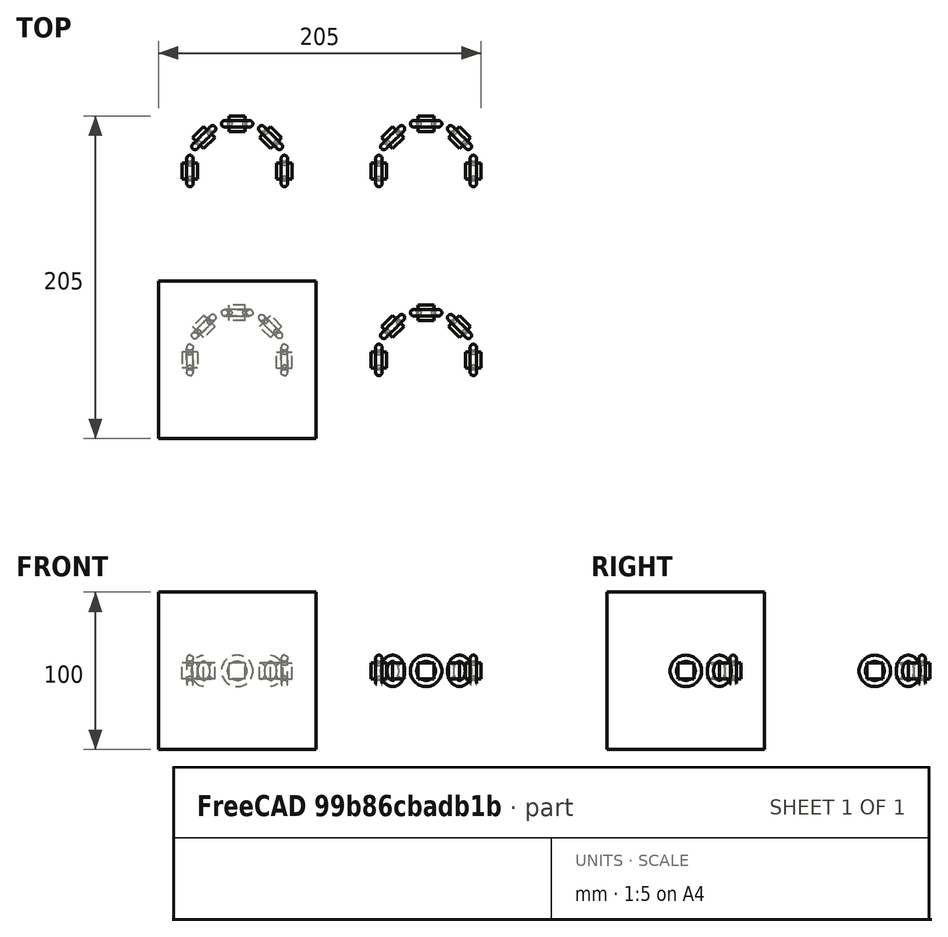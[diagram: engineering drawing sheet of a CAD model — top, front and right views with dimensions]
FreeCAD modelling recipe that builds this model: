
FCSTD DOCUMENT  (FreeCAD 0.21R33694 (Git))
Label: array-of-array-of-solid
License: All rights reserved
objects: App::DocumentObjectGroupPython×1251, Part::FeaturePython×5, App::Part×2, Part::MultiFuse×1
note: 5 computed .brp shape members not serialized (recipe doc carries the construction recipe); baked Part::Feature solids carry a one-line shape summary decoded from their .brp

FEATURE [App::DocumentObjectGroupPython] HALFPI  # scripted group (container) (typed FeaturePython)
  name = HALFPI
  value = pi/2.
FEATURE [App::DocumentObjectGroupPython] PI  # scripted group (container) (typed FeaturePython)
  name = PI
  value = 1.*pi
FEATURE [App::DocumentObjectGroupPython] TWOPI  # scripted group (container) (typed FeaturePython)
  name = TWOPI
  value = 2.*pi
FEATURE [App::DocumentObjectGroupPython] Constants  # scripted group (container) (typed FeaturePython)
  Group = -> [HALFPI,PI,TWOPI]
FEATURE [App::DocumentObjectGroupPython] Variables  # scripted group (container) (typed FeaturePython)
FEATURE [App::DocumentObjectGroupPython] Quantities  # scripted group (container) (typed FeaturePython)
FEATURE [App::DocumentObjectGroupPython] Isotopes  # scripted group (container) (typed FeaturePython)
FEATURE [App::DocumentObjectGroupPython] Elements  # scripted group (container) (typed FeaturePython)
FEATURE [App::DocumentObjectGroupPython] Matrix  # scripted group (container) (typed FeaturePython)
FEATURE [App::DocumentObjectGroupPython] Surfaces  # scripted group (container) (typed FeaturePython)
FEATURE [App::DocumentObjectGroupPython] Opticals  # scripted group (container) (typed FeaturePython)
  Group = -> [Matrix,Surfaces]
FEATURE [App::DocumentObjectGroupPython] G4Isotopes  # scripted group (container) (typed FeaturePython)
FEATURE [App::DocumentObjectGroupPython] H_element  # scripted group (container) (typed FeaturePython)
  Z = 1
  atom_value = 1.008
  formula = H
  name = H_element
FEATURE [App::DocumentObjectGroupPython] He_element  # scripted group (container) (typed FeaturePython)
  Z = 2
  atom_value = 4.0026
  formula = He
  name = He_element
FEATURE [App::DocumentObjectGroupPython] Li_element  # scripted group (container) (typed FeaturePython)
  Z = 3
  atom_value = 6.94
  formula = Li
  name = Li_element
FEATURE [App::DocumentObjectGroupPython] Be_element  # scripted group (container) (typed FeaturePython)
  Z = 4
  atom_value = 9.01218
  formula = Be
  name = Be_element
FEATURE [App::DocumentObjectGroupPython] B_element  # scripted group (container) (typed FeaturePython)
  Z = 5
  atom_value = 10.81
  formula = B
  name = B_element
FEATURE [App::DocumentObjectGroupPython] C_element  # scripted group (container) (typed FeaturePython)
  Z = 6
  atom_value = 12.011
  formula = C
  name = C_element
FEATURE [App::DocumentObjectGroupPython] N_element  # scripted group (container) (typed FeaturePython)
  Z = 7
  atom_value = 14.007
  formula = N
  name = N_element
FEATURE [App::DocumentObjectGroupPython] O_element  # scripted group (container) (typed FeaturePython)
  Z = 8
  atom_value = 15.999
  formula = O
  name = O_element
FEATURE [App::DocumentObjectGroupPython] F_element  # scripted group (container) (typed FeaturePython)
  Z = 9
  atom_value = 18.9984
  formula = F
  name = F_element
FEATURE [App::DocumentObjectGroupPython] Ne_element  # scripted group (container) (typed FeaturePython)
  Z = 10
  atom_value = 20.1797
  formula = Ne
  name = Ne_element
FEATURE [App::DocumentObjectGroupPython] Na_element  # scripted group (container) (typed FeaturePython)
  Z = 11
  atom_value = 22.9898
  formula = Na
  name = Na_element
FEATURE [App::DocumentObjectGroupPython] Mg_element  # scripted group (container) (typed FeaturePython)
  Z = 12
  atom_value = 24.305
  formula = Mg
  name = Mg_element
FEATURE [App::DocumentObjectGroupPython] Al_element  # scripted group (container) (typed FeaturePython)
  Z = 13
  atom_value = 26.9815
  formula = Al
  name = Al_element
FEATURE [App::DocumentObjectGroupPython] Si_element  # scripted group (container) (typed FeaturePython)
  Z = 14
  atom_value = 28.085
  formula = Si
  name = Si_element
FEATURE [App::DocumentObjectGroupPython] P_element  # scripted group (container) (typed FeaturePython)
  Z = 15
  atom_value = 30.9738
  formula = P
  name = P_element
FEATURE [App::DocumentObjectGroupPython] S_element  # scripted group (container) (typed FeaturePython)
  Z = 16
  atom_value = 32.06
  formula = S
  name = S_element
FEATURE [App::DocumentObjectGroupPython] Cl_element  # scripted group (container) (typed FeaturePython)
  Z = 17
  atom_value = 35.45
  formula = Cl
  name = Cl_element
FEATURE [App::DocumentObjectGroupPython] Ar_element  # scripted group (container) (typed FeaturePython)
  Z = 18
  atom_value = 39.95
  formula = Ar
  name = Ar_element
FEATURE [App::DocumentObjectGroupPython] K_element  # scripted group (container) (typed FeaturePython)
  Z = 19
  atom_value = 39.0983
  formula = K
  name = K_element
FEATURE [App::DocumentObjectGroupPython] Ca_element  # scripted group (container) (typed FeaturePython)
  Z = 20
  atom_value = 40.078
  formula = Ca
  name = Ca_element
FEATURE [App::DocumentObjectGroupPython] Sc_element  # scripted group (container) (typed FeaturePython)
  Z = 21
  atom_value = 44.9559
  formula = Sc
  name = Sc_element
FEATURE [App::DocumentObjectGroupPython] Ti_element  # scripted group (container) (typed FeaturePython)
  Z = 22
  atom_value = 47.867
  formula = Ti
  name = Ti_element
FEATURE [App::DocumentObjectGroupPython] V_element  # scripted group (container) (typed FeaturePython)
  Z = 23
  atom_value = 50.9415
  formula = V
  name = V_element
FEATURE [App::DocumentObjectGroupPython] Cr_element  # scripted group (container) (typed FeaturePython)
  Z = 24
  atom_value = 51.9961
  formula = Cr
  name = Cr_element
FEATURE [App::DocumentObjectGroupPython] Mn_element  # scripted group (container) (typed FeaturePython)
  Z = 25
  atom_value = 54.938
  formula = Mn
  name = Mn_element
FEATURE [App::DocumentObjectGroupPython] Fe_element  # scripted group (container) (typed FeaturePython)
  Z = 26
  atom_value = 55.845
  formula = Fe
  name = Fe_element
FEATURE [App::DocumentObjectGroupPython] Co_element  # scripted group (container) (typed FeaturePython)
  Z = 27
  atom_value = 58.9332
  formula = Co
  name = Co_element
FEATURE [App::DocumentObjectGroupPython] Ni_element  # scripted group (container) (typed FeaturePython)
  Z = 28
  atom_value = 58.6934
  formula = Ni
  name = Ni_element
FEATURE [App::DocumentObjectGroupPython] Cu_element  # scripted group (container) (typed FeaturePython)
  Z = 29
  atom_value = 63.546
  formula = Cu
  name = Cu_element
FEATURE [App::DocumentObjectGroupPython] Zn_element  # scripted group (container) (typed FeaturePython)
  Z = 30
  atom_value = 65.38
  formula = Zn
  name = Zn_element
FEATURE [App::DocumentObjectGroupPython] Ga_element  # scripted group (container) (typed FeaturePython)
  Z = 31
  atom_value = 69.723
  formula = Ga
  name = Ga_element
FEATURE [App::DocumentObjectGroupPython] Ge_element  # scripted group (container) (typed FeaturePython)
  Z = 32
  atom_value = 72.63
  formula = Ge
  name = Ge_element
FEATURE [App::DocumentObjectGroupPython] As_element  # scripted group (container) (typed FeaturePython)
  Z = 33
  atom_value = 74.9216
  formula = As
  name = As_element
FEATURE [App::DocumentObjectGroupPython] Se_element  # scripted group (container) (typed FeaturePython)
  Z = 34
  atom_value = 78.971
  formula = Se
  name = Se_element
FEATURE [App::DocumentObjectGroupPython] Br_element  # scripted group (container) (typed FeaturePython)
  Z = 35
  atom_value = 79.904
  formula = Br
  name = Br_element
FEATURE [App::DocumentObjectGroupPython] Kr_element  # scripted group (container) (typed FeaturePython)
  Z = 36
  atom_value = 83.798
  formula = Kr
  name = Kr_element
FEATURE [App::DocumentObjectGroupPython] Rb_element  # scripted group (container) (typed FeaturePython)
  Z = 37
  atom_value = 85.4678
  formula = Rb
  name = Rb_element
FEATURE [App::DocumentObjectGroupPython] Sr_element  # scripted group (container) (typed FeaturePython)
  Z = 38
  atom_value = 87.62
  formula = Sr
  name = Sr_element
FEATURE [App::DocumentObjectGroupPython] Y_element  # scripted group (container) (typed FeaturePython)
  Z = 39
  atom_value = 88.9058
  formula = Y
  name = Y_element
FEATURE [App::DocumentObjectGroupPython] Zr_element  # scripted group (container) (typed FeaturePython)
  Z = 40
  atom_value = 91.224
  formula = Zr
  name = Zr_element
FEATURE [App::DocumentObjectGroupPython] Nb_element  # scripted group (container) (typed FeaturePython)
  Z = 41
  atom_value = 92.9064
  formula = Nb
  name = Nb_element
FEATURE [App::DocumentObjectGroupPython] Mo_element  # scripted group (container) (typed FeaturePython)
  Z = 42
  atom_value = 95.95
  formula = Mo
  name = Mo_element
FEATURE [App::DocumentObjectGroupPython] Tc_element  # scripted group (container) (typed FeaturePython)
  Z = 43
  atom_value = 97
  formula = Tc
  name = Tc_element
FEATURE [App::DocumentObjectGroupPython] Ru_element  # scripted group (container) (typed FeaturePython)
  Z = 44
  atom_value = 101.07
  formula = Ru
  name = Ru_element
FEATURE [App::DocumentObjectGroupPython] Rh_element  # scripted group (container) (typed FeaturePython)
  Z = 45
  atom_value = 102.905
  formula = Rh
  name = Rh_element
FEATURE [App::DocumentObjectGroupPython] Pd_element  # scripted group (container) (typed FeaturePython)
  Z = 46
  atom_value = 106.42
  formula = Pd
  name = Pd_element
FEATURE [App::DocumentObjectGroupPython] Ag_element  # scripted group (container) (typed FeaturePython)
  Z = 47
  atom_value = 107.868
  formula = Ag
  name = Ag_element
FEATURE [App::DocumentObjectGroupPython] Cd_element  # scripted group (container) (typed FeaturePython)
  Z = 48
  atom_value = 112.414
  formula = Cd
  name = Cd_element
FEATURE [App::DocumentObjectGroupPython] In_element  # scripted group (container) (typed FeaturePython)
  Z = 49
  atom_value = 114.818
  formula = In
  name = In_element
FEATURE [App::DocumentObjectGroupPython] Sn_element  # scripted group (container) (typed FeaturePython)
  Z = 50
  atom_value = 118.71
  formula = Sn
  name = Sn_element
FEATURE [App::DocumentObjectGroupPython] Sb_element  # scripted group (container) (typed FeaturePython)
  Z = 51
  atom_value = 121.76
  formula = Sb
  name = Sb_element
FEATURE [App::DocumentObjectGroupPython] Te_element  # scripted group (container) (typed FeaturePython)
  Z = 52
  atom_value = 127.6
  formula = Te
  name = Te_element
FEATURE [App::DocumentObjectGroupPython] I_element  # scripted group (container) (typed FeaturePython)
  Z = 53
  atom_value = 126.904
  formula = I
  name = I_element
FEATURE [App::DocumentObjectGroupPython] Xe_element  # scripted group (container) (typed FeaturePython)
  Z = 54
  atom_value = 131.293
  formula = Xe
  name = Xe_element
FEATURE [App::DocumentObjectGroupPython] Cs_element  # scripted group (container) (typed FeaturePython)
  Z = 55
  atom_value = 132.905
  formula = Cs
  name = Cs_element
FEATURE [App::DocumentObjectGroupPython] Ba_element  # scripted group (container) (typed FeaturePython)
  Z = 56
  atom_value = 137.327
  formula = Ba
  name = Ba_element
FEATURE [App::DocumentObjectGroupPython] La_element  # scripted group (container) (typed FeaturePython)
  Z = 57
  atom_value = 138.905
  formula = La
  name = La_element
FEATURE [App::DocumentObjectGroupPython] Ce_element  # scripted group (container) (typed FeaturePython)
  Z = 58
  atom_value = 140.116
  formula = Ce
  name = Ce_element
FEATURE [App::DocumentObjectGroupPython] Pr_element  # scripted group (container) (typed FeaturePython)
  Z = 59
  atom_value = 140.908
  formula = Pr
  name = Pr_element
FEATURE [App::DocumentObjectGroupPython] Nd_element  # scripted group (container) (typed FeaturePython)
  Z = 60
  atom_value = 144.242
  formula = Nd
  name = Nd_element
FEATURE [App::DocumentObjectGroupPython] Pm_element  # scripted group (container) (typed FeaturePython)
  Z = 61
  atom_value = 145
  formula = Pm
  name = Pm_element
FEATURE [App::DocumentObjectGroupPython] Sm_element  # scripted group (container) (typed FeaturePython)
  Z = 62
  atom_value = 150.36
  formula = Sm
  name = Sm_element
FEATURE [App::DocumentObjectGroupPython] Eu_element  # scripted group (container) (typed FeaturePython)
  Z = 63
  atom_value = 151.964
  formula = Eu
  name = Eu_element
FEATURE [App::DocumentObjectGroupPython] Gd_element  # scripted group (container) (typed FeaturePython)
  Z = 64
  atom_value = 157.25
  formula = Gd
  name = Gd_element
FEATURE [App::DocumentObjectGroupPython] Tb_element  # scripted group (container) (typed FeaturePython)
  Z = 65
  atom_value = 158.925
  formula = Tb
  name = Tb_element
FEATURE [App::DocumentObjectGroupPython] Dy_element  # scripted group (container) (typed FeaturePython)
  Z = 66
  atom_value = 162.5
  formula = Dy
  name = Dy_element
FEATURE [App::DocumentObjectGroupPython] Ho_element  # scripted group (container) (typed FeaturePython)
  Z = 67
  atom_value = 164.93
  formula = Ho
  name = Ho_element
FEATURE [App::DocumentObjectGroupPython] Er_element  # scripted group (container) (typed FeaturePython)
  Z = 68
  atom_value = 167.259
  formula = Er
  name = Er_element
FEATURE [App::DocumentObjectGroupPython] Tm_element  # scripted group (container) (typed FeaturePython)
  Z = 69
  atom_value = 168.934
  formula = Tm
  name = Tm_element
FEATURE [App::DocumentObjectGroupPython] Yb_element  # scripted group (container) (typed FeaturePython)
  Z = 70
  atom_value = 173.045
  formula = Yb
  name = Yb_element
FEATURE [App::DocumentObjectGroupPython] Lu_element  # scripted group (container) (typed FeaturePython)
  Z = 71
  atom_value = 174.967
  formula = Lu
  name = Lu_element
FEATURE [App::DocumentObjectGroupPython] Hf_element  # scripted group (container) (typed FeaturePython)
  Z = 72
  atom_value = 178.49
  formula = Hf
  name = Hf_element
FEATURE [App::DocumentObjectGroupPython] Ta_element  # scripted group (container) (typed FeaturePython)
  Z = 73
  atom_value = 180.948
  formula = Ta
  name = Ta_element
FEATURE [App::DocumentObjectGroupPython] W_element  # scripted group (container) (typed FeaturePython)
  Z = 74
  atom_value = 183.84
  formula = W
  name = W_element
FEATURE [App::DocumentObjectGroupPython] Re_element  # scripted group (container) (typed FeaturePython)
  Z = 75
  atom_value = 186.207
  formula = Re
  name = Re_element
FEATURE [App::DocumentObjectGroupPython] Os_element  # scripted group (container) (typed FeaturePython)
  Z = 76
  atom_value = 190.23
  formula = Os
  name = Os_element
FEATURE [App::DocumentObjectGroupPython] Ir_element  # scripted group (container) (typed FeaturePython)
  Z = 77
  atom_value = 192.217
  formula = Ir
  name = Ir_element
FEATURE [App::DocumentObjectGroupPython] Pt_element  # scripted group (container) (typed FeaturePython)
  Z = 78
  atom_value = 195.084
  formula = Pt
  name = Pt_element
FEATURE [App::DocumentObjectGroupPython] Au_element  # scripted group (container) (typed FeaturePython)
  Z = 79
  atom_value = 196.967
  formula = Au
  name = Au_element
FEATURE [App::DocumentObjectGroupPython] Hg_element  # scripted group (container) (typed FeaturePython)
  Z = 80
  atom_value = 200.592
  formula = Hg
  name = Hg_element
FEATURE [App::DocumentObjectGroupPython] Tl_element  # scripted group (container) (typed FeaturePython)
  Z = 81
  atom_value = 204.38
  formula = Tl
  name = Tl_element
FEATURE [App::DocumentObjectGroupPython] Pb_element  # scripted group (container) (typed FeaturePython)
  Z = 82
  atom_value = 207.2
  formula = Pb
  name = Pb_element
FEATURE [App::DocumentObjectGroupPython] Bi_element  # scripted group (container) (typed FeaturePython)
  Z = 83
  atom_value = 208.98
  formula = Bi
  name = Bi_element
FEATURE [App::DocumentObjectGroupPython] Po_element  # scripted group (container) (typed FeaturePython)
  Z = 84
  atom_value = 209
  formula = Po
  name = Po_element
FEATURE [App::DocumentObjectGroupPython] At_element  # scripted group (container) (typed FeaturePython)
  Z = 85
  atom_value = 210
  formula = At
  name = At_element
FEATURE [App::DocumentObjectGroupPython] Rn_element  # scripted group (container) (typed FeaturePython)
  Z = 86
  atom_value = 222
  formula = Rn
  name = Rn_element
FEATURE [App::DocumentObjectGroupPython] Fr_element  # scripted group (container) (typed FeaturePython)
  Z = 87
  atom_value = 223
  formula = Fr
  name = Fr_element
FEATURE [App::DocumentObjectGroupPython] Ra_element  # scripted group (container) (typed FeaturePython)
  Z = 88
  atom_value = 226
  formula = Ra
  name = Ra_element
FEATURE [App::DocumentObjectGroupPython] Ac_element  # scripted group (container) (typed FeaturePython)
  Z = 89
  atom_value = 227
  formula = Ac
  name = Ac_element
FEATURE [App::DocumentObjectGroupPython] Th_element  # scripted group (container) (typed FeaturePython)
  Z = 90
  atom_value = 232.038
  formula = Th
  name = Th_element
FEATURE [App::DocumentObjectGroupPython] Pa_element  # scripted group (container) (typed FeaturePython)
  Z = 91
  atom_value = 231.036
  formula = Pa
  name = Pa_element
FEATURE [App::DocumentObjectGroupPython] U_element  # scripted group (container) (typed FeaturePython)
  Z = 92
  atom_value = 238.029
  formula = U
  name = U_element
FEATURE [App::DocumentObjectGroupPython] Np_element  # scripted group (container) (typed FeaturePython)
  Z = 93
  atom_value = 237
  formula = Np
  name = Np_element
FEATURE [App::DocumentObjectGroupPython] Pu_element  # scripted group (container) (typed FeaturePython)
  Z = 94
  atom_value = 244
  formula = Pu
  name = Pu_element
FEATURE [App::DocumentObjectGroupPython] Am_element  # scripted group (container) (typed FeaturePython)
  Z = 95
  atom_value = 243
  formula = Am
  name = Am_element
FEATURE [App::DocumentObjectGroupPython] Cm_element  # scripted group (container) (typed FeaturePython)
  Z = 96
  atom_value = 247
  formula = Cm
  name = Cm_element
FEATURE [App::DocumentObjectGroupPython] Bk_element  # scripted group (container) (typed FeaturePython)
  Z = 97
  atom_value = 247
  formula = Bk
  name = Bk_element
FEATURE [App::DocumentObjectGroupPython] Cf_element  # scripted group (container) (typed FeaturePython)
  Z = 98
  atom_value = 251
  formula = Cf
  name = Cf_element
FEATURE [App::DocumentObjectGroupPython] G4Elements  # scripted group (container) (typed FeaturePython)
  Group = -> [H_element,He_element,Li_element,Be_element,B_element,C_element,N_element,O_element,F_element,Ne_element,Na_element,Mg_element,Al_element,Si_element,P_element,S_element,Cl_element,Ar_element,K_element,Ca_element,Sc_element,Ti_element,V_element,Cr_element,Mn_element,Fe_element,Co_element,Ni_element,Cu_element,Zn_element,Ga_element,Ge_element,As_element,Se_element,Br_element,Kr_element,Rb_element,+61 more]
FEATURE [App::DocumentObjectGroupPython] H_element001  label="H_element : 0.101"  # scripted group (container) (typed FeaturePython)
  n = 0.101327
FEATURE [App::DocumentObjectGroupPython] C_element001  label="C_element : 0.775"  # scripted group (container) (typed FeaturePython)
  n = 0.7755
FEATURE [App::DocumentObjectGroupPython] N_element001  label="N_element : 0.035"  # scripted group (container) (typed FeaturePython)
  n = 0.035057
FEATURE [App::DocumentObjectGroupPython] O_element001  label="O_element : 0.052"  # scripted group (container) (typed FeaturePython)
  n = 0.0523159
FEATURE [App::DocumentObjectGroupPython] F_element001  label="F_element : 0.017"  # scripted group (container) (typed FeaturePython)
  n = 0.017422
FEATURE [App::DocumentObjectGroupPython] Ca_element001  label="Ca_element : 0.018"  # scripted group (container) (typed FeaturePython)
  n = 0.018378
FEATURE [App::DocumentObjectGroupPython] G4_A_150_TISSUE  label="G4_A-150_TISSUE"  # scripted group (container) (typed FeaturePython)
  Dunit = g/cm3
  Dvalue = 1.127
  Group = -> [H_element001,C_element001,N_element001,O_element001,F_element001,Ca_element001]
  conduct = 2
  density = 1
  expand = 3
  formula = G4_A-150_TISSUE
  name = G4_A-150_TISSUE
  specific = 4
FEATURE [App::DocumentObjectGroupPython] C_element002  label="C_element : 3"  # scripted group (container) (typed FeaturePython)
  n = 3
  ref = C_element
FEATURE [App::DocumentObjectGroupPython] H_element002  label="H_element : 6"  # scripted group (container) (typed FeaturePython)
  n = 6
  ref = H_element
FEATURE [App::DocumentObjectGroupPython] O_element002  label="O_element : 1"  # scripted group (container) (typed FeaturePython)
  n = 1
  ref = O_element
FEATURE [App::DocumentObjectGroupPython] G4_ACETONE  # scripted group (container) (typed FeaturePython)
  Dunit = g/cm3
  Dvalue = 0.7899
  Group = -> [C_element002,H_element002,O_element002]
  conduct = 2
  density = 1
  expand = 3
  formula = G4_ACETONE
  name = G4_ACETONE
  specific = 4
FEATURE [App::DocumentObjectGroupPython] C_element003  label="C_element : 2"  # scripted group (container) (typed FeaturePython)
  n = 2
  ref = C_element
FEATURE [App::DocumentObjectGroupPython] H_element003  label="H_element : 2"  # scripted group (container) (typed FeaturePython)
  n = 2
  ref = H_element
FEATURE [App::DocumentObjectGroupPython] G4_ACETYLENE  # scripted group (container) (typed FeaturePython)
  Dunit = g/cm3
  Dvalue = 0.0010967
  Group = -> [C_element003,H_element003]
  conduct = 2
  density = 1
  expand = 3
  formula = G4_ACETYLENE
  name = G4_ACETYLENE
  specific = 4
FEATURE [App::DocumentObjectGroupPython] C_element004  label="C_element : 5"  # scripted group (container) (typed FeaturePython)
  n = 5
  ref = C_element
FEATURE [App::DocumentObjectGroupPython] H_element004  label="H_element : 5"  # scripted group (container) (typed FeaturePython)
  n = 5
  ref = H_element
FEATURE [App::DocumentObjectGroupPython] N_element002  label="N_element : 5"  # scripted group (container) (typed FeaturePython)
  n = 5
  ref = N_element
FEATURE [App::DocumentObjectGroupPython] G4_ADENINE  # scripted group (container) (typed FeaturePython)
  Dunit = g/cm3
  Dvalue = 1.6
  Group = -> [C_element004,H_element004,N_element002]
  conduct = 2
  density = 1
  expand = 3
  formula = G4_ADENINE
  name = G4_ADENINE
  specific = 4
FEATURE [App::DocumentObjectGroupPython] H_element005  label="H_element : 0.114"  # scripted group (container) (typed FeaturePython)
  n = 0.114
FEATURE [App::DocumentObjectGroupPython] C_element005  label="C_element : 0.598"  # scripted group (container) (typed FeaturePython)
  n = 0.598
FEATURE [App::DocumentObjectGroupPython] N_element003  label="N_element : 0.007"  # scripted group (container) (typed FeaturePython)
  n = 0.007
FEATURE [App::DocumentObjectGroupPython] O_element003  label="O_element : 0.278"  # scripted group (container) (typed FeaturePython)
  n = 0.278
FEATURE [App::DocumentObjectGroupPython] Na_element001  label="Na_element : 0.001"  # scripted group (container) (typed FeaturePython)
  n = 0.001
FEATURE [App::DocumentObjectGroupPython] S_element001  label="S_element : 0.001"  # scripted group (container) (typed FeaturePython)
  n = 0.001
FEATURE [App::DocumentObjectGroupPython] Cl_element001  label="Cl_element : 0.001"  # scripted group (container) (typed FeaturePython)
  n = 0.001
FEATURE [App::DocumentObjectGroupPython] G4_ADIPOSE_TISSUE_ICRP  # scripted group (container) (typed FeaturePython)
  Dunit = g/cm3
  Dvalue = 0.95
  Group = -> [H_element005,C_element005,N_element003,O_element003,Na_element001,S_element001,Cl_element001]
  conduct = 2
  density = 1
  expand = 3
  formula = G4_ADIPOSE_TISSUE_ICRP
  name = G4_ADIPOSE_TISSUE_ICRP
  specific = 4
FEATURE [App::DocumentObjectGroupPython] C_element006  label="C_element : 0.000"  # scripted group (container) (typed FeaturePython)
  n = 0.000124
FEATURE [App::DocumentObjectGroupPython] N_element004  label="N_element : 0.755"  # scripted group (container) (typed FeaturePython)
  n = 0.755268
FEATURE [App::DocumentObjectGroupPython] O_element004  label="O_element : 0.232"  # scripted group (container) (typed FeaturePython)
  n = 0.231781
FEATURE [App::DocumentObjectGroupPython] Ar_element001  label="Ar_element : 0.013"  # scripted group (container) (typed FeaturePython)
  n = 0.012827
FEATURE [App::DocumentObjectGroupPython] G4_AIR  # scripted group (container) (typed FeaturePython)
  Dunit = g/cm3
  Dvalue = 0.00120479
  Group = -> [C_element006,N_element004,O_element004,Ar_element001]
  conduct = 2
  density = 1
  expand = 3
  formula = G4_AIR
  name = G4_AIR
  specific = 4
FEATURE [App::DocumentObjectGroupPython] C_element007  label="C_element : 006"  # scripted group (container) (typed FeaturePython)
  n = 3
  ref = C_element
FEATURE [App::DocumentObjectGroupPython] H_element006  label="H_element : 7"  # scripted group (container) (typed FeaturePython)
  n = 7
  ref = H_element
FEATURE [App::DocumentObjectGroupPython] N_element005  label="N_element : 1"  # scripted group (container) (typed FeaturePython)
  n = 1
  ref = N_element
FEATURE [App::DocumentObjectGroupPython] O_element005  label="O_element : 2"  # scripted group (container) (typed FeaturePython)
  n = 2
  ref = O_element
FEATURE [App::DocumentObjectGroupPython] G4_ALANINE  # scripted group (container) (typed FeaturePython)
  Dunit = g/cm3
  Dvalue = 1.42
  Group = -> [C_element007,H_element006,N_element005,O_element005]
  conduct = 2
  density = 1
  expand = 3
  formula = G4_ALANINE
  name = G4_ALANINE
  specific = 4
FEATURE [App::DocumentObjectGroupPython] Al_element001  label="Al_element : 2"  # scripted group (container) (typed FeaturePython)
  n = 2
  ref = Al_element
FEATURE [App::DocumentObjectGroupPython] O_element006  label="O_element : 3"  # scripted group (container) (typed FeaturePython)
  n = 3
  ref = O_element
FEATURE [App::DocumentObjectGroupPython] G4_ALUMINUM_OXIDE  # scripted group (container) (typed FeaturePython)
  Dunit = g/cm3
  Dvalue = 3.97
  Group = -> [Al_element001,O_element006]
  conduct = 2
  density = 1
  expand = 3
  formula = G4_ALUMINUM_OXIDE
  name = G4_ALUMINUM_OXIDE
  specific = 4
FEATURE [App::DocumentObjectGroupPython] H_element007  label="H_element : 0.106"  # scripted group (container) (typed FeaturePython)
  n = 0.10593
FEATURE [App::DocumentObjectGroupPython] C_element008  label="C_element : 0.789"  # scripted group (container) (typed FeaturePython)
  n = 0.788974
FEATURE [App::DocumentObjectGroupPython] O_element007  label="O_element : 0.105"  # scripted group (container) (typed FeaturePython)
  n = 0.105096
FEATURE [App::DocumentObjectGroupPython] G4_AMBER  # scripted group (container) (typed FeaturePython)
  Dunit = g/cm3
  Dvalue = 1.1
  Group = -> [H_element007,C_element008,O_element007]
  conduct = 2
  density = 1
  expand = 3
  formula = G4_AMBER
  name = G4_AMBER
  specific = 4
FEATURE [App::DocumentObjectGroupPython] N_element006  label="N_element : 006"  # scripted group (container) (typed FeaturePython)
  n = 1
  ref = N_element
FEATURE [App::DocumentObjectGroupPython] H_element008  label="H_element : 3"  # scripted group (container) (typed FeaturePython)
  n = 3
  ref = H_element
FEATURE [App::DocumentObjectGroupPython] G4_AMMONIA  # scripted group (container) (typed FeaturePython)
  Dunit = g/cm3
  Dvalue = 0.000826019
  Group = -> [N_element006,H_element008]
  conduct = 2
  density = 1
  expand = 3
  formula = G4_AMMONIA
  name = G4_AMMONIA
  specific = 4
FEATURE [App::DocumentObjectGroupPython] C_element009  label="C_element : 6"  # scripted group (container) (typed FeaturePython)
  n = 6
  ref = C_element
FEATURE [App::DocumentObjectGroupPython] H_element009  label="H_element : 008"  # scripted group (container) (typed FeaturePython)
  n = 7
  ref = H_element
FEATURE [App::DocumentObjectGroupPython] N_element007  label="N_element : 007"  # scripted group (container) (typed FeaturePython)
  n = 1
  ref = N_element
FEATURE [App::DocumentObjectGroupPython] G4_ANILINE  # scripted group (container) (typed FeaturePython)
  Dunit = g/cm3
  Dvalue = 1.0235
  Group = -> [C_element009,H_element009,N_element007]
  conduct = 2
  density = 1
  expand = 3
  formula = G4_ANILINE
  name = G4_ANILINE
  specific = 4
FEATURE [App::DocumentObjectGroupPython] C_element010  label="C_element : 14"  # scripted group (container) (typed FeaturePython)
  n = 14
  ref = C_element
FEATURE [App::DocumentObjectGroupPython] H_element010  label="H_element : 10"  # scripted group (container) (typed FeaturePython)
  n = 10
  ref = H_element
FEATURE [App::DocumentObjectGroupPython] G4_ANTHRACENE  # scripted group (container) (typed FeaturePython)
  Dunit = g/cm3
  Dvalue = 1.283
  Group = -> [C_element010,H_element010]
  conduct = 2
  density = 1
  expand = 3
  formula = G4_ANTHRACENE
  name = G4_ANTHRACENE
  specific = 4
FEATURE [App::DocumentObjectGroupPython] H_element011  label="H_element : 0.065"  # scripted group (container) (typed FeaturePython)
  n = 0.0654709
FEATURE [App::DocumentObjectGroupPython] C_element011  label="C_element : 0.537"  # scripted group (container) (typed FeaturePython)
  n = 0.536944
FEATURE [App::DocumentObjectGroupPython] N_element008  label="N_element : 0.021"  # scripted group (container) (typed FeaturePython)
  n = 0.0215
FEATURE [App::DocumentObjectGroupPython] O_element008  label="O_element : 0.032"  # scripted group (container) (typed FeaturePython)
  n = 0.032085
FEATURE [App::DocumentObjectGroupPython] F_element002  label="F_element : 0.167"  # scripted group (container) (typed FeaturePython)
  n = 0.167411
FEATURE [App::DocumentObjectGroupPython] Ca_element002  label="Ca_element : 0.177"  # scripted group (container) (typed FeaturePython)
  n = 0.176589
FEATURE [App::DocumentObjectGroupPython] G4_B_100_BONE  label="G4_B-100_BONE"  # scripted group (container) (typed FeaturePython)
  Dunit = g/cm3
  Dvalue = 1.45
  Group = -> [H_element011,C_element011,N_element008,O_element008,F_element002,Ca_element002]
  conduct = 2
  density = 1
  expand = 3
  formula = G4_B-100_BONE
  name = G4_B-100_BONE
  specific = 4
FEATURE [App::DocumentObjectGroupPython] H_element012  label="H_element : 0.057"  # scripted group (container) (typed FeaturePython)
  n = 0.057441
FEATURE [App::DocumentObjectGroupPython] C_element012  label="C_element : 0.790"  # scripted group (container) (typed FeaturePython)
  n = 0.774591
FEATURE [App::DocumentObjectGroupPython] O_element009  label="O_element : 0.168"  # scripted group (container) (typed FeaturePython)
  n = 0.167968
FEATURE [App::DocumentObjectGroupPython] G4_BAKELITE  # scripted group (container) (typed FeaturePython)
  Dunit = g/cm3
  Dvalue = 1.25
  Group = -> [H_element012,C_element012,O_element009]
  conduct = 2
  density = 1
  expand = 3
  formula = G4_BAKELITE
  name = G4_BAKELITE
  specific = 4
FEATURE [App::DocumentObjectGroupPython] Ba_element001  label="Ba_element : 1"  # scripted group (container) (typed FeaturePython)
  n = 1
  ref = Ba_element
FEATURE [App::DocumentObjectGroupPython] F_element003  label="F_element : 2"  # scripted group (container) (typed FeaturePython)
  n = 2
  ref = F_element
FEATURE [App::DocumentObjectGroupPython] G4_BARIUM_FLUORIDE  # scripted group (container) (typed FeaturePython)
  Dunit = g/cm3
  Dvalue = 4.89
  Group = -> [Ba_element001,F_element003]
  conduct = 2
  density = 1
  expand = 3
  formula = G4_BARIUM_FLUORIDE
  name = G4_BARIUM_FLUORIDE
  specific = 4
FEATURE [App::DocumentObjectGroupPython] Ba_element002  label="Ba_element : 002"  # scripted group (container) (typed FeaturePython)
  n = 1
  ref = Ba_element
FEATURE [App::DocumentObjectGroupPython] S_element002  label="S_element : 1"  # scripted group (container) (typed FeaturePython)
  n = 1
  ref = S_element
FEATURE [App::DocumentObjectGroupPython] O_element010  label="O_element : 4"  # scripted group (container) (typed FeaturePython)
  n = 4
  ref = O_element
FEATURE [App::DocumentObjectGroupPython] G4_BARIUM_SULFATE  # scripted group (container) (typed FeaturePython)
  Dunit = g/cm3
  Dvalue = 4.5
  Group = -> [Ba_element002,S_element002,O_element010]
  conduct = 2
  density = 1
  expand = 3
  formula = G4_BARIUM_SULFATE
  name = G4_BARIUM_SULFATE
  specific = 4
FEATURE [App::DocumentObjectGroupPython] C_element013  label="C_element : 007"  # scripted group (container) (typed FeaturePython)
  n = 6
  ref = C_element
FEATURE [App::DocumentObjectGroupPython] H_element013  label="H_element : 009"  # scripted group (container) (typed FeaturePython)
  n = 6
  ref = H_element
FEATURE [App::DocumentObjectGroupPython] G4_BENZENE  # scripted group (container) (typed FeaturePython)
  Dunit = g/cm3
  Dvalue = 0.87865
  Group = -> [C_element013,H_element013]
  conduct = 2
  density = 1
  expand = 3
  formula = G4_BENZENE
  name = G4_BENZENE
  specific = 4
FEATURE [App::DocumentObjectGroupPython] Be_element001  label="Be_element : 1"  # scripted group (container) (typed FeaturePython)
  n = 1
  ref = Be_element
FEATURE [App::DocumentObjectGroupPython] O_element011  label="O_element : 005"  # scripted group (container) (typed FeaturePython)
  n = 1
  ref = O_element
FEATURE [App::DocumentObjectGroupPython] G4_BERYLLIUM_OXIDE  # scripted group (container) (typed FeaturePython)
  Dunit = g/cm3
  Dvalue = 3.01
  Group = -> [Be_element001,O_element011]
  conduct = 2
  density = 1
  expand = 3
  formula = G4_BERYLLIUM_OXIDE
  name = G4_BERYLLIUM_OXIDE
  specific = 4
FEATURE [App::DocumentObjectGroupPython] Bi_element001  label="Bi_element : 4"  # scripted group (container) (typed FeaturePython)
  n = 4
  ref = Bi_element
FEATURE [App::DocumentObjectGroupPython] Ge_element001  label="Ge_element : 3"  # scripted group (container) (typed FeaturePython)
  n = 3
  ref = Ge_element
FEATURE [App::DocumentObjectGroupPython] O_element012  label="O_element : 12"  # scripted group (container) (typed FeaturePython)
  n = 12
  ref = O_element
FEATURE [App::DocumentObjectGroupPython] G4_BGO  # scripted group (container) (typed FeaturePython)
  Dunit = g/cm3
  Dvalue = 7.13
  Group = -> [Bi_element001,Ge_element001,O_element012]
  conduct = 2
  density = 1
  expand = 3
  formula = G4_BGO
  name = G4_BGO
  specific = 4
FEATURE [App::DocumentObjectGroupPython] H_element014  label="H_element : 0.102"  # scripted group (container) (typed FeaturePython)
  n = 0.102
FEATURE [App::DocumentObjectGroupPython] C_element014  label="C_element : 0.110"  # scripted group (container) (typed FeaturePython)
  n = 0.11
FEATURE [App::DocumentObjectGroupPython] N_element009  label="N_element : 0.033"  # scripted group (container) (typed FeaturePython)
  n = 0.033
FEATURE [App::DocumentObjectGroupPython] O_element013  label="O_element : 0.745"  # scripted group (container) (typed FeaturePython)
  n = 0.745
FEATURE [App::DocumentObjectGroupPython] Na_element002  label="Na_element : 0.002"  # scripted group (container) (typed FeaturePython)
  n = 0.001
FEATURE [App::DocumentObjectGroupPython] P_element001  label="P_element : 0.001"  # scripted group (container) (typed FeaturePython)
  n = 0.001
FEATURE [App::DocumentObjectGroupPython] S_element003  label="S_element : 0.002"  # scripted group (container) (typed FeaturePython)
  n = 0.002
FEATURE [App::DocumentObjectGroupPython] Cl_element002  label="Cl_element : 0.003"  # scripted group (container) (typed FeaturePython)
  n = 0.003
FEATURE [App::DocumentObjectGroupPython] K_element001  label="K_element : 0.002"  # scripted group (container) (typed FeaturePython)
  n = 0.002
FEATURE [App::DocumentObjectGroupPython] Fe_element001  label="Fe_element : 0.001"  # scripted group (container) (typed FeaturePython)
  n = 0.001
FEATURE [App::DocumentObjectGroupPython] G4_BLOOD_ICRP  # scripted group (container) (typed FeaturePython)
  Dunit = g/cm3
  Dvalue = 1.06
  Group = -> [H_element014,C_element014,N_element009,O_element013,Na_element002,P_element001,S_element003,Cl_element002,K_element001,Fe_element001]
  conduct = 2
  density = 1
  expand = 3
  formula = G4_BLOOD_ICRP
  name = G4_BLOOD_ICRP
  specific = 4
FEATURE [App::DocumentObjectGroupPython] H_element015  label="H_element : 0.064"  # scripted group (container) (typed FeaturePython)
  n = 0.064
FEATURE [App::DocumentObjectGroupPython] C_element015  label="C_element : 0.278"  # scripted group (container) (typed FeaturePython)
  n = 0.278
FEATURE [App::DocumentObjectGroupPython] N_element010  label="N_element : 0.027"  # scripted group (container) (typed FeaturePython)
  n = 0.027
FEATURE [App::DocumentObjectGroupPython] O_element014  label="O_element : 0.410"  # scripted group (container) (typed FeaturePython)
  n = 0.41
FEATURE [App::DocumentObjectGroupPython] Mg_element001  label="Mg_element : 0.002"  # scripted group (container) (typed FeaturePython)
  n = 0.002
FEATURE [App::DocumentObjectGroupPython] P_element002  label="P_element : 0.070"  # scripted group (container) (typed FeaturePython)
  n = 0.07
FEATURE [App::DocumentObjectGroupPython] S_element004  label="S_element : 0.003"  # scripted group (container) (typed FeaturePython)
  n = 0.002
FEATURE [App::DocumentObjectGroupPython] Ca_element003  label="Ca_element : 0.147"  # scripted group (container) (typed FeaturePython)
  n = 0.147
FEATURE [App::DocumentObjectGroupPython] G4_BONE_COMPACT_ICRU  # scripted group (container) (typed FeaturePython)
  Dunit = g/cm3
  Dvalue = 1.85
  Group = -> [H_element015,C_element015,N_element010,O_element014,Mg_element001,P_element002,S_element004,Ca_element003]
  conduct = 2
  density = 1
  expand = 3
  formula = G4_BONE_COMPACT_ICRU
  name = G4_BONE_COMPACT_ICRU
  specific = 4
FEATURE [App::DocumentObjectGroupPython] H_element016  label="H_element : 0.034"  # scripted group (container) (typed FeaturePython)
  n = 0.034
FEATURE [App::DocumentObjectGroupPython] C_element016  label="C_element : 0.155"  # scripted group (container) (typed FeaturePython)
  n = 0.155
FEATURE [App::DocumentObjectGroupPython] N_element011  label="N_element : 0.042"  # scripted group (container) (typed FeaturePython)
  n = 0.042
FEATURE [App::DocumentObjectGroupPython] O_element015  label="O_element : 0.435"  # scripted group (container) (typed FeaturePython)
  n = 0.435
FEATURE [App::DocumentObjectGroupPython] Na_element003  label="Na_element : 0.003"  # scripted group (container) (typed FeaturePython)
  n = 0.001
FEATURE [App::DocumentObjectGroupPython] Mg_element002  label="Mg_element : 0.003"  # scripted group (container) (typed FeaturePython)
  n = 0.002
FEATURE [App::DocumentObjectGroupPython] P_element003  label="P_element : 0.103"  # scripted group (container) (typed FeaturePython)
  n = 0.103
FEATURE [App::DocumentObjectGroupPython] S_element005  label="S_element : 0.004"  # scripted group (container) (typed FeaturePython)
  n = 0.003
FEATURE [App::DocumentObjectGroupPython] Ca_element004  label="Ca_element : 0.225"  # scripted group (container) (typed FeaturePython)
  n = 0.225
FEATURE [App::DocumentObjectGroupPython] G4_BONE_CORTICAL_ICRP  # scripted group (container) (typed FeaturePython)
  Dunit = g/cm3
  Dvalue = 1.92
  Group = -> [H_element016,C_element016,N_element011,O_element015,Na_element003,Mg_element002,P_element003,S_element005,Ca_element004]
  conduct = 2
  density = 1
  expand = 3
  formula = G4_BONE_CORTICAL_ICRP
  name = G4_BONE_CORTICAL_ICRP
  specific = 4
FEATURE [App::DocumentObjectGroupPython] B_element001  label="B_element : 4"  # scripted group (container) (typed FeaturePython)
  n = 4
  ref = B_element
FEATURE [App::DocumentObjectGroupPython] C_element017  label="C_element : 1"  # scripted group (container) (typed FeaturePython)
  n = 1
  ref = C_element
FEATURE [App::DocumentObjectGroupPython] G4_BORON_CARBIDE  # scripted group (container) (typed FeaturePython)
  Dunit = g/cm3
  Dvalue = 2.52
  Group = -> [B_element001,C_element017]
  conduct = 2
  density = 1
  expand = 3
  formula = G4_BORON_CARBIDE
  name = G4_BORON_CARBIDE
  specific = 4
FEATURE [App::DocumentObjectGroupPython] B_element002  label="B_element : 2"  # scripted group (container) (typed FeaturePython)
  n = 2
  ref = B_element
FEATURE [App::DocumentObjectGroupPython] O_element016  label="O_element : 006"  # scripted group (container) (typed FeaturePython)
  n = 3
  ref = O_element
FEATURE [App::DocumentObjectGroupPython] G4_BORON_OXIDE  # scripted group (container) (typed FeaturePython)
  Dunit = g/cm3
  Dvalue = 1.812
  Group = -> [B_element002,O_element016]
  conduct = 2
  density = 1
  expand = 3
  formula = G4_BORON_OXIDE
  name = G4_BORON_OXIDE
  specific = 4
FEATURE [App::DocumentObjectGroupPython] H_element017  label="H_element : 0.107"  # scripted group (container) (typed FeaturePython)
  n = 0.107
FEATURE [App::DocumentObjectGroupPython] C_element018  label="C_element : 0.145"  # scripted group (container) (typed FeaturePython)
  n = 0.145
FEATURE [App::DocumentObjectGroupPython] N_element012  label="N_element : 0.022"  # scripted group (container) (typed FeaturePython)
  n = 0.022
FEATURE [App::DocumentObjectGroupPython] O_element017  label="O_element : 0.712"  # scripted group (container) (typed FeaturePython)
  n = 0.712
FEATURE [App::DocumentObjectGroupPython] Na_element004  label="Na_element : 0.004"  # scripted group (container) (typed FeaturePython)
  n = 0.002
FEATURE [App::DocumentObjectGroupPython] P_element004  label="P_element : 0.004"  # scripted group (container) (typed FeaturePython)
  n = 0.004
FEATURE [App::DocumentObjectGroupPython] S_element006  label="S_element : 0.005"  # scripted group (container) (typed FeaturePython)
  n = 0.002
FEATURE [App::DocumentObjectGroupPython] Cl_element003  label="Cl_element : 0.004"  # scripted group (container) (typed FeaturePython)
  n = 0.003
FEATURE [App::DocumentObjectGroupPython] K_element002  label="K_element : 0.003"  # scripted group (container) (typed FeaturePython)
  n = 0.003
FEATURE [App::DocumentObjectGroupPython] G4_BRAIN_ICRP  # scripted group (container) (typed FeaturePython)
  Dunit = g/cm3
  Dvalue = 1.04
  Group = -> [H_element017,C_element018,N_element012,O_element017,Na_element004,P_element004,S_element006,Cl_element003,K_element002]
  conduct = 2
  density = 1
  expand = 3
  formula = G4_BRAIN_ICRP
  name = G4_BRAIN_ICRP
  specific = 4
FEATURE [App::DocumentObjectGroupPython] C_element019  label="C_element : 4"  # scripted group (container) (typed FeaturePython)
  n = 4
  ref = C_element
FEATURE [App::DocumentObjectGroupPython] H_element018  label="H_element : 010"  # scripted group (container) (typed FeaturePython)
  n = 10
  ref = H_element
FEATURE [App::DocumentObjectGroupPython] G4_BUTANE  # scripted group (container) (typed FeaturePython)
  Dunit = g/cm3
  Dvalue = 0.00249343
  Group = -> [C_element019,H_element018]
  conduct = 2
  density = 1
  expand = 3
  formula = G4_BUTANE
  name = G4_BUTANE
  specific = 4
FEATURE [App::DocumentObjectGroupPython] C_element020  label="C_element : 008"  # scripted group (container) (typed FeaturePython)
  n = 4
  ref = C_element
FEATURE [App::DocumentObjectGroupPython] H_element019  label="H_element : 011"  # scripted group (container) (typed FeaturePython)
  n = 10
  ref = H_element
FEATURE [App::DocumentObjectGroupPython] O_element018  label="O_element : 007"  # scripted group (container) (typed FeaturePython)
  n = 1
  ref = O_element
FEATURE [App::DocumentObjectGroupPython] G4_N_BUTYL_ALCOHOL  label="G4_N-BUTYL_ALCOHOL"  # scripted group (container) (typed FeaturePython)
  Dunit = g/cm3
  Dvalue = 0.8098
  Group = -> [C_element020,H_element019,O_element018]
  conduct = 2
  density = 1
  expand = 3
  formula = G4_N-BUTYL_ALCOHOL
  name = G4_N-BUTYL_ALCOHOL
  specific = 4
FEATURE [App::DocumentObjectGroupPython] H_element020  label="H_element : 0.025"  # scripted group (container) (typed FeaturePython)
  n = 0.02468
FEATURE [App::DocumentObjectGroupPython] C_element021  label="C_element : 0.502"  # scripted group (container) (typed FeaturePython)
  n = 0.501611
FEATURE [App::DocumentObjectGroupPython] O_element019  label="O_element : 0.005"  # scripted group (container) (typed FeaturePython)
  n = 0.004527
FEATURE [App::DocumentObjectGroupPython] F_element004  label="F_element : 0.465"  # scripted group (container) (typed FeaturePython)
  n = 0.465209
FEATURE [App::DocumentObjectGroupPython] Si_element001  label="Si_element : 0.004"  # scripted group (container) (typed FeaturePython)
  n = 0.003973
FEATURE [App::DocumentObjectGroupPython] G4_C_552  label="G4_C-552"  # scripted group (container) (typed FeaturePython)
  Dunit = g/cm3
  Dvalue = 1.76
  Group = -> [H_element020,C_element021,O_element019,F_element004,Si_element001]
  conduct = 2
  density = 1
  expand = 3
  formula = G4_C-552
  name = G4_C-552
  specific = 4
FEATURE [App::DocumentObjectGroupPython] Cd_element001  label="Cd_element : 1"  # scripted group (container) (typed FeaturePython)
  n = 1
  ref = Cd_element
FEATURE [App::DocumentObjectGroupPython] Te_element001  label="Te_element : 1"  # scripted group (container) (typed FeaturePython)
  n = 1
  ref = Te_element
FEATURE [App::DocumentObjectGroupPython] G4_CADMIUM_TELLURIDE  # scripted group (container) (typed FeaturePython)
  Dunit = g/cm3
  Dvalue = 6.2
  Group = -> [Cd_element001,Te_element001]
  conduct = 2
  density = 1
  expand = 3
  formula = G4_CADMIUM_TELLURIDE
  name = G4_CADMIUM_TELLURIDE
  specific = 4
FEATURE [App::DocumentObjectGroupPython] Cd_element002  label="Cd_element : 002"  # scripted group (container) (typed FeaturePython)
  n = 1
  ref = Cd_element
FEATURE [App::DocumentObjectGroupPython] W_element001  label="W_element : 1"  # scripted group (container) (typed FeaturePython)
  n = 1
  ref = W_element
FEATURE [App::DocumentObjectGroupPython] O_element020  label="O_element : 008"  # scripted group (container) (typed FeaturePython)
  n = 4
  ref = O_element
FEATURE [App::DocumentObjectGroupPython] G4_CADMIUM_TUNGSTATE  # scripted group (container) (typed FeaturePython)
  Dunit = g/cm3
  Dvalue = 7.9
  Group = -> [Cd_element002,W_element001,O_element020]
  conduct = 2
  density = 1
  expand = 3
  formula = G4_CADMIUM_TUNGSTATE
  name = G4_CADMIUM_TUNGSTATE
  specific = 4
FEATURE [App::DocumentObjectGroupPython] Ca_element005  label="Ca_element : 1"  # scripted group (container) (typed FeaturePython)
  n = 1
  ref = Ca_element
FEATURE [App::DocumentObjectGroupPython] C_element022  label="C_element : 009"  # scripted group (container) (typed FeaturePython)
  n = 1
  ref = C_element
FEATURE [App::DocumentObjectGroupPython] O_element021  label="O_element : 009"  # scripted group (container) (typed FeaturePython)
  n = 3
  ref = O_element
FEATURE [App::DocumentObjectGroupPython] G4_CALCIUM_CARBONATE  # scripted group (container) (typed FeaturePython)
  Dunit = g/cm3
  Dvalue = 2.8
  Group = -> [Ca_element005,C_element022,O_element021]
  conduct = 2
  density = 1
  expand = 3
  formula = G4_CALCIUM_CARBONATE
  name = G4_CALCIUM_CARBONATE
  specific = 4
FEATURE [App::DocumentObjectGroupPython] Ca_element006  label="Ca_element : 002"  # scripted group (container) (typed FeaturePython)
  n = 1
  ref = Ca_element
FEATURE [App::DocumentObjectGroupPython] F_element005  label="F_element : 003"  # scripted group (container) (typed FeaturePython)
  n = 2
  ref = F_element
FEATURE [App::DocumentObjectGroupPython] G4_CALCIUM_FLUORIDE  # scripted group (container) (typed FeaturePython)
  Dunit = g/cm3
  Dvalue = 3.18
  Group = -> [Ca_element006,F_element005]
  conduct = 2
  density = 1
  expand = 3
  formula = G4_CALCIUM_FLUORIDE
  name = G4_CALCIUM_FLUORIDE
  specific = 4
FEATURE [App::DocumentObjectGroupPython] Ca_element007  label="Ca_element : 003"  # scripted group (container) (typed FeaturePython)
  n = 1
  ref = Ca_element
FEATURE [App::DocumentObjectGroupPython] O_element022  label="O_element : 010"  # scripted group (container) (typed FeaturePython)
  n = 1
  ref = O_element
FEATURE [App::DocumentObjectGroupPython] G4_CALCIUM_OXIDE  # scripted group (container) (typed FeaturePython)
  Dunit = g/cm3
  Dvalue = 3.3
  Group = -> [Ca_element007,O_element022]
  conduct = 2
  density = 1
  expand = 3
  formula = G4_CALCIUM_OXIDE
  name = G4_CALCIUM_OXIDE
  specific = 4
FEATURE [App::DocumentObjectGroupPython] Ca_element008  label="Ca_element : 004"  # scripted group (container) (typed FeaturePython)
  n = 1
  ref = Ca_element
FEATURE [App::DocumentObjectGroupPython] S_element007  label="S_element : 002"  # scripted group (container) (typed FeaturePython)
  n = 1
  ref = S_element
FEATURE [App::DocumentObjectGroupPython] O_element023  label="O_element : 011"  # scripted group (container) (typed FeaturePython)
  n = 4
  ref = O_element
FEATURE [App::DocumentObjectGroupPython] G4_CALCIUM_SULFATE  # scripted group (container) (typed FeaturePython)
  Dunit = g/cm3
  Dvalue = 2.96
  Group = -> [Ca_element008,S_element007,O_element023]
  conduct = 2
  density = 1
  expand = 3
  formula = G4_CALCIUM_SULFATE
  name = G4_CALCIUM_SULFATE
  specific = 4
FEATURE [App::DocumentObjectGroupPython] Ca_element009  label="Ca_element : 005"  # scripted group (container) (typed FeaturePython)
  n = 1
  ref = Ca_element
FEATURE [App::DocumentObjectGroupPython] W_element002  label="W_element : 002"  # scripted group (container) (typed FeaturePython)
  n = 1
  ref = W_element
FEATURE [App::DocumentObjectGroupPython] O_element024  label="O_element : 012"  # scripted group (container) (typed FeaturePython)
  n = 4
  ref = O_element
FEATURE [App::DocumentObjectGroupPython] G4_CALCIUM_TUNGSTATE  # scripted group (container) (typed FeaturePython)
  Dunit = g/cm3
  Dvalue = 6.062
  Group = -> [Ca_element009,W_element002,O_element024]
  conduct = 2
  density = 1
  expand = 3
  formula = G4_CALCIUM_TUNGSTATE
  name = G4_CALCIUM_TUNGSTATE
  specific = 4
FEATURE [App::DocumentObjectGroupPython] C_element023  label="C_element : 010"  # scripted group (container) (typed FeaturePython)
  n = 1
  ref = C_element
FEATURE [App::DocumentObjectGroupPython] O_element025  label="O_element : 013"  # scripted group (container) (typed FeaturePython)
  n = 2
  ref = O_element
FEATURE [App::DocumentObjectGroupPython] G4_CARBON_DIOXIDE  # scripted group (container) (typed FeaturePython)
  Dunit = g/cm3
  Dvalue = 0.00184212
  Group = -> [C_element023,O_element025]
  conduct = 2
  density = 1
  expand = 3
  formula = G4_CARBON_DIOXIDE
  name = G4_CARBON_DIOXIDE
  specific = 4
FEATURE [App::DocumentObjectGroupPython] C_element024  label="C_element : 011"  # scripted group (container) (typed FeaturePython)
  n = 1
  ref = C_element
FEATURE [App::DocumentObjectGroupPython] Cl_element004  label="Cl_element : 4"  # scripted group (container) (typed FeaturePython)
  n = 4
  ref = Cl_element
FEATURE [App::DocumentObjectGroupPython] G4_CARBON_TETRACHLORIDE  # scripted group (container) (typed FeaturePython)
  Dunit = g/cm3
  Dvalue = 1.594
  Group = -> [C_element024,Cl_element004]
  conduct = 2
  density = 1
  expand = 3
  formula = G4_CARBON_TETRACHLORIDE
  name = G4_CARBON_TETRACHLORIDE
  specific = 4
FEATURE [App::DocumentObjectGroupPython] C_element025  label="C_element : 012"  # scripted group (container) (typed FeaturePython)
  n = 6
  ref = C_element
FEATURE [App::DocumentObjectGroupPython] H_element021  label="H_element : 012"  # scripted group (container) (typed FeaturePython)
  n = 10
  ref = H_element
FEATURE [App::DocumentObjectGroupPython] O_element026  label="O_element : 5"  # scripted group (container) (typed FeaturePython)
  n = 5
  ref = O_element
FEATURE [App::DocumentObjectGroupPython] G4_CELLULOSE_CELLOPHANE  # scripted group (container) (typed FeaturePython)
  Dunit = g/cm3
  Dvalue = 1.42
  Group = -> [C_element025,H_element021,O_element026]
  conduct = 2
  density = 1
  expand = 3
  formula = G4_CELLULOSE_CELLOPHANE
  name = G4_CELLULOSE_CELLOPHANE
  specific = 4
FEATURE [App::DocumentObjectGroupPython] H_element022  label="H_element : 0.067"  # scripted group (container) (typed FeaturePython)
  n = 0.067125
FEATURE [App::DocumentObjectGroupPython] C_element026  label="C_element : 0.545"  # scripted group (container) (typed FeaturePython)
  n = 0.545403
FEATURE [App::DocumentObjectGroupPython] O_element027  label="O_element : 0.387"  # scripted group (container) (typed FeaturePython)
  n = 0.387472
FEATURE [App::DocumentObjectGroupPython] G4_CELLULOSE_BUTYRATE  # scripted group (container) (typed FeaturePython)
  Dunit = g/cm3
  Dvalue = 1.2
  Group = -> [H_element022,C_element026,O_element027]
  conduct = 2
  density = 1
  expand = 3
  formula = G4_CELLULOSE_BUTYRATE
  name = G4_CELLULOSE_BUTYRATE
  specific = 4
FEATURE [App::DocumentObjectGroupPython] H_element023  label="H_element : 0.029"  # scripted group (container) (typed FeaturePython)
  n = 0.029216
FEATURE [App::DocumentObjectGroupPython] C_element027  label="C_element : 0.271"  # scripted group (container) (typed FeaturePython)
  n = 0.271296
FEATURE [App::DocumentObjectGroupPython] N_element013  label="N_element : 0.121"  # scripted group (container) (typed FeaturePython)
  n = 0.121276
FEATURE [App::DocumentObjectGroupPython] O_element028  label="O_element : 0.578"  # scripted group (container) (typed FeaturePython)
  n = 0.578212
FEATURE [App::DocumentObjectGroupPython] G4_CELLULOSE_NITRATE  # scripted group (container) (typed FeaturePython)
  Dunit = g/cm3
  Dvalue = 1.49
  Group = -> [H_element023,C_element027,N_element013,O_element028]
  conduct = 2
  density = 1
  expand = 3
  formula = G4_CELLULOSE_NITRATE
  name = G4_CELLULOSE_NITRATE
  specific = 4
FEATURE [App::DocumentObjectGroupPython] H_element024  label="H_element : 0.108"  # scripted group (container) (typed FeaturePython)
  n = 0.107596
FEATURE [App::DocumentObjectGroupPython] N_element014  label="N_element : 0.001"  # scripted group (container) (typed FeaturePython)
  n = 0.0008
FEATURE [App::DocumentObjectGroupPython] O_element029  label="O_element : 0.875"  # scripted group (container) (typed FeaturePython)
  n = 0.874976
FEATURE [App::DocumentObjectGroupPython] S_element008  label="S_element : 0.015"  # scripted group (container) (typed FeaturePython)
  n = 0.014627
FEATURE [App::DocumentObjectGroupPython] Ce_element001  label="Ce_element : 0.002"  # scripted group (container) (typed FeaturePython)
  n = 0.002001
FEATURE [App::DocumentObjectGroupPython] G4_CERIC_SULFATE  # scripted group (container) (typed FeaturePython)
  Dunit = g/cm3
  Dvalue = 1.03
  Group = -> [H_element024,N_element014,O_element029,S_element008,Ce_element001]
  conduct = 2
  density = 1
  expand = 3
  formula = G4_CERIC_SULFATE
  name = G4_CERIC_SULFATE
  specific = 4
FEATURE [App::DocumentObjectGroupPython] Cs_element001  label="Cs_element : 1"  # scripted group (container) (typed FeaturePython)
  n = 1
  ref = Cs_element
FEATURE [App::DocumentObjectGroupPython] F_element006  label="F_element : 1"  # scripted group (container) (typed FeaturePython)
  n = 1
  ref = F_element
FEATURE [App::DocumentObjectGroupPython] G4_CESIUM_FLUORIDE  # scripted group (container) (typed FeaturePython)
  Dunit = g/cm3
  Dvalue = 4.115
  Group = -> [Cs_element001,F_element006]
  conduct = 2
  density = 1
  expand = 3
  formula = G4_CESIUM_FLUORIDE
  name = G4_CESIUM_FLUORIDE
  specific = 4
FEATURE [App::DocumentObjectGroupPython] Cs_element002  label="Cs_element : 002"  # scripted group (container) (typed FeaturePython)
  n = 1
  ref = Cs_element
FEATURE [App::DocumentObjectGroupPython] I_element001  label="I_element : 1"  # scripted group (container) (typed FeaturePython)
  n = 1
  ref = I_element
FEATURE [App::DocumentObjectGroupPython] G4_CESIUM_IODIDE  # scripted group (container) (typed FeaturePython)
  Dunit = g/cm3
  Dvalue = 4.51
  Group = -> [Cs_element002,I_element001]
  conduct = 2
  density = 1
  expand = 3
  formula = G4_CESIUM_IODIDE
  name = G4_CESIUM_IODIDE
  specific = 4
FEATURE [App::DocumentObjectGroupPython] C_element028  label="C_element : 013"  # scripted group (container) (typed FeaturePython)
  n = 6
  ref = C_element
FEATURE [App::DocumentObjectGroupPython] H_element025  label="H_element : 013"  # scripted group (container) (typed FeaturePython)
  n = 5
  ref = H_element
FEATURE [App::DocumentObjectGroupPython] Cl_element005  label="Cl_element : 1"  # scripted group (container) (typed FeaturePython)
  n = 1
  ref = Cl_element
FEATURE [App::DocumentObjectGroupPython] G4_CHLOROBENZENE  # scripted group (container) (typed FeaturePython)
  Dunit = g/cm3
  Dvalue = 1.1058
  Group = -> [C_element028,H_element025,Cl_element005]
  conduct = 2
  density = 1
  expand = 3
  formula = G4_CHLOROBENZENE
  name = G4_CHLOROBENZENE
  specific = 4
FEATURE [App::DocumentObjectGroupPython] C_element029  label="C_element : 014"  # scripted group (container) (typed FeaturePython)
  n = 1
  ref = C_element
FEATURE [App::DocumentObjectGroupPython] H_element026  label="H_element : 1"  # scripted group (container) (typed FeaturePython)
  n = 1
  ref = H_element
FEATURE [App::DocumentObjectGroupPython] Cl_element006  label="Cl_element : 3"  # scripted group (container) (typed FeaturePython)
  n = 3
  ref = Cl_element
FEATURE [App::DocumentObjectGroupPython] G4_CHLOROFORM  # scripted group (container) (typed FeaturePython)
  Dunit = g/cm3
  Dvalue = 1.4832
  Group = -> [C_element029,H_element026,Cl_element006]
  conduct = 2
  density = 1
  expand = 3
  formula = G4_CHLOROFORM
  name = G4_CHLOROFORM
  specific = 4
FEATURE [App::DocumentObjectGroupPython] H_element027  label="H_element : 0.010"  # scripted group (container) (typed FeaturePython)
  n = 0.01
FEATURE [App::DocumentObjectGroupPython] C_element030  label="C_element : 0.001"  # scripted group (container) (typed FeaturePython)
  n = 0.001
FEATURE [App::DocumentObjectGroupPython] O_element030  label="O_element : 0.529"  # scripted group (container) (typed FeaturePython)
  n = 0.529107
FEATURE [App::DocumentObjectGroupPython] Na_element005  label="Na_element : 0.016"  # scripted group (container) (typed FeaturePython)
  n = 0.016
FEATURE [App::DocumentObjectGroupPython] Mg_element003  label="Mg_element : 0.004"  # scripted group (container) (typed FeaturePython)
  n = 0.002
FEATURE [App::DocumentObjectGroupPython] Al_element002  label="Al_element : 0.034"  # scripted group (container) (typed FeaturePython)
  n = 0.033872
FEATURE [App::DocumentObjectGroupPython] Si_element002  label="Si_element : 0.337"  # scripted group (container) (typed FeaturePython)
  n = 0.337021
FEATURE [App::DocumentObjectGroupPython] K_element003  label="K_element : 0.013"  # scripted group (container) (typed FeaturePython)
  n = 0.013
FEATURE [App::DocumentObjectGroupPython] Ca_element010  label="Ca_element : 0.044"  # scripted group (container) (typed FeaturePython)
  n = 0.044
FEATURE [App::DocumentObjectGroupPython] Fe_element002  label="Fe_element : 0.014"  # scripted group (container) (typed FeaturePython)
  n = 0.014
FEATURE [App::DocumentObjectGroupPython] G4_CONCRETE  # scripted group (container) (typed FeaturePython)
  Dunit = g/cm3
  Dvalue = 2.3
  Group = -> [H_element027,C_element030,O_element030,Na_element005,Mg_element003,Al_element002,Si_element002,K_element003,Ca_element010,Fe_element002]
  conduct = 2
  density = 1
  expand = 3
  formula = G4_CONCRETE
  name = G4_CONCRETE
  specific = 4
FEATURE [App::DocumentObjectGroupPython] C_element031  label="C_element : 015"  # scripted group (container) (typed FeaturePython)
  n = 6
  ref = C_element
FEATURE [App::DocumentObjectGroupPython] H_element028  label="H_element : 12"  # scripted group (container) (typed FeaturePython)
  n = 12
  ref = H_element
FEATURE [App::DocumentObjectGroupPython] G4_CYCLOHEXANE  # scripted group (container) (typed FeaturePython)
  Dunit = g/cm3
  Dvalue = 0.779
  Group = -> [C_element031,H_element028]
  conduct = 2
  density = 1
  expand = 3
  formula = G4_CYCLOHEXANE
  name = G4_CYCLOHEXANE
  specific = 4
FEATURE [App::DocumentObjectGroupPython] C_element032  label="C_element : 016"  # scripted group (container) (typed FeaturePython)
  n = 6
  ref = C_element
FEATURE [App::DocumentObjectGroupPython] H_element029  label="H_element : 4"  # scripted group (container) (typed FeaturePython)
  n = 4
  ref = H_element
FEATURE [App::DocumentObjectGroupPython] Cl_element007  label="Cl_element : 2"  # scripted group (container) (typed FeaturePython)
  n = 2
  ref = Cl_element
FEATURE [App::DocumentObjectGroupPython] G4_1_2_DICHLOROBENZENE  label="G4_1.2-DICHLOROBENZENE"  # scripted group (container) (typed FeaturePython)
  Dunit = g/cm3
  Dvalue = 1.3048
  Group = -> [C_element032,H_element029,Cl_element007]
  conduct = 2
  density = 1
  expand = 3
  formula = G4_1.2-DICHLOROBENZENE
  name = G4_1.2-DICHLOROBENZENE
  specific = 4
FEATURE [App::DocumentObjectGroupPython] C_element033  label="C_element : 017"  # scripted group (container) (typed FeaturePython)
  n = 4
  ref = C_element
FEATURE [App::DocumentObjectGroupPython] H_element030  label="H_element : 8"  # scripted group (container) (typed FeaturePython)
  n = 8
  ref = H_element
FEATURE [App::DocumentObjectGroupPython] O_element031  label="O_element : 014"  # scripted group (container) (typed FeaturePython)
  n = 1
  ref = O_element
FEATURE [App::DocumentObjectGroupPython] Cl_element008  label="Cl_element : 005"  # scripted group (container) (typed FeaturePython)
  n = 2
  ref = Cl_element
FEATURE [App::DocumentObjectGroupPython] G4_DICHLORODIETHYL_ETHER  # scripted group (container) (typed FeaturePython)
  Dunit = g/cm3
  Dvalue = 1.2199
  Group = -> [C_element033,H_element030,O_element031,Cl_element008]
  conduct = 2
  density = 1
  expand = 3
  formula = G4_DICHLORODIETHYL_ETHER
  name = G4_DICHLORODIETHYL_ETHER
  specific = 4
FEATURE [App::DocumentObjectGroupPython] C_element034  label="C_element : 018"  # scripted group (container) (typed FeaturePython)
  n = 2
  ref = C_element
FEATURE [App::DocumentObjectGroupPython] H_element031  label="H_element : 014"  # scripted group (container) (typed FeaturePython)
  n = 4
  ref = H_element
FEATURE [App::DocumentObjectGroupPython] Cl_element009  label="Cl_element : 006"  # scripted group (container) (typed FeaturePython)
  n = 2
  ref = Cl_element
FEATURE [App::DocumentObjectGroupPython] G4_1_2_DICHLOROETHANE  label="G4_1.2-DICHLOROETHANE"  # scripted group (container) (typed FeaturePython)
  Dunit = g/cm3
  Dvalue = 1.2351
  Group = -> [C_element034,H_element031,Cl_element009]
  conduct = 2
  density = 1
  expand = 3
  formula = G4_1.2-DICHLOROETHANE
  name = G4_1.2-DICHLOROETHANE
  specific = 4
FEATURE [App::DocumentObjectGroupPython] C_element035  label="C_element : 019"  # scripted group (container) (typed FeaturePython)
  n = 4
  ref = C_element
FEATURE [App::DocumentObjectGroupPython] H_element032  label="H_element : 015"  # scripted group (container) (typed FeaturePython)
  n = 10
  ref = H_element
FEATURE [App::DocumentObjectGroupPython] O_element032  label="O_element : 015"  # scripted group (container) (typed FeaturePython)
  n = 1
  ref = O_element
FEATURE [App::DocumentObjectGroupPython] G4_DIETHYL_ETHER  # scripted group (container) (typed FeaturePython)
  Dunit = g/cm3
  Dvalue = 0.71378
  Group = -> [C_element035,H_element032,O_element032]
  conduct = 2
  density = 1
  expand = 3
  formula = G4_DIETHYL_ETHER
  name = G4_DIETHYL_ETHER
  specific = 4
FEATURE [App::DocumentObjectGroupPython] C_element036  label="C_element : 020"  # scripted group (container) (typed FeaturePython)
  n = 3
  ref = C_element
FEATURE [App::DocumentObjectGroupPython] H_element033  label="H_element : 016"  # scripted group (container) (typed FeaturePython)
  n = 7
  ref = H_element
FEATURE [App::DocumentObjectGroupPython] N_element015  label="N_element : 008"  # scripted group (container) (typed FeaturePython)
  n = 1
  ref = N_element
FEATURE [App::DocumentObjectGroupPython] O_element033  label="O_element : 016"  # scripted group (container) (typed FeaturePython)
  n = 1
  ref = O_element
FEATURE [App::DocumentObjectGroupPython] G4_N_N_DIMETHYL_FORMAMIDE  label="G4_N.N-DIMETHYL_FORMAMIDE"  # scripted group (container) (typed FeaturePython)
  Dunit = g/cm3
  Dvalue = 0.9487
  Group = -> [C_element036,H_element033,N_element015,O_element033]
  conduct = 2
  density = 1
  expand = 3
  formula = G4_N.N-DIMETHYL_FORMAMIDE
  name = G4_N.N-DIMETHYL_FORMAMIDE
  specific = 4
FEATURE [App::DocumentObjectGroupPython] C_element037  label="C_element : 021"  # scripted group (container) (typed FeaturePython)
  n = 2
  ref = C_element
FEATURE [App::DocumentObjectGroupPython] H_element034  label="H_element : 017"  # scripted group (container) (typed FeaturePython)
  n = 6
  ref = H_element
FEATURE [App::DocumentObjectGroupPython] O_element034  label="O_element : 017"  # scripted group (container) (typed FeaturePython)
  n = 1
  ref = O_element
FEATURE [App::DocumentObjectGroupPython] S_element009  label="S_element : 003"  # scripted group (container) (typed FeaturePython)
  n = 1
  ref = S_element
FEATURE [App::DocumentObjectGroupPython] G4_DIMETHYL_SULFOXIDE  # scripted group (container) (typed FeaturePython)
  Dunit = g/cm3
  Dvalue = 1.1014
  Group = -> [C_element037,H_element034,O_element034,S_element009]
  conduct = 2
  density = 1
  expand = 3
  formula = G4_DIMETHYL_SULFOXIDE
  name = G4_DIMETHYL_SULFOXIDE
  specific = 4
FEATURE [App::DocumentObjectGroupPython] C_element038  label="C_element : 022"  # scripted group (container) (typed FeaturePython)
  n = 2
  ref = C_element
FEATURE [App::DocumentObjectGroupPython] H_element035  label="H_element : 018"  # scripted group (container) (typed FeaturePython)
  n = 6
  ref = H_element
FEATURE [App::DocumentObjectGroupPython] G4_ETHANE  # scripted group (container) (typed FeaturePython)
  Dunit = g/cm3
  Dvalue = 0.00125324
  Group = -> [C_element038,H_element035]
  conduct = 2
  density = 1
  expand = 3
  formula = G4_ETHANE
  name = G4_ETHANE
  specific = 4
FEATURE [App::DocumentObjectGroupPython] C_element039  label="C_element : 023"  # scripted group (container) (typed FeaturePython)
  n = 2
  ref = C_element
FEATURE [App::DocumentObjectGroupPython] H_element036  label="H_element : 019"  # scripted group (container) (typed FeaturePython)
  n = 6
  ref = H_element
FEATURE [App::DocumentObjectGroupPython] O_element035  label="O_element : 018"  # scripted group (container) (typed FeaturePython)
  n = 1
  ref = O_element
FEATURE [App::DocumentObjectGroupPython] G4_ETHYL_ALCOHOL  # scripted group (container) (typed FeaturePython)
  Dunit = g/cm3
  Dvalue = 0.7893
  Group = -> [C_element039,H_element036,O_element035]
  conduct = 2
  density = 1
  expand = 3
  formula = G4_ETHYL_ALCOHOL
  name = G4_ETHYL_ALCOHOL
  specific = 4
FEATURE [App::DocumentObjectGroupPython] H_element037  label="H_element : 0.090"  # scripted group (container) (typed FeaturePython)
  n = 0.090027
FEATURE [App::DocumentObjectGroupPython] C_element040  label="C_element : 0.585"  # scripted group (container) (typed FeaturePython)
  n = 0.585182
FEATURE [App::DocumentObjectGroupPython] O_element036  label="O_element : 0.325"  # scripted group (container) (typed FeaturePython)
  n = 0.324791
FEATURE [App::DocumentObjectGroupPython] G4_ETHYL_CELLULOSE  # scripted group (container) (typed FeaturePython)
  Dunit = g/cm3
  Dvalue = 1.13
  Group = -> [H_element037,C_element040,O_element036]
  conduct = 2
  density = 1
  expand = 3
  formula = G4_ETHYL_CELLULOSE
  name = G4_ETHYL_CELLULOSE
  specific = 4
FEATURE [App::DocumentObjectGroupPython] C_element041  label="C_element : 024"  # scripted group (container) (typed FeaturePython)
  n = 2
  ref = C_element
FEATURE [App::DocumentObjectGroupPython] H_element038  label="H_element : 020"  # scripted group (container) (typed FeaturePython)
  n = 4
  ref = H_element
FEATURE [App::DocumentObjectGroupPython] G4_ETHYLENE  # scripted group (container) (typed FeaturePython)
  Dunit = g/cm3
  Dvalue = 0.00117497
  Group = -> [C_element041,H_element038]
  conduct = 2
  density = 1
  expand = 3
  formula = G4_ETHYLENE
  name = G4_ETHYLENE
  specific = 4
FEATURE [App::DocumentObjectGroupPython] H_element039  label="H_element : 0.096"  # scripted group (container) (typed FeaturePython)
  n = 0.096
FEATURE [App::DocumentObjectGroupPython] C_element042  label="C_element : 0.195"  # scripted group (container) (typed FeaturePython)
  n = 0.195
FEATURE [App::DocumentObjectGroupPython] N_element016  label="N_element : 0.057"  # scripted group (container) (typed FeaturePython)
  n = 0.057
FEATURE [App::DocumentObjectGroupPython] O_element037  label="O_element : 0.646"  # scripted group (container) (typed FeaturePython)
  n = 0.646
FEATURE [App::DocumentObjectGroupPython] Na_element006  label="Na_element : 0.017"  # scripted group (container) (typed FeaturePython)
  n = 0.001
FEATURE [App::DocumentObjectGroupPython] P_element005  label="P_element : 0.104"  # scripted group (container) (typed FeaturePython)
  n = 0.001
FEATURE [App::DocumentObjectGroupPython] S_element010  label="S_element : 0.016"  # scripted group (container) (typed FeaturePython)
  n = 0.003
FEATURE [App::DocumentObjectGroupPython] Cl_element010  label="Cl_element : 0.005"  # scripted group (container) (typed FeaturePython)
  n = 0.001
FEATURE [App::DocumentObjectGroupPython] G4_EYE_LENS_ICRP  # scripted group (container) (typed FeaturePython)
  Dunit = g/cm3
  Dvalue = 1.07
  Group = -> [H_element039,C_element042,N_element016,O_element037,Na_element006,P_element005,S_element010,Cl_element010]
  conduct = 2
  density = 1
  expand = 3
  formula = G4_EYE_LENS_ICRP
  name = G4_EYE_LENS_ICRP
  specific = 4
FEATURE [App::DocumentObjectGroupPython] Fe_element003  label="Fe_element : 2"  # scripted group (container) (typed FeaturePython)
  n = 2
  ref = Fe_element
FEATURE [App::DocumentObjectGroupPython] O_element038  label="O_element : 019"  # scripted group (container) (typed FeaturePython)
  n = 3
  ref = O_element
FEATURE [App::DocumentObjectGroupPython] G4_FERRIC_OXIDE  # scripted group (container) (typed FeaturePython)
  Dunit = g/cm3
  Dvalue = 5.2
  Group = -> [Fe_element003,O_element038]
  conduct = 2
  density = 1
  expand = 3
  formula = G4_FERRIC_OXIDE
  name = G4_FERRIC_OXIDE
  specific = 4
FEATURE [App::DocumentObjectGroupPython] Fe_element004  label="Fe_element : 1"  # scripted group (container) (typed FeaturePython)
  n = 1
  ref = Fe_element
FEATURE [App::DocumentObjectGroupPython] B_element003  label="B_element : 1"  # scripted group (container) (typed FeaturePython)
  n = 1
  ref = B_element
FEATURE [App::DocumentObjectGroupPython] G4_FERROBORIDE  # scripted group (container) (typed FeaturePython)
  Dunit = g/cm3
  Dvalue = 7.15
  Group = -> [Fe_element004,B_element003]
  conduct = 2
  density = 1
  expand = 3
  formula = G4_FERROBORIDE
  name = G4_FERROBORIDE
  specific = 4
FEATURE [App::DocumentObjectGroupPython] Fe_element005  label="Fe_element : 003"  # scripted group (container) (typed FeaturePython)
  n = 1
  ref = Fe_element
FEATURE [App::DocumentObjectGroupPython] O_element039  label="O_element : 020"  # scripted group (container) (typed FeaturePython)
  n = 1
  ref = O_element
FEATURE [App::DocumentObjectGroupPython] G4_FERROUS_OXIDE  # scripted group (container) (typed FeaturePython)
  Dunit = g/cm3
  Dvalue = 5.7
  Group = -> [Fe_element005,O_element039]
  conduct = 2
  density = 1
  expand = 3
  formula = G4_FERROUS_OXIDE
  name = G4_FERROUS_OXIDE
  specific = 4
FEATURE [App::DocumentObjectGroupPython] H_element040  label="H_element : 0.115"  # scripted group (container) (typed FeaturePython)
  n = 0.108259
FEATURE [App::DocumentObjectGroupPython] N_element017  label="N_element : 0.000"  # scripted group (container) (typed FeaturePython)
  n = 2.7e-05
FEATURE [App::DocumentObjectGroupPython] O_element040  label="O_element : 0.879"  # scripted group (container) (typed FeaturePython)
  n = 0.878636
FEATURE [App::DocumentObjectGroupPython] Na_element007  label="Na_element : 0.000"  # scripted group (container) (typed FeaturePython)
  n = 2.2e-05
FEATURE [App::DocumentObjectGroupPython] S_element011  label="S_element : 0.013"  # scripted group (container) (typed FeaturePython)
  n = 0.012968
FEATURE [App::DocumentObjectGroupPython] Cl_element011  label="Cl_element : 0.000"  # scripted group (container) (typed FeaturePython)
  n = 3.4e-05
FEATURE [App::DocumentObjectGroupPython] Fe_element006  label="Fe_element : 0.000"  # scripted group (container) (typed FeaturePython)
  n = 5.4e-05
FEATURE [App::DocumentObjectGroupPython] G4_FERROUS_SULFATE  # scripted group (container) (typed FeaturePython)
  Dunit = g/cm3
  Dvalue = 1.024
  Group = -> [H_element040,N_element017,O_element040,Na_element007,S_element011,Cl_element011,Fe_element006]
  conduct = 2
  density = 1
  expand = 3
  formula = G4_FERROUS_SULFATE
  name = G4_FERROUS_SULFATE
  specific = 4
FEATURE [App::DocumentObjectGroupPython] C_element043  label="C_element : 0.099"  # scripted group (container) (typed FeaturePython)
  n = 0.099335
FEATURE [App::DocumentObjectGroupPython] F_element007  label="F_element : 0.314"  # scripted group (container) (typed FeaturePython)
  n = 0.314247
FEATURE [App::DocumentObjectGroupPython] Cl_element012  label="Cl_element : 0.586"  # scripted group (container) (typed FeaturePython)
  n = 0.586418
FEATURE [App::DocumentObjectGroupPython] G4_FREON_12  label="G4_FREON-12"  # scripted group (container) (typed FeaturePython)
  Dunit = g/cm3
  Dvalue = 1.12
  Group = -> [C_element043,F_element007,Cl_element012]
  conduct = 2
  density = 1
  expand = 3
  formula = G4_FREON-12
  name = G4_FREON-12
  specific = 4
FEATURE [App::DocumentObjectGroupPython] C_element044  label="C_element : 0.057"  # scripted group (container) (typed FeaturePython)
  n = 0.057245
FEATURE [App::DocumentObjectGroupPython] F_element008  label="F_element : 0.181"  # scripted group (container) (typed FeaturePython)
  n = 0.181096
FEATURE [App::DocumentObjectGroupPython] Br_element001  label="Br_element : 0.762"  # scripted group (container) (typed FeaturePython)
  n = 0.761659
FEATURE [App::DocumentObjectGroupPython] G4_FREON_12B2  label="G4_FREON-12B2"  # scripted group (container) (typed FeaturePython)
  Dunit = g/cm3
  Dvalue = 1.8
  Group = -> [C_element044,F_element008,Br_element001]
  conduct = 2
  density = 1
  expand = 3
  formula = G4_FREON-12B2
  name = G4_FREON-12B2
  specific = 4
FEATURE [App::DocumentObjectGroupPython] C_element045  label="C_element : 0.115"  # scripted group (container) (typed FeaturePython)
  n = 0.114983
FEATURE [App::DocumentObjectGroupPython] F_element009  label="F_element : 0.546"  # scripted group (container) (typed FeaturePython)
  n = 0.545621
FEATURE [App::DocumentObjectGroupPython] Cl_element013  label="Cl_element : 0.339"  # scripted group (container) (typed FeaturePython)
  n = 0.339396
FEATURE [App::DocumentObjectGroupPython] G4_FREON_13  label="G4_FREON-13"  # scripted group (container) (typed FeaturePython)
  Dunit = g/cm3
  Dvalue = 0.95
  Group = -> [C_element045,F_element009,Cl_element013]
  conduct = 2
  density = 1
  expand = 3
  formula = G4_FREON-13
  name = G4_FREON-13
  specific = 4
FEATURE [App::DocumentObjectGroupPython] C_element046  label="C_element : 025"  # scripted group (container) (typed FeaturePython)
  n = 1
  ref = C_element
FEATURE [App::DocumentObjectGroupPython] F_element010  label="F_element : 3"  # scripted group (container) (typed FeaturePython)
  n = 3
  ref = F_element
FEATURE [App::DocumentObjectGroupPython] Br_element002  label="Br_element : 1"  # scripted group (container) (typed FeaturePython)
  n = 1
  ref = Br_element
FEATURE [App::DocumentObjectGroupPython] G4_FREON_13B1  label="G4_FREON-13B1"  # scripted group (container) (typed FeaturePython)
  Dunit = g/cm3
  Dvalue = 1.5
  Group = -> [C_element046,F_element010,Br_element002]
  conduct = 2
  density = 1
  expand = 3
  formula = G4_FREON-13B1
  name = G4_FREON-13B1
  specific = 4
FEATURE [App::DocumentObjectGroupPython] C_element047  label="C_element : 0.061"  # scripted group (container) (typed FeaturePython)
  n = 0.061309
FEATURE [App::DocumentObjectGroupPython] F_element011  label="F_element : 0.291"  # scripted group (container) (typed FeaturePython)
  n = 0.290924
FEATURE [App::DocumentObjectGroupPython] I_element002  label="I_element : 0.648"  # scripted group (container) (typed FeaturePython)
  n = 0.647767
FEATURE [App::DocumentObjectGroupPython] G4_FREON_13I1  label="G4_FREON-13I1"  # scripted group (container) (typed FeaturePython)
  Dunit = g/cm3
  Dvalue = 1.8
  Group = -> [C_element047,F_element011,I_element002]
  conduct = 2
  density = 1
  expand = 3
  formula = G4_FREON-13I1
  name = G4_FREON-13I1
  specific = 4
FEATURE [App::DocumentObjectGroupPython] Gd_element001  label="Gd_element : 2"  # scripted group (container) (typed FeaturePython)
  n = 2
  ref = Gd_element
FEATURE [App::DocumentObjectGroupPython] O_element041  label="O_element : 021"  # scripted group (container) (typed FeaturePython)
  n = 2
  ref = O_element
FEATURE [App::DocumentObjectGroupPython] S_element012  label="S_element : 004"  # scripted group (container) (typed FeaturePython)
  n = 1
  ref = S_element
FEATURE [App::DocumentObjectGroupPython] G4_GADOLINIUM_OXYSULFIDE  # scripted group (container) (typed FeaturePython)
  Dunit = g/cm3
  Dvalue = 7.44
  Group = -> [Gd_element001,O_element041,S_element012]
  conduct = 2
  density = 1
  expand = 3
  formula = G4_GADOLINIUM_OXYSULFIDE
  name = G4_GADOLINIUM_OXYSULFIDE
  specific = 4
FEATURE [App::DocumentObjectGroupPython] Ga_element001  label="Ga_element : 1"  # scripted group (container) (typed FeaturePython)
  n = 1
  ref = Ga_element
FEATURE [App::DocumentObjectGroupPython] As_element001  label="As_element : 1"  # scripted group (container) (typed FeaturePython)
  n = 1
  ref = As_element
FEATURE [App::DocumentObjectGroupPython] G4_GALLIUM_ARSENIDE  # scripted group (container) (typed FeaturePython)
  Dunit = g/cm3
  Dvalue = 5.31
  Group = -> [Ga_element001,As_element001]
  conduct = 2
  density = 1
  expand = 3
  formula = G4_GALLIUM_ARSENIDE
  name = G4_GALLIUM_ARSENIDE
  specific = 4
FEATURE [App::DocumentObjectGroupPython] H_element041  label="H_element : 0.081"  # scripted group (container) (typed FeaturePython)
  n = 0.08118
FEATURE [App::DocumentObjectGroupPython] C_element048  label="C_element : 0.416"  # scripted group (container) (typed FeaturePython)
  n = 0.41606
FEATURE [App::DocumentObjectGroupPython] N_element018  label="N_element : 0.111"  # scripted group (container) (typed FeaturePython)
  n = 0.11124
FEATURE [App::DocumentObjectGroupPython] O_element042  label="O_element : 0.381"  # scripted group (container) (typed FeaturePython)
  n = 0.38064
FEATURE [App::DocumentObjectGroupPython] S_element013  label="S_element : 0.011"  # scripted group (container) (typed FeaturePython)
  n = 0.01088
FEATURE [App::DocumentObjectGroupPython] G4_GEL_PHOTO_EMULSION  # scripted group (container) (typed FeaturePython)
  Dunit = g/cm3
  Dvalue = 1.2914
  Group = -> [H_element041,C_element048,N_element018,O_element042,S_element013]
  conduct = 2
  density = 1
  expand = 3
  formula = G4_GEL_PHOTO_EMULSION
  name = G4_GEL_PHOTO_EMULSION
  specific = 4
FEATURE [App::DocumentObjectGroupPython] B_element004  label="B_element : 0.040"  # scripted group (container) (typed FeaturePython)
  n = 0.0400639
FEATURE [App::DocumentObjectGroupPython] O_element043  label="O_element : 0.540"  # scripted group (container) (typed FeaturePython)
  n = 0.539561
FEATURE [App::DocumentObjectGroupPython] Na_element008  label="Na_element : 0.028"  # scripted group (container) (typed FeaturePython)
  n = 0.0281909
FEATURE [App::DocumentObjectGroupPython] Al_element003  label="Al_element : 0.012"  # scripted group (container) (typed FeaturePython)
  n = 0.011644
FEATURE [App::DocumentObjectGroupPython] Si_element003  label="Si_element : 0.377"  # scripted group (container) (typed FeaturePython)
  n = 0.377219
FEATURE [App::DocumentObjectGroupPython] K_element004  label="K_element : 0.014"  # scripted group (container) (typed FeaturePython)
  n = 0.00332099
FEATURE [App::DocumentObjectGroupPython] G4_Pyrex_Glass  # scripted group (container) (typed FeaturePython)
  Dunit = g/cm3
  Dvalue = 2.23
  Group = -> [B_element004,O_element043,Na_element008,Al_element003,Si_element003,K_element004]
  conduct = 2
  density = 1
  expand = 3
  formula = G4_Pyrex_Glass
  name = G4_Pyrex_Glass
  specific = 4
FEATURE [App::DocumentObjectGroupPython] O_element044  label="O_element : 0.156"  # scripted group (container) (typed FeaturePython)
  n = 0.156453
FEATURE [App::DocumentObjectGroupPython] Si_element004  label="Si_element : 0.081"  # scripted group (container) (typed FeaturePython)
  n = 0.080866
FEATURE [App::DocumentObjectGroupPython] Ti_element001  label="Ti_element : 0.008"  # scripted group (container) (typed FeaturePython)
  n = 0.008092
FEATURE [App::DocumentObjectGroupPython] As_element002  label="As_element : 0.003"  # scripted group (container) (typed FeaturePython)
  n = 0.002651
FEATURE [App::DocumentObjectGroupPython] Pb_element001  label="Pb_element : 0.752"  # scripted group (container) (typed FeaturePython)
  n = 0.751938
FEATURE [App::DocumentObjectGroupPython] G4_GLASS_LEAD  # scripted group (container) (typed FeaturePython)
  Dunit = g/cm3
  Dvalue = 6.22
  Group = -> [O_element044,Si_element004,Ti_element001,As_element002,Pb_element001]
  conduct = 2
  density = 1
  expand = 3
  formula = G4_GLASS_LEAD
  name = G4_GLASS_LEAD
  specific = 4
FEATURE [App::DocumentObjectGroupPython] O_element045  label="O_element : 0.460"  # scripted group (container) (typed FeaturePython)
  n = 0.4598
FEATURE [App::DocumentObjectGroupPython] Na_element009  label="Na_element : 0.096"  # scripted group (container) (typed FeaturePython)
  n = 0.0964411
FEATURE [App::DocumentObjectGroupPython] Si_element005  label="Si_element : 0.378"  # scripted group (container) (typed FeaturePython)
  n = 0.336553
FEATURE [App::DocumentObjectGroupPython] Ca_element011  label="Ca_element : 0.107"  # scripted group (container) (typed FeaturePython)
  n = 0.107205
FEATURE [App::DocumentObjectGroupPython] G4_GLASS_PLATE  # scripted group (container) (typed FeaturePython)
  Dunit = g/cm3
  Dvalue = 2.4
  Group = -> [O_element045,Na_element009,Si_element005,Ca_element011]
  conduct = 2
  density = 1
  expand = 3
  formula = G4_GLASS_PLATE
  name = G4_GLASS_PLATE
  specific = 4
FEATURE [App::DocumentObjectGroupPython] C_element049  label="C_element : 026"  # scripted group (container) (typed FeaturePython)
  n = 5
  ref = C_element
FEATURE [App::DocumentObjectGroupPython] H_element042  label="H_element : 021"  # scripted group (container) (typed FeaturePython)
  n = 10
  ref = H_element
FEATURE [App::DocumentObjectGroupPython] N_element019  label="N_element : 2"  # scripted group (container) (typed FeaturePython)
  n = 2
  ref = N_element
FEATURE [App::DocumentObjectGroupPython] O_element046  label="O_element : 022"  # scripted group (container) (typed FeaturePython)
  n = 3
  ref = O_element
FEATURE [App::DocumentObjectGroupPython] G4_GLUTAMINE  # scripted group (container) (typed FeaturePython)
  Dunit = g/cm3
  Dvalue = 1.46
  Group = -> [C_element049,H_element042,N_element019,O_element046]
  conduct = 2
  density = 1
  expand = 3
  formula = G4_GLUTAMINE
  name = G4_GLUTAMINE
  specific = 4
FEATURE [App::DocumentObjectGroupPython] C_element050  label="C_element : 027"  # scripted group (container) (typed FeaturePython)
  n = 3
  ref = C_element
FEATURE [App::DocumentObjectGroupPython] H_element043  label="H_element : 022"  # scripted group (container) (typed FeaturePython)
  n = 8
  ref = H_element
FEATURE [App::DocumentObjectGroupPython] O_element047  label="O_element : 023"  # scripted group (container) (typed FeaturePython)
  n = 3
  ref = O_element
FEATURE [App::DocumentObjectGroupPython] G4_GLYCEROL  # scripted group (container) (typed FeaturePython)
  Dunit = g/cm3
  Dvalue = 1.2613
  Group = -> [C_element050,H_element043,O_element047]
  conduct = 2
  density = 1
  expand = 3
  formula = G4_GLYCEROL
  name = G4_GLYCEROL
  specific = 4
FEATURE [App::DocumentObjectGroupPython] C_element051  label="C_element : 028"  # scripted group (container) (typed FeaturePython)
  n = 5
  ref = C_element
FEATURE [App::DocumentObjectGroupPython] H_element044  label="H_element : 023"  # scripted group (container) (typed FeaturePython)
  n = 5
  ref = H_element
FEATURE [App::DocumentObjectGroupPython] N_element020  label="N_element : 009"  # scripted group (container) (typed FeaturePython)
  n = 5
  ref = N_element
FEATURE [App::DocumentObjectGroupPython] O_element048  label="O_element : 024"  # scripted group (container) (typed FeaturePython)
  n = 1
  ref = O_element
FEATURE [App::DocumentObjectGroupPython] G4_GUANINE  # scripted group (container) (typed FeaturePython)
  Dunit = g/cm3
  Dvalue = 2.2
  Group = -> [C_element051,H_element044,N_element020,O_element048]
  conduct = 2
  density = 1
  expand = 3
  formula = G4_GUANINE
  name = G4_GUANINE
  specific = 4
FEATURE [App::DocumentObjectGroupPython] Ca_element012  label="Ca_element : 006"  # scripted group (container) (typed FeaturePython)
  n = 1
  ref = Ca_element
FEATURE [App::DocumentObjectGroupPython] S_element014  label="S_element : 005"  # scripted group (container) (typed FeaturePython)
  n = 1
  ref = S_element
FEATURE [App::DocumentObjectGroupPython] O_element049  label="O_element : 6"  # scripted group (container) (typed FeaturePython)
  n = 6
  ref = O_element
FEATURE [App::DocumentObjectGroupPython] H_element045  label="H_element : 024"  # scripted group (container) (typed FeaturePython)
  n = 4
  ref = H_element
FEATURE [App::DocumentObjectGroupPython] G4_GYPSUM  # scripted group (container) (typed FeaturePython)
  Dunit = g/cm3
  Dvalue = 2.32
  Group = -> [Ca_element012,S_element014,O_element049,H_element045]
  conduct = 2
  density = 1
  expand = 3
  formula = G4_GYPSUM
  name = G4_GYPSUM
  specific = 4
FEATURE [App::DocumentObjectGroupPython] C_element052  label="C_element : 7"  # scripted group (container) (typed FeaturePython)
  n = 7
  ref = C_element
FEATURE [App::DocumentObjectGroupPython] H_element046  label="H_element : 16"  # scripted group (container) (typed FeaturePython)
  n = 16
  ref = H_element
FEATURE [App::DocumentObjectGroupPython] G4_N_HEPTANE  label="G4_N-HEPTANE"  # scripted group (container) (typed FeaturePython)
  Dunit = g/cm3
  Dvalue = 0.68376
  Group = -> [C_element052,H_element046]
  conduct = 2
  density = 1
  expand = 3
  formula = G4_N-HEPTANE
  name = G4_N-HEPTANE
  specific = 4
FEATURE [App::DocumentObjectGroupPython] C_element053  label="C_element : 029"  # scripted group (container) (typed FeaturePython)
  n = 6
  ref = C_element
FEATURE [App::DocumentObjectGroupPython] H_element047  label="H_element : 14"  # scripted group (container) (typed FeaturePython)
  n = 14
  ref = H_element
FEATURE [App::DocumentObjectGroupPython] G4_N_HEXANE  label="G4_N-HEXANE"  # scripted group (container) (typed FeaturePython)
  Dunit = g/cm3
  Dvalue = 0.6603
  Group = -> [C_element053,H_element047]
  conduct = 2
  density = 1
  expand = 3
  formula = G4_N-HEXANE
  name = G4_N-HEXANE
  specific = 4
FEATURE [App::DocumentObjectGroupPython] C_element054  label="C_element : 22"  # scripted group (container) (typed FeaturePython)
  n = 22
  ref = C_element
FEATURE [App::DocumentObjectGroupPython] H_element048  label="H_element : 025"  # scripted group (container) (typed FeaturePython)
  n = 10
  ref = H_element
FEATURE [App::DocumentObjectGroupPython] N_element021  label="N_element : 010"  # scripted group (container) (typed FeaturePython)
  n = 2
  ref = N_element
FEATURE [App::DocumentObjectGroupPython] O_element050  label="O_element : 025"  # scripted group (container) (typed FeaturePython)
  n = 5
  ref = O_element
FEATURE [App::DocumentObjectGroupPython] G4_KAPTON  # scripted group (container) (typed FeaturePython)
  Dunit = g/cm3
  Dvalue = 1.42
  Group = -> [C_element054,H_element048,N_element021,O_element050]
  conduct = 2
  density = 1
  expand = 3
  formula = G4_KAPTON
  name = G4_KAPTON
  specific = 4
FEATURE [App::DocumentObjectGroupPython] La_element001  label="La_element : 1"  # scripted group (container) (typed FeaturePython)
  n = 1
  ref = La_element
FEATURE [App::DocumentObjectGroupPython] Br_element003  label="Br_element : 002"  # scripted group (container) (typed FeaturePython)
  n = 1
  ref = Br_element
FEATURE [App::DocumentObjectGroupPython] O_element051  label="O_element : 026"  # scripted group (container) (typed FeaturePython)
  n = 1
  ref = O_element
FEATURE [App::DocumentObjectGroupPython] G4_LANTHANUM_OXYBROMIDE  # scripted group (container) (typed FeaturePython)
  Dunit = g/cm3
  Dvalue = 6.28
  Group = -> [La_element001,Br_element003,O_element051]
  conduct = 2
  density = 1
  expand = 3
  formula = G4_LANTHANUM_OXYBROMIDE
  name = G4_LANTHANUM_OXYBROMIDE
  specific = 4
FEATURE [App::DocumentObjectGroupPython] La_element002  label="La_element : 2"  # scripted group (container) (typed FeaturePython)
  n = 2
  ref = La_element
FEATURE [App::DocumentObjectGroupPython] O_element052  label="O_element : 027"  # scripted group (container) (typed FeaturePython)
  n = 2
  ref = O_element
FEATURE [App::DocumentObjectGroupPython] S_element015  label="S_element : 006"  # scripted group (container) (typed FeaturePython)
  n = 1
  ref = S_element
FEATURE [App::DocumentObjectGroupPython] G4_LANTHANUM_OXYSULFIDE  # scripted group (container) (typed FeaturePython)
  Dunit = g/cm3
  Dvalue = 5.86
  Group = -> [La_element002,O_element052,S_element015]
  conduct = 2
  density = 1
  expand = 3
  formula = G4_LANTHANUM_OXYSULFIDE
  name = G4_LANTHANUM_OXYSULFIDE
  specific = 4
FEATURE [App::DocumentObjectGroupPython] O_element053  label="O_element : 0.072"  # scripted group (container) (typed FeaturePython)
  n = 0.071682
FEATURE [App::DocumentObjectGroupPython] Pb_element002  label="Pb_element : 0.928"  # scripted group (container) (typed FeaturePython)
  n = 0.928318
FEATURE [App::DocumentObjectGroupPython] G4_LEAD_OXIDE  # scripted group (container) (typed FeaturePython)
  Dunit = g/cm3
  Dvalue = 9.53
  Group = -> [O_element053,Pb_element002]
  conduct = 2
  density = 1
  expand = 3
  formula = G4_LEAD_OXIDE
  name = G4_LEAD_OXIDE
  specific = 4
FEATURE [App::DocumentObjectGroupPython] Li_element001  label="Li_element : 1"  # scripted group (container) (typed FeaturePython)
  n = 1
  ref = Li_element
FEATURE [App::DocumentObjectGroupPython] N_element022  label="N_element : 011"  # scripted group (container) (typed FeaturePython)
  n = 1
  ref = N_element
FEATURE [App::DocumentObjectGroupPython] H_element049  label="H_element : 026"  # scripted group (container) (typed FeaturePython)
  n = 2
  ref = H_element
FEATURE [App::DocumentObjectGroupPython] G4_LITHIUM_AMIDE  # scripted group (container) (typed FeaturePython)
  Dunit = g/cm3
  Dvalue = 1.178
  Group = -> [Li_element001,N_element022,H_element049]
  conduct = 2
  density = 1
  expand = 3
  formula = G4_LITHIUM_AMIDE
  name = G4_LITHIUM_AMIDE
  specific = 4
FEATURE [App::DocumentObjectGroupPython] Li_element002  label="Li_element : 2"  # scripted group (container) (typed FeaturePython)
  n = 2
  ref = Li_element
FEATURE [App::DocumentObjectGroupPython] C_element055  label="C_element : 030"  # scripted group (container) (typed FeaturePython)
  n = 1
  ref = C_element
FEATURE [App::DocumentObjectGroupPython] O_element054  label="O_element : 028"  # scripted group (container) (typed FeaturePython)
  n = 3
  ref = O_element
FEATURE [App::DocumentObjectGroupPython] G4_LITHIUM_CARBONATE  # scripted group (container) (typed FeaturePython)
  Dunit = g/cm3
  Dvalue = 2.11
  Group = -> [Li_element002,C_element055,O_element054]
  conduct = 2
  density = 1
  expand = 3
  formula = G4_LITHIUM_CARBONATE
  name = G4_LITHIUM_CARBONATE
  specific = 4
FEATURE [App::DocumentObjectGroupPython] Li_element003  label="Li_element : 003"  # scripted group (container) (typed FeaturePython)
  n = 1
  ref = Li_element
FEATURE [App::DocumentObjectGroupPython] F_element012  label="F_element : 004"  # scripted group (container) (typed FeaturePython)
  n = 1
  ref = F_element
FEATURE [App::DocumentObjectGroupPython] G4_LITHIUM_FLUORIDE  # scripted group (container) (typed FeaturePython)
  Dunit = g/cm3
  Dvalue = 2.635
  Group = -> [Li_element003,F_element012]
  conduct = 2
  density = 1
  expand = 3
  formula = G4_LITHIUM_FLUORIDE
  name = G4_LITHIUM_FLUORIDE
  specific = 4
FEATURE [App::DocumentObjectGroupPython] Li_element004  label="Li_element : 004"  # scripted group (container) (typed FeaturePython)
  n = 1
  ref = Li_element
FEATURE [App::DocumentObjectGroupPython] H_element050  label="H_element : 027"  # scripted group (container) (typed FeaturePython)
  n = 1
  ref = H_element
FEATURE [App::DocumentObjectGroupPython] G4_LITHIUM_HYDRIDE  # scripted group (container) (typed FeaturePython)
  Dunit = g/cm3
  Dvalue = 0.82
  Group = -> [Li_element004,H_element050]
  conduct = 2
  density = 1
  expand = 3
  formula = G4_LITHIUM_HYDRIDE
  name = G4_LITHIUM_HYDRIDE
  specific = 4
FEATURE [App::DocumentObjectGroupPython] Li_element005  label="Li_element : 005"  # scripted group (container) (typed FeaturePython)
  n = 1
  ref = Li_element
FEATURE [App::DocumentObjectGroupPython] I_element003  label="I_element : 002"  # scripted group (container) (typed FeaturePython)
  n = 1
  ref = I_element
FEATURE [App::DocumentObjectGroupPython] G4_LITHIUM_IODIDE  # scripted group (container) (typed FeaturePython)
  Dunit = g/cm3
  Dvalue = 3.494
  Group = -> [Li_element005,I_element003]
  conduct = 2
  density = 1
  expand = 3
  formula = G4_LITHIUM_IODIDE
  name = G4_LITHIUM_IODIDE
  specific = 4
FEATURE [App::DocumentObjectGroupPython] Li_element006  label="Li_element : 006"  # scripted group (container) (typed FeaturePython)
  n = 2
  ref = Li_element
FEATURE [App::DocumentObjectGroupPython] O_element055  label="O_element : 029"  # scripted group (container) (typed FeaturePython)
  n = 1
  ref = O_element
FEATURE [App::DocumentObjectGroupPython] G4_LITHIUM_OXIDE  # scripted group (container) (typed FeaturePython)
  Dunit = g/cm3
  Dvalue = 2.013
  Group = -> [Li_element006,O_element055]
  conduct = 2
  density = 1
  expand = 3
  formula = G4_LITHIUM_OXIDE
  name = G4_LITHIUM_OXIDE
  specific = 4
FEATURE [App::DocumentObjectGroupPython] Li_element007  label="Li_element : 007"  # scripted group (container) (typed FeaturePython)
  n = 2
  ref = Li_element
FEATURE [App::DocumentObjectGroupPython] B_element005  label="B_element : 005"  # scripted group (container) (typed FeaturePython)
  n = 4
  ref = B_element
FEATURE [App::DocumentObjectGroupPython] O_element056  label="O_element : 7"  # scripted group (container) (typed FeaturePython)
  n = 7
  ref = O_element
FEATURE [App::DocumentObjectGroupPython] G4_LITHIUM_TETRABORATE  # scripted group (container) (typed FeaturePython)
  Dunit = g/cm3
  Dvalue = 2.44
  Group = -> [Li_element007,B_element005,O_element056]
  conduct = 2
  density = 1
  expand = 3
  formula = G4_LITHIUM_TETRABORATE
  name = G4_LITHIUM_TETRABORATE
  specific = 4
FEATURE [App::DocumentObjectGroupPython] H_element051  label="H_element : 0.105"  # scripted group (container) (typed FeaturePython)
  n = 0.105
FEATURE [App::DocumentObjectGroupPython] C_element056  label="C_element : 0.083"  # scripted group (container) (typed FeaturePython)
  n = 0.083
FEATURE [App::DocumentObjectGroupPython] N_element023  label="N_element : 0.023"  # scripted group (container) (typed FeaturePython)
  n = 0.023
FEATURE [App::DocumentObjectGroupPython] O_element057  label="O_element : 0.779"  # scripted group (container) (typed FeaturePython)
  n = 0.779
FEATURE [App::DocumentObjectGroupPython] Na_element010  label="Na_element : 0.097"  # scripted group (container) (typed FeaturePython)
  n = 0.002
FEATURE [App::DocumentObjectGroupPython] P_element006  label="P_element : 0.105"  # scripted group (container) (typed FeaturePython)
  n = 0.001
FEATURE [App::DocumentObjectGroupPython] S_element016  label="S_element : 0.017"  # scripted group (container) (typed FeaturePython)
  n = 0.002
FEATURE [App::DocumentObjectGroupPython] Cl_element014  label="Cl_element : 0.587"  # scripted group (container) (typed FeaturePython)
  n = 0.003
FEATURE [App::DocumentObjectGroupPython] K_element005  label="K_element : 0.015"  # scripted group (container) (typed FeaturePython)
  n = 0.002
FEATURE [App::DocumentObjectGroupPython] G4_LUNG_ICRP  # scripted group (container) (typed FeaturePython)
  Dunit = g/cm3
  Dvalue = 1.04
  Group = -> [H_element051,C_element056,N_element023,O_element057,Na_element010,P_element006,S_element016,Cl_element014,K_element005]
  conduct = 2
  density = 1
  expand = 3
  formula = G4_LUNG_ICRP
  name = G4_LUNG_ICRP
  specific = 4
FEATURE [App::DocumentObjectGroupPython] H_element052  label="H_element : 0.116"  # scripted group (container) (typed FeaturePython)
  n = 0.114318
FEATURE [App::DocumentObjectGroupPython] C_element057  label="C_element : 0.656"  # scripted group (container) (typed FeaturePython)
  n = 0.655824
FEATURE [App::DocumentObjectGroupPython] O_element058  label="O_element : 0.092"  # scripted group (container) (typed FeaturePython)
  n = 0.0921831
FEATURE [App::DocumentObjectGroupPython] Mg_element004  label="Mg_element : 0.135"  # scripted group (container) (typed FeaturePython)
  n = 0.134792
FEATURE [App::DocumentObjectGroupPython] Ca_element013  label="Ca_element : 0.003"  # scripted group (container) (typed FeaturePython)
  n = 0.002883
FEATURE [App::DocumentObjectGroupPython] G4_M3_WAX  # scripted group (container) (typed FeaturePython)
  Dunit = g/cm3
  Dvalue = 1.05
  Group = -> [H_element052,C_element057,O_element058,Mg_element004,Ca_element013]
  conduct = 2
  density = 1
  expand = 3
  formula = G4_M3_WAX
  name = G4_M3_WAX
  specific = 4
FEATURE [App::DocumentObjectGroupPython] Mg_element005  label="Mg_element : 1"  # scripted group (container) (typed FeaturePython)
  n = 1
  ref = Mg_element
FEATURE [App::DocumentObjectGroupPython] C_element058  label="C_element : 031"  # scripted group (container) (typed FeaturePython)
  n = 1
  ref = C_element
FEATURE [App::DocumentObjectGroupPython] O_element059  label="O_element : 030"  # scripted group (container) (typed FeaturePython)
  n = 3
  ref = O_element
FEATURE [App::DocumentObjectGroupPython] G4_MAGNESIUM_CARBONATE  # scripted group (container) (typed FeaturePython)
  Dunit = g/cm3
  Dvalue = 2.958
  Group = -> [Mg_element005,C_element058,O_element059]
  conduct = 2
  density = 1
  expand = 3
  formula = G4_MAGNESIUM_CARBONATE
  name = G4_MAGNESIUM_CARBONATE
  specific = 4
FEATURE [App::DocumentObjectGroupPython] Mg_element006  label="Mg_element : 002"  # scripted group (container) (typed FeaturePython)
  n = 1
  ref = Mg_element
FEATURE [App::DocumentObjectGroupPython] F_element013  label="F_element : 005"  # scripted group (container) (typed FeaturePython)
  n = 2
  ref = F_element
FEATURE [App::DocumentObjectGroupPython] G4_MAGNESIUM_FLUORIDE  # scripted group (container) (typed FeaturePython)
  Dunit = g/cm3
  Dvalue = 3
  Group = -> [Mg_element006,F_element013]
  conduct = 2
  density = 1
  expand = 3
  formula = G4_MAGNESIUM_FLUORIDE
  name = G4_MAGNESIUM_FLUORIDE
  specific = 4
FEATURE [App::DocumentObjectGroupPython] Mg_element007  label="Mg_element : 003"  # scripted group (container) (typed FeaturePython)
  n = 1
  ref = Mg_element
FEATURE [App::DocumentObjectGroupPython] O_element060  label="O_element : 031"  # scripted group (container) (typed FeaturePython)
  n = 1
  ref = O_element
FEATURE [App::DocumentObjectGroupPython] G4_MAGNESIUM_OXIDE  # scripted group (container) (typed FeaturePython)
  Dunit = g/cm3
  Dvalue = 3.58
  Group = -> [Mg_element007,O_element060]
  conduct = 2
  density = 1
  expand = 3
  formula = G4_MAGNESIUM_OXIDE
  name = G4_MAGNESIUM_OXIDE
  specific = 4
FEATURE [App::DocumentObjectGroupPython] Mg_element008  label="Mg_element : 004"  # scripted group (container) (typed FeaturePython)
  n = 1
  ref = Mg_element
FEATURE [App::DocumentObjectGroupPython] B_element006  label="B_element : 006"  # scripted group (container) (typed FeaturePython)
  n = 4
  ref = B_element
FEATURE [App::DocumentObjectGroupPython] O_element061  label="O_element : 032"  # scripted group (container) (typed FeaturePython)
  n = 7
  ref = O_element
FEATURE [App::DocumentObjectGroupPython] G4_MAGNESIUM_TETRABORATE  # scripted group (container) (typed FeaturePython)
  Dunit = g/cm3
  Dvalue = 2.53
  Group = -> [Mg_element008,B_element006,O_element061]
  conduct = 2
  density = 1
  expand = 3
  formula = G4_MAGNESIUM_TETRABORATE
  name = G4_MAGNESIUM_TETRABORATE
  specific = 4
FEATURE [App::DocumentObjectGroupPython] Hg_element001  label="Hg_element : 1"  # scripted group (container) (typed FeaturePython)
  n = 1
  ref = Hg_element
FEATURE [App::DocumentObjectGroupPython] I_element004  label="I_element : 2"  # scripted group (container) (typed FeaturePython)
  n = 2
  ref = I_element
FEATURE [App::DocumentObjectGroupPython] G4_MERCURIC_IODIDE  # scripted group (container) (typed FeaturePython)
  Dunit = g/cm3
  Dvalue = 6.36
  Group = -> [Hg_element001,I_element004]
  conduct = 2
  density = 1
  expand = 3
  formula = G4_MERCURIC_IODIDE
  name = G4_MERCURIC_IODIDE
  specific = 4
FEATURE [App::DocumentObjectGroupPython] C_element059  label="C_element : 032"  # scripted group (container) (typed FeaturePython)
  n = 1
  ref = C_element
FEATURE [App::DocumentObjectGroupPython] H_element053  label="H_element : 028"  # scripted group (container) (typed FeaturePython)
  n = 4
  ref = H_element
FEATURE [App::DocumentObjectGroupPython] G4_METHANE  # scripted group (container) (typed FeaturePython)
  Dunit = g/cm3
  Dvalue = 0.000667151
  Group = -> [C_element059,H_element053]
  conduct = 2
  density = 1
  expand = 3
  formula = G4_METHANE
  name = G4_METHANE
  specific = 4
FEATURE [App::DocumentObjectGroupPython] C_element060  label="C_element : 033"  # scripted group (container) (typed FeaturePython)
  n = 1
  ref = C_element
FEATURE [App::DocumentObjectGroupPython] H_element054  label="H_element : 029"  # scripted group (container) (typed FeaturePython)
  n = 4
  ref = H_element
FEATURE [App::DocumentObjectGroupPython] O_element062  label="O_element : 033"  # scripted group (container) (typed FeaturePython)
  n = 1
  ref = O_element
FEATURE [App::DocumentObjectGroupPython] G4_METHANOL  # scripted group (container) (typed FeaturePython)
  Dunit = g/cm3
  Dvalue = 0.7914
  Group = -> [C_element060,H_element054,O_element062]
  conduct = 2
  density = 1
  expand = 3
  formula = G4_METHANOL
  name = G4_METHANOL
  specific = 4
FEATURE [App::DocumentObjectGroupPython] H_element055  label="H_element : 0.134"  # scripted group (container) (typed FeaturePython)
  n = 0.13404
FEATURE [App::DocumentObjectGroupPython] C_element061  label="C_element : 0.778"  # scripted group (container) (typed FeaturePython)
  n = 0.77796
FEATURE [App::DocumentObjectGroupPython] O_element063  label="O_element : 0.035"  # scripted group (container) (typed FeaturePython)
  n = 0.03502
FEATURE [App::DocumentObjectGroupPython] Mg_element009  label="Mg_element : 0.039"  # scripted group (container) (typed FeaturePython)
  n = 0.038594
FEATURE [App::DocumentObjectGroupPython] Ti_element002  label="Ti_element : 0.014"  # scripted group (container) (typed FeaturePython)
  n = 0.014386
FEATURE [App::DocumentObjectGroupPython] G4_MIX_D_WAX  # scripted group (container) (typed FeaturePython)
  Dunit = g/cm3
  Dvalue = 0.99
  Group = -> [H_element055,C_element061,O_element063,Mg_element009,Ti_element002]
  conduct = 2
  density = 1
  expand = 3
  formula = G4_MIX_D_WAX
  name = G4_MIX_D_WAX
  specific = 4
FEATURE [App::DocumentObjectGroupPython] H_element056  label="H_element : 0.135"  # scripted group (container) (typed FeaturePython)
  n = 0.081192
FEATURE [App::DocumentObjectGroupPython] C_element062  label="C_element : 0.583"  # scripted group (container) (typed FeaturePython)
  n = 0.583442
FEATURE [App::DocumentObjectGroupPython] N_element024  label="N_element : 0.018"  # scripted group (container) (typed FeaturePython)
  n = 0.017798
FEATURE [App::DocumentObjectGroupPython] O_element064  label="O_element : 0.186"  # scripted group (container) (typed FeaturePython)
  n = 0.186381
FEATURE [App::DocumentObjectGroupPython] Mg_element010  label="Mg_element : 0.130"  # scripted group (container) (typed FeaturePython)
  n = 0.130287
FEATURE [App::DocumentObjectGroupPython] Cl_element015  label="Cl_element : 0.588"  # scripted group (container) (typed FeaturePython)
  n = 0.0009
FEATURE [App::DocumentObjectGroupPython] G4_MS20_TISSUE  # scripted group (container) (typed FeaturePython)
  Dunit = g/cm3
  Dvalue = 1
  Group = -> [H_element056,C_element062,N_element024,O_element064,Mg_element010,Cl_element015]
  conduct = 2
  density = 1
  expand = 3
  formula = G4_MS20_TISSUE
  name = G4_MS20_TISSUE
  specific = 4
FEATURE [App::DocumentObjectGroupPython] H_element057  label="H_element : 0.136"  # scripted group (container) (typed FeaturePython)
  n = 0.102
FEATURE [App::DocumentObjectGroupPython] C_element063  label="C_element : 0.143"  # scripted group (container) (typed FeaturePython)
  n = 0.143
FEATURE [App::DocumentObjectGroupPython] N_element025  label="N_element : 0.034"  # scripted group (container) (typed FeaturePython)
  n = 0.034
FEATURE [App::DocumentObjectGroupPython] O_element065  label="O_element : 0.710"  # scripted group (container) (typed FeaturePython)
  n = 0.71
FEATURE [App::DocumentObjectGroupPython] Na_element011  label="Na_element : 0.098"  # scripted group (container) (typed FeaturePython)
  n = 0.001
FEATURE [App::DocumentObjectGroupPython] P_element007  label="P_element : 0.002"  # scripted group (container) (typed FeaturePython)
  n = 0.002
FEATURE [App::DocumentObjectGroupPython] S_element017  label="S_element : 0.018"  # scripted group (container) (typed FeaturePython)
  n = 0.003
FEATURE [App::DocumentObjectGroupPython] Cl_element016  label="Cl_element : 0.589"  # scripted group (container) (typed FeaturePython)
  n = 0.001
FEATURE [App::DocumentObjectGroupPython] K_element006  label="K_element : 0.004"  # scripted group (container) (typed FeaturePython)
  n = 0.004
FEATURE [App::DocumentObjectGroupPython] G4_MUSCLE_SKELETAL_ICRP  # scripted group (container) (typed FeaturePython)
  Dunit = g/cm3
  Dvalue = 1.05
  Group = -> [H_element057,C_element063,N_element025,O_element065,Na_element011,P_element007,S_element017,Cl_element016,K_element006]
  conduct = 2
  density = 1
  expand = 3
  formula = G4_MUSCLE_SKELETAL_ICRP
  name = G4_MUSCLE_SKELETAL_ICRP
  specific = 4
FEATURE [App::DocumentObjectGroupPython] H_element058  label="H_element : 0.137"  # scripted group (container) (typed FeaturePython)
  n = 0.102102
FEATURE [App::DocumentObjectGroupPython] C_element064  label="C_element : 0.123"  # scripted group (container) (typed FeaturePython)
  n = 0.123123
FEATURE [App::DocumentObjectGroupPython] N_element026  label="N_element : 0.756"  # scripted group (container) (typed FeaturePython)
  n = 0.035035
FEATURE [App::DocumentObjectGroupPython] O_element066  label="O_element : 0.730"  # scripted group (container) (typed FeaturePython)
  n = 0.72973
FEATURE [App::DocumentObjectGroupPython] Na_element012  label="Na_element : 0.099"  # scripted group (container) (typed FeaturePython)
  n = 0.001001
FEATURE [App::DocumentObjectGroupPython] P_element008  label="P_element : 0.106"  # scripted group (container) (typed FeaturePython)
  n = 0.002002
FEATURE [App::DocumentObjectGroupPython] S_element018  label="S_element : 0.019"  # scripted group (container) (typed FeaturePython)
  n = 0.004004
FEATURE [App::DocumentObjectGroupPython] K_element007  label="K_element : 0.016"  # scripted group (container) (typed FeaturePython)
  n = 0.003003
FEATURE [App::DocumentObjectGroupPython] G4_MUSCLE_STRIATED_ICRU  # scripted group (container) (typed FeaturePython)
  Dunit = g/cm3
  Dvalue = 1.04
  Group = -> [H_element058,C_element064,N_element026,O_element066,Na_element012,P_element008,S_element018,K_element007]
  conduct = 2
  density = 1
  expand = 3
  formula = G4_MUSCLE_STRIATED_ICRU
  name = G4_MUSCLE_STRIATED_ICRU
  specific = 4
FEATURE [App::DocumentObjectGroupPython] H_element059  label="H_element : 0.098"  # scripted group (container) (typed FeaturePython)
  n = 0.0982341
FEATURE [App::DocumentObjectGroupPython] C_element065  label="C_element : 0.156"  # scripted group (container) (typed FeaturePython)
  n = 0.156214
FEATURE [App::DocumentObjectGroupPython] N_element027  label="N_element : 0.757"  # scripted group (container) (typed FeaturePython)
  n = 0.035451
FEATURE [App::DocumentObjectGroupPython] O_element067  label="O_element : 0.880"  # scripted group (container) (typed FeaturePython)
  n = 0.710101
FEATURE [App::DocumentObjectGroupPython] G4_MUSCLE_WITH_SUCROSE  # scripted group (container) (typed FeaturePython)
  Dunit = g/cm3
  Dvalue = 1.11
  Group = -> [H_element059,C_element065,N_element027,O_element067]
  conduct = 2
  density = 1
  expand = 3
  formula = G4_MUSCLE_WITH_SUCROSE
  name = G4_MUSCLE_WITH_SUCROSE
  specific = 4
FEATURE [App::DocumentObjectGroupPython] H_element060  label="H_element : 0.138"  # scripted group (container) (typed FeaturePython)
  n = 0.101969
FEATURE [App::DocumentObjectGroupPython] C_element066  label="C_element : 0.120"  # scripted group (container) (typed FeaturePython)
  n = 0.120058
FEATURE [App::DocumentObjectGroupPython] N_element028  label="N_element : 0.758"  # scripted group (container) (typed FeaturePython)
  n = 0.035451
FEATURE [App::DocumentObjectGroupPython] O_element068  label="O_element : 0.743"  # scripted group (container) (typed FeaturePython)
  n = 0.742522
FEATURE [App::DocumentObjectGroupPython] G4_MUSCLE_WITHOUT_SUCROSE  # scripted group (container) (typed FeaturePython)
  Dunit = g/cm3
  Dvalue = 1.07
  Group = -> [H_element060,C_element066,N_element028,O_element068]
  conduct = 2
  density = 1
  expand = 3
  formula = G4_MUSCLE_WITHOUT_SUCROSE
  name = G4_MUSCLE_WITHOUT_SUCROSE
  specific = 4
FEATURE [App::DocumentObjectGroupPython] C_element067  label="C_element : 10"  # scripted group (container) (typed FeaturePython)
  n = 10
  ref = C_element
FEATURE [App::DocumentObjectGroupPython] H_element061  label="H_element : 030"  # scripted group (container) (typed FeaturePython)
  n = 8
  ref = H_element
FEATURE [App::DocumentObjectGroupPython] G4_NAPHTHALENE  # scripted group (container) (typed FeaturePython)
  Dunit = g/cm3
  Dvalue = 1.145
  Group = -> [C_element067,H_element061]
  conduct = 2
  density = 1
  expand = 3
  formula = G4_NAPHTHALENE
  name = G4_NAPHTHALENE
  specific = 4
FEATURE [App::DocumentObjectGroupPython] C_element068  label="C_element : 034"  # scripted group (container) (typed FeaturePython)
  n = 6
  ref = C_element
FEATURE [App::DocumentObjectGroupPython] H_element062  label="H_element : 031"  # scripted group (container) (typed FeaturePython)
  n = 5
  ref = H_element
FEATURE [App::DocumentObjectGroupPython] N_element029  label="N_element : 012"  # scripted group (container) (typed FeaturePython)
  n = 1
  ref = N_element
FEATURE [App::DocumentObjectGroupPython] O_element069  label="O_element : 034"  # scripted group (container) (typed FeaturePython)
  n = 2
  ref = O_element
FEATURE [App::DocumentObjectGroupPython] G4_NITROBENZENE  # scripted group (container) (typed FeaturePython)
  Dunit = g/cm3
  Dvalue = 1.19867
  Group = -> [C_element068,H_element062,N_element029,O_element069]
  conduct = 2
  density = 1
  expand = 3
  formula = G4_NITROBENZENE
  name = G4_NITROBENZENE
  specific = 4
FEATURE [App::DocumentObjectGroupPython] N_element030  label="N_element : 013"  # scripted group (container) (typed FeaturePython)
  n = 2
  ref = N_element
FEATURE [App::DocumentObjectGroupPython] O_element070  label="O_element : 035"  # scripted group (container) (typed FeaturePython)
  n = 1
  ref = O_element
FEATURE [App::DocumentObjectGroupPython] G4_NITROUS_OXIDE  # scripted group (container) (typed FeaturePython)
  Dunit = g/cm3
  Dvalue = 0.00183094
  Group = -> [N_element030,O_element070]
  conduct = 2
  density = 1
  expand = 3
  formula = G4_NITROUS_OXIDE
  name = G4_NITROUS_OXIDE
  specific = 4
FEATURE [App::DocumentObjectGroupPython] H_element063  label="H_element : 0.104"  # scripted group (container) (typed FeaturePython)
  n = 0.103509
FEATURE [App::DocumentObjectGroupPython] C_element069  label="C_element : 0.648"  # scripted group (container) (typed FeaturePython)
  n = 0.648416
FEATURE [App::DocumentObjectGroupPython] N_element031  label="N_element : 0.100"  # scripted group (container) (typed FeaturePython)
  n = 0.0995361
FEATURE [App::DocumentObjectGroupPython] O_element071  label="O_element : 0.149"  # scripted group (container) (typed FeaturePython)
  n = 0.148539
FEATURE [App::DocumentObjectGroupPython] G4_NYLON_8062  label="G4_NYLON-8062"  # scripted group (container) (typed FeaturePython)
  Dunit = g/cm3
  Dvalue = 1.08
  Group = -> [H_element063,C_element069,N_element031,O_element071]
  conduct = 2
  density = 1
  expand = 3
  formula = G4_NYLON-8062
  name = G4_NYLON-8062
  specific = 4
FEATURE [App::DocumentObjectGroupPython] C_element070  label="C_element : 035"  # scripted group (container) (typed FeaturePython)
  n = 6
  ref = C_element
FEATURE [App::DocumentObjectGroupPython] H_element064  label="H_element : 11"  # scripted group (container) (typed FeaturePython)
  n = 11
  ref = H_element
FEATURE [App::DocumentObjectGroupPython] N_element032  label="N_element : 014"  # scripted group (container) (typed FeaturePython)
  n = 1
  ref = N_element
FEATURE [App::DocumentObjectGroupPython] O_element072  label="O_element : 036"  # scripted group (container) (typed FeaturePython)
  n = 1
  ref = O_element
FEATURE [App::DocumentObjectGroupPython] G4_NYLON_6_6  label="G4_NYLON-6-6"  # scripted group (container) (typed FeaturePython)
  Dunit = g/cm3
  Dvalue = 1.14
  Group = -> [C_element070,H_element064,N_element032,O_element072]
  conduct = 2
  density = 1
  expand = 3
  formula = G4_NYLON-6-6
  name = G4_NYLON-6-6
  specific = 4
FEATURE [App::DocumentObjectGroupPython] H_element065  label="H_element : 0.139"  # scripted group (container) (typed FeaturePython)
  n = 0.107062
FEATURE [App::DocumentObjectGroupPython] C_element071  label="C_element : 0.680"  # scripted group (container) (typed FeaturePython)
  n = 0.680449
FEATURE [App::DocumentObjectGroupPython] N_element033  label="N_element : 0.099"  # scripted group (container) (typed FeaturePython)
  n = 0.099189
FEATURE [App::DocumentObjectGroupPython] O_element073  label="O_element : 0.113"  # scripted group (container) (typed FeaturePython)
  n = 0.1133
FEATURE [App::DocumentObjectGroupPython] G4_NYLON_6_10  label="G4_NYLON-6-10"  # scripted group (container) (typed FeaturePython)
  Dunit = g/cm3
  Dvalue = 1.14
  Group = -> [H_element065,C_element071,N_element033,O_element073]
  conduct = 2
  density = 1
  expand = 3
  formula = G4_NYLON-6-10
  name = G4_NYLON-6-10
  specific = 4
FEATURE [App::DocumentObjectGroupPython] H_element066  label="H_element : 0.140"  # scripted group (container) (typed FeaturePython)
  n = 0.115476
FEATURE [App::DocumentObjectGroupPython] C_element072  label="C_element : 0.721"  # scripted group (container) (typed FeaturePython)
  n = 0.720818
FEATURE [App::DocumentObjectGroupPython] N_element034  label="N_element : 0.076"  # scripted group (container) (typed FeaturePython)
  n = 0.0764169
FEATURE [App::DocumentObjectGroupPython] O_element074  label="O_element : 0.087"  # scripted group (container) (typed FeaturePython)
  n = 0.0872889
FEATURE [App::DocumentObjectGroupPython] G4_NYLON_11_RILSAN  label="G4_NYLON-11_RILSAN"  # scripted group (container) (typed FeaturePython)
  Dunit = g/cm3
  Dvalue = 1.425
  Group = -> [H_element066,C_element072,N_element034,O_element074]
  conduct = 2
  density = 1
  expand = 3
  formula = G4_NYLON-11_RILSAN
  name = G4_NYLON-11_RILSAN
  specific = 4
FEATURE [App::DocumentObjectGroupPython] C_element073  label="C_element : 8"  # scripted group (container) (typed FeaturePython)
  n = 8
  ref = C_element
FEATURE [App::DocumentObjectGroupPython] H_element067  label="H_element : 18"  # scripted group (container) (typed FeaturePython)
  n = 18
  ref = H_element
FEATURE [App::DocumentObjectGroupPython] G4_OCTANE  # scripted group (container) (typed FeaturePython)
  Dunit = g/cm3
  Dvalue = 0.7026
  Group = -> [C_element073,H_element067]
  conduct = 2
  density = 1
  expand = 3
  formula = G4_OCTANE
  name = G4_OCTANE
  specific = 4
FEATURE [App::DocumentObjectGroupPython] C_element074  label="C_element : 25"  # scripted group (container) (typed FeaturePython)
  n = 25
  ref = C_element
FEATURE [App::DocumentObjectGroupPython] H_element068  label="H_element : 52"  # scripted group (container) (typed FeaturePython)
  n = 52
  ref = H_element
FEATURE [App::DocumentObjectGroupPython] G4_PARAFFIN  # scripted group (container) (typed FeaturePython)
  Dunit = g/cm3
  Dvalue = 0.93
  Group = -> [C_element074,H_element068]
  conduct = 2
  density = 1
  expand = 3
  formula = G4_PARAFFIN
  name = G4_PARAFFIN
  specific = 4
FEATURE [App::DocumentObjectGroupPython] C_element075  label="C_element : 036"  # scripted group (container) (typed FeaturePython)
  n = 5
  ref = C_element
FEATURE [App::DocumentObjectGroupPython] H_element069  label="H_element : 032"  # scripted group (container) (typed FeaturePython)
  n = 12
  ref = H_element
FEATURE [App::DocumentObjectGroupPython] G4_N_PENTANE  label="G4_N-PENTANE"  # scripted group (container) (typed FeaturePython)
  Dunit = g/cm3
  Dvalue = 0.6262
  Group = -> [C_element075,H_element069]
  conduct = 2
  density = 1
  expand = 3
  formula = G4_N-PENTANE
  name = G4_N-PENTANE
  specific = 4
FEATURE [App::DocumentObjectGroupPython] H_element070  label="H_element : 0.014"  # scripted group (container) (typed FeaturePython)
  n = 0.0141
FEATURE [App::DocumentObjectGroupPython] C_element076  label="C_element : 0.072"  # scripted group (container) (typed FeaturePython)
  n = 0.072261
FEATURE [App::DocumentObjectGroupPython] N_element035  label="N_element : 0.019"  # scripted group (container) (typed FeaturePython)
  n = 0.01932
FEATURE [App::DocumentObjectGroupPython] O_element075  label="O_element : 0.066"  # scripted group (container) (typed FeaturePython)
  n = 0.066101
FEATURE [App::DocumentObjectGroupPython] S_element019  label="S_element : 0.020"  # scripted group (container) (typed FeaturePython)
  n = 0.00189
FEATURE [App::DocumentObjectGroupPython] Br_element004  label="Br_element : 0.349"  # scripted group (container) (typed FeaturePython)
  n = 0.349103
FEATURE [App::DocumentObjectGroupPython] Ag_element001  label="Ag_element : 0.474"  # scripted group (container) (typed FeaturePython)
  n = 0.474105
FEATURE [App::DocumentObjectGroupPython] I_element005  label="I_element : 0.003"  # scripted group (container) (typed FeaturePython)
  n = 0.00312
FEATURE [App::DocumentObjectGroupPython] G4_PHOTO_EMULSION  # scripted group (container) (typed FeaturePython)
  Dunit = g/cm3
  Dvalue = 3.815
  Group = -> [H_element070,C_element076,N_element035,O_element075,S_element019,Br_element004,Ag_element001,I_element005]
  conduct = 2
  density = 1
  expand = 3
  formula = G4_PHOTO_EMULSION
  name = G4_PHOTO_EMULSION
  specific = 4
FEATURE [App::DocumentObjectGroupPython] C_element077  label="C_element : 9"  # scripted group (container) (typed FeaturePython)
  n = 9
  ref = C_element
FEATURE [App::DocumentObjectGroupPython] H_element071  label="H_element : 033"  # scripted group (container) (typed FeaturePython)
  n = 10
  ref = H_element
FEATURE [App::DocumentObjectGroupPython] G4_PLASTIC_SC_VINYLTOLUENE  # scripted group (container) (typed FeaturePython)
  Dunit = g/cm3
  Dvalue = 1.032
  Group = -> [C_element077,H_element071]
  conduct = 2
  density = 1
  expand = 3
  formula = G4_PLASTIC_SC_VINYLTOLUENE
  name = G4_PLASTIC_SC_VINYLTOLUENE
  specific = 4
FEATURE [App::DocumentObjectGroupPython] Pu_element001  label="Pu_element : 1"  # scripted group (container) (typed FeaturePython)
  n = 1
  ref = Pu_element
FEATURE [App::DocumentObjectGroupPython] O_element076  label="O_element : 037"  # scripted group (container) (typed FeaturePython)
  n = 2
  ref = O_element
FEATURE [App::DocumentObjectGroupPython] G4_PLUTONIUM_DIOXIDE  # scripted group (container) (typed FeaturePython)
  Dunit = g/cm3
  Dvalue = 11.46
  Group = -> [Pu_element001,O_element076]
  conduct = 2
  density = 1
  expand = 3
  formula = G4_PLUTONIUM_DIOXIDE
  name = G4_PLUTONIUM_DIOXIDE
  specific = 4
FEATURE [App::DocumentObjectGroupPython] C_element078  label="C_element : 037"  # scripted group (container) (typed FeaturePython)
  n = 3
  ref = C_element
FEATURE [App::DocumentObjectGroupPython] H_element072  label="H_element : 034"  # scripted group (container) (typed FeaturePython)
  n = 3
  ref = H_element
FEATURE [App::DocumentObjectGroupPython] N_element036  label="N_element : 015"  # scripted group (container) (typed FeaturePython)
  n = 1
  ref = N_element
FEATURE [App::DocumentObjectGroupPython] G4_POLYACRYLONITRILE  # scripted group (container) (typed FeaturePython)
  Dunit = g/cm3
  Dvalue = 1.17
  Group = -> [C_element078,H_element072,N_element036]
  conduct = 2
  density = 1
  expand = 3
  formula = G4_POLYACRYLONITRILE
  name = G4_POLYACRYLONITRILE
  specific = 4
FEATURE [App::DocumentObjectGroupPython] C_element079  label="C_element : 16"  # scripted group (container) (typed FeaturePython)
  n = 16
  ref = C_element
FEATURE [App::DocumentObjectGroupPython] H_element073  label="H_element : 035"  # scripted group (container) (typed FeaturePython)
  n = 14
  ref = H_element
FEATURE [App::DocumentObjectGroupPython] O_element077  label="O_element : 038"  # scripted group (container) (typed FeaturePython)
  n = 3
  ref = O_element
FEATURE [App::DocumentObjectGroupPython] G4_POLYCARBONATE  # scripted group (container) (typed FeaturePython)
  Dunit = g/cm3
  Dvalue = 1.2
  Group = -> [C_element079,H_element073,O_element077]
  conduct = 2
  density = 1
  expand = 3
  formula = G4_POLYCARBONATE
  name = G4_POLYCARBONATE
  specific = 4
FEATURE [App::DocumentObjectGroupPython] C_element080  label="C_element : 038"  # scripted group (container) (typed FeaturePython)
  n = 8
  ref = C_element
FEATURE [App::DocumentObjectGroupPython] H_element074  label="H_element : 036"  # scripted group (container) (typed FeaturePython)
  n = 7
  ref = H_element
FEATURE [App::DocumentObjectGroupPython] Cl_element017  label="Cl_element : 007"  # scripted group (container) (typed FeaturePython)
  n = 1
  ref = Cl_element
FEATURE [App::DocumentObjectGroupPython] G4_POLYCHLOROSTYRENE  # scripted group (container) (typed FeaturePython)
  Dunit = g/cm3
  Dvalue = 1.3
  Group = -> [C_element080,H_element074,Cl_element017]
  conduct = 2
  density = 1
  expand = 3
  formula = G4_POLYCHLOROSTYRENE
  name = G4_POLYCHLOROSTYRENE
  specific = 4
FEATURE [App::DocumentObjectGroupPython] C_element081  label="C_element : 039"  # scripted group (container) (typed FeaturePython)
  n = 1
  ref = C_element
FEATURE [App::DocumentObjectGroupPython] H_element075  label="H_element : 037"  # scripted group (container) (typed FeaturePython)
  n = 2
  ref = H_element
FEATURE [App::DocumentObjectGroupPython] G4_POLYETHYLENE  # scripted group (container) (typed FeaturePython)
  Dunit = g/cm3
  Dvalue = 0.94
  Group = -> [C_element081,H_element075]
  conduct = 2
  density = 1
  expand = 3
  formula = G4_POLYETHYLENE
  name = G4_POLYETHYLENE
  specific = 4
FEATURE [App::DocumentObjectGroupPython] C_element082  label="C_element : 040"  # scripted group (container) (typed FeaturePython)
  n = 10
  ref = C_element
FEATURE [App::DocumentObjectGroupPython] H_element076  label="H_element : 038"  # scripted group (container) (typed FeaturePython)
  n = 8
  ref = H_element
FEATURE [App::DocumentObjectGroupPython] O_element078  label="O_element : 039"  # scripted group (container) (typed FeaturePython)
  n = 4
  ref = O_element
FEATURE [App::DocumentObjectGroupPython] G4_MYLAR  # scripted group (container) (typed FeaturePython)
  Dunit = g/cm3
  Dvalue = 1.4
  Group = -> [C_element082,H_element076,O_element078]
  conduct = 2
  density = 1
  expand = 3
  formula = G4_MYLAR
  name = G4_MYLAR
  specific = 4
FEATURE [App::DocumentObjectGroupPython] C_element083  label="C_element : 041"  # scripted group (container) (typed FeaturePython)
  n = 5
  ref = C_element
FEATURE [App::DocumentObjectGroupPython] H_element077  label="H_element : 039"  # scripted group (container) (typed FeaturePython)
  n = 8
  ref = H_element
FEATURE [App::DocumentObjectGroupPython] O_element079  label="O_element : 040"  # scripted group (container) (typed FeaturePython)
  n = 2
  ref = O_element
FEATURE [App::DocumentObjectGroupPython] G4_PLEXIGLASS  # scripted group (container) (typed FeaturePython)
  Dunit = g/cm3
  Dvalue = 1.19
  Group = -> [C_element083,H_element077,O_element079]
  conduct = 2
  density = 1
  expand = 3
  formula = G4_PLEXIGLASS
  name = G4_PLEXIGLASS
  specific = 4
FEATURE [App::DocumentObjectGroupPython] C_element084  label="C_element : 042"  # scripted group (container) (typed FeaturePython)
  n = 1
  ref = C_element
FEATURE [App::DocumentObjectGroupPython] H_element078  label="H_element : 040"  # scripted group (container) (typed FeaturePython)
  n = 2
  ref = H_element
FEATURE [App::DocumentObjectGroupPython] O_element080  label="O_element : 041"  # scripted group (container) (typed FeaturePython)
  n = 1
  ref = O_element
FEATURE [App::DocumentObjectGroupPython] G4_POLYOXYMETHYLENE  # scripted group (container) (typed FeaturePython)
  Dunit = g/cm3
  Dvalue = 1.425
  Group = -> [C_element084,H_element078,O_element080]
  conduct = 2
  density = 1
  expand = 3
  formula = G4_POLYOXYMETHYLENE
  name = G4_POLYOXYMETHYLENE
  specific = 4
FEATURE [App::DocumentObjectGroupPython] C_element085  label="C_element : 043"  # scripted group (container) (typed FeaturePython)
  n = 2
  ref = C_element
FEATURE [App::DocumentObjectGroupPython] H_element079  label="H_element : 041"  # scripted group (container) (typed FeaturePython)
  n = 4
  ref = H_element
FEATURE [App::DocumentObjectGroupPython] G4_POLYPROPYLENE  # scripted group (container) (typed FeaturePython)
  Dunit = g/cm3
  Dvalue = 0.9
  Group = -> [C_element085,H_element079]
  conduct = 2
  density = 1
  expand = 3
  formula = G4_POLYPROPYLENE
  name = G4_POLYPROPYLENE
  specific = 4
FEATURE [App::DocumentObjectGroupPython] C_element086  label="C_element : 044"  # scripted group (container) (typed FeaturePython)
  n = 8
  ref = C_element
FEATURE [App::DocumentObjectGroupPython] H_element080  label="H_element : 042"  # scripted group (container) (typed FeaturePython)
  n = 8
  ref = H_element
FEATURE [App::DocumentObjectGroupPython] G4_POLYSTYRENE  # scripted group (container) (typed FeaturePython)
  Dunit = g/cm3
  Dvalue = 1.06
  Group = -> [C_element086,H_element080]
  conduct = 2
  density = 1
  expand = 3
  formula = G4_POLYSTYRENE
  name = G4_POLYSTYRENE
  specific = 4
FEATURE [App::DocumentObjectGroupPython] C_element087  label="C_element : 045"  # scripted group (container) (typed FeaturePython)
  n = 2
  ref = C_element
FEATURE [App::DocumentObjectGroupPython] F_element014  label="F_element : 4"  # scripted group (container) (typed FeaturePython)
  n = 4
  ref = F_element
FEATURE [App::DocumentObjectGroupPython] G4_TEFLON  # scripted group (container) (typed FeaturePython)
  Dunit = g/cm3
  Dvalue = 2.2
  Group = -> [C_element087,F_element014]
  conduct = 2
  density = 1
  expand = 3
  formula = G4_TEFLON
  name = G4_TEFLON
  specific = 4
FEATURE [App::DocumentObjectGroupPython] C_element088  label="C_element : 046"  # scripted group (container) (typed FeaturePython)
  n = 2
  ref = C_element
FEATURE [App::DocumentObjectGroupPython] F_element015  label="F_element : 006"  # scripted group (container) (typed FeaturePython)
  n = 3
  ref = F_element
FEATURE [App::DocumentObjectGroupPython] Cl_element018  label="Cl_element : 008"  # scripted group (container) (typed FeaturePython)
  n = 1
  ref = Cl_element
FEATURE [App::DocumentObjectGroupPython] G4_POLYTRIFLUOROCHLOROETHYLENE  # scripted group (container) (typed FeaturePython)
  Dunit = g/cm3
  Dvalue = 2.1
  Group = -> [C_element088,F_element015,Cl_element018]
  conduct = 2
  density = 1
  expand = 3
  formula = G4_POLYTRIFLUOROCHLOROETHYLENE
  name = G4_POLYTRIFLUOROCHLOROETHYLENE
  specific = 4
FEATURE [App::DocumentObjectGroupPython] C_element089  label="C_element : 047"  # scripted group (container) (typed FeaturePython)
  n = 4
  ref = C_element
FEATURE [App::DocumentObjectGroupPython] H_element081  label="H_element : 043"  # scripted group (container) (typed FeaturePython)
  n = 6
  ref = H_element
FEATURE [App::DocumentObjectGroupPython] O_element081  label="O_element : 042"  # scripted group (container) (typed FeaturePython)
  n = 2
  ref = O_element
FEATURE [App::DocumentObjectGroupPython] G4_POLYVINYL_ACETATE  # scripted group (container) (typed FeaturePython)
  Dunit = g/cm3
  Dvalue = 1.19
  Group = -> [C_element089,H_element081,O_element081]
  conduct = 2
  density = 1
  expand = 3
  formula = G4_POLYVINYL_ACETATE
  name = G4_POLYVINYL_ACETATE
  specific = 4
FEATURE [App::DocumentObjectGroupPython] C_element090  label="C_element : 048"  # scripted group (container) (typed FeaturePython)
  n = 2
  ref = C_element
FEATURE [App::DocumentObjectGroupPython] H_element082  label="H_element : 044"  # scripted group (container) (typed FeaturePython)
  n = 4
  ref = H_element
FEATURE [App::DocumentObjectGroupPython] O_element082  label="O_element : 043"  # scripted group (container) (typed FeaturePython)
  n = 1
  ref = O_element
FEATURE [App::DocumentObjectGroupPython] G4_POLYVINYL_ALCOHOL  # scripted group (container) (typed FeaturePython)
  Dunit = g/cm3
  Dvalue = 1.3
  Group = -> [C_element090,H_element082,O_element082]
  conduct = 2
  density = 1
  expand = 3
  formula = G4_POLYVINYL_ALCOHOL
  name = G4_POLYVINYL_ALCOHOL
  specific = 4
FEATURE [App::DocumentObjectGroupPython] C_element091  label="C_element : 049"  # scripted group (container) (typed FeaturePython)
  n = 8
  ref = C_element
FEATURE [App::DocumentObjectGroupPython] H_element083  label="H_element : 045"  # scripted group (container) (typed FeaturePython)
  n = 14
  ref = H_element
FEATURE [App::DocumentObjectGroupPython] O_element083  label="O_element : 044"  # scripted group (container) (typed FeaturePython)
  n = 2
  ref = O_element
FEATURE [App::DocumentObjectGroupPython] G4_POLYVINYL_BUTYRAL  # scripted group (container) (typed FeaturePython)
  Dunit = g/cm3
  Dvalue = 1.12
  Group = -> [C_element091,H_element083,O_element083]
  conduct = 2
  density = 1
  expand = 3
  formula = G4_POLYVINYL_BUTYRAL
  name = G4_POLYVINYL_BUTYRAL
  specific = 4
FEATURE [App::DocumentObjectGroupPython] C_element092  label="C_element : 050"  # scripted group (container) (typed FeaturePython)
  n = 2
  ref = C_element
FEATURE [App::DocumentObjectGroupPython] H_element084  label="H_element : 046"  # scripted group (container) (typed FeaturePython)
  n = 3
  ref = H_element
FEATURE [App::DocumentObjectGroupPython] Cl_element019  label="Cl_element : 009"  # scripted group (container) (typed FeaturePython)
  n = 1
  ref = Cl_element
FEATURE [App::DocumentObjectGroupPython] G4_POLYVINYL_CHLORIDE  # scripted group (container) (typed FeaturePython)
  Dunit = g/cm3
  Dvalue = 1.3
  Group = -> [C_element092,H_element084,Cl_element019]
  conduct = 2
  density = 1
  expand = 3
  formula = G4_POLYVINYL_CHLORIDE
  name = G4_POLYVINYL_CHLORIDE
  specific = 4
FEATURE [App::DocumentObjectGroupPython] C_element093  label="C_element : 051"  # scripted group (container) (typed FeaturePython)
  n = 2
  ref = C_element
FEATURE [App::DocumentObjectGroupPython] H_element085  label="H_element : 047"  # scripted group (container) (typed FeaturePython)
  n = 2
  ref = H_element
FEATURE [App::DocumentObjectGroupPython] Cl_element020  label="Cl_element : 010"  # scripted group (container) (typed FeaturePython)
  n = 2
  ref = Cl_element
FEATURE [App::DocumentObjectGroupPython] G4_POLYVINYLIDENE_CHLORIDE  # scripted group (container) (typed FeaturePython)
  Dunit = g/cm3
  Dvalue = 1.7
  Group = -> [C_element093,H_element085,Cl_element020]
  conduct = 2
  density = 1
  expand = 3
  formula = G4_POLYVINYLIDENE_CHLORIDE
  name = G4_POLYVINYLIDENE_CHLORIDE
  specific = 4
FEATURE [App::DocumentObjectGroupPython] C_element094  label="C_element : 052"  # scripted group (container) (typed FeaturePython)
  n = 2
  ref = C_element
FEATURE [App::DocumentObjectGroupPython] H_element086  label="H_element : 048"  # scripted group (container) (typed FeaturePython)
  n = 2
  ref = H_element
FEATURE [App::DocumentObjectGroupPython] F_element016  label="F_element : 007"  # scripted group (container) (typed FeaturePython)
  n = 2
  ref = F_element
FEATURE [App::DocumentObjectGroupPython] G4_POLYVINYLIDENE_FLUORIDE  # scripted group (container) (typed FeaturePython)
  Dunit = g/cm3
  Dvalue = 1.76
  Group = -> [C_element094,H_element086,F_element016]
  conduct = 2
  density = 1
  expand = 3
  formula = G4_POLYVINYLIDENE_FLUORIDE
  name = G4_POLYVINYLIDENE_FLUORIDE
  specific = 4
FEATURE [App::DocumentObjectGroupPython] C_element095  label="C_element : 053"  # scripted group (container) (typed FeaturePython)
  n = 6
  ref = C_element
FEATURE [App::DocumentObjectGroupPython] H_element087  label="H_element : 9"  # scripted group (container) (typed FeaturePython)
  n = 9
  ref = H_element
FEATURE [App::DocumentObjectGroupPython] N_element037  label="N_element : 016"  # scripted group (container) (typed FeaturePython)
  n = 1
  ref = N_element
FEATURE [App::DocumentObjectGroupPython] O_element084  label="O_element : 045"  # scripted group (container) (typed FeaturePython)
  n = 1
  ref = O_element
FEATURE [App::DocumentObjectGroupPython] G4_POLYVINYL_PYRROLIDONE  # scripted group (container) (typed FeaturePython)
  Dunit = g/cm3
  Dvalue = 1.25
  Group = -> [C_element095,H_element087,N_element037,O_element084]
  conduct = 2
  density = 1
  expand = 3
  formula = G4_POLYVINYL_PYRROLIDONE
  name = G4_POLYVINYL_PYRROLIDONE
  specific = 4
FEATURE [App::DocumentObjectGroupPython] K_element008  label="K_element : 1"  # scripted group (container) (typed FeaturePython)
  n = 1
  ref = K_element
FEATURE [App::DocumentObjectGroupPython] I_element006  label="I_element : 003"  # scripted group (container) (typed FeaturePython)
  n = 1
  ref = I_element
FEATURE [App::DocumentObjectGroupPython] G4_POTASSIUM_IODIDE  # scripted group (container) (typed FeaturePython)
  Dunit = g/cm3
  Dvalue = 3.13
  Group = -> [K_element008,I_element006]
  conduct = 2
  density = 1
  expand = 3
  formula = G4_POTASSIUM_IODIDE
  name = G4_POTASSIUM_IODIDE
  specific = 4
FEATURE [App::DocumentObjectGroupPython] K_element009  label="K_element : 2"  # scripted group (container) (typed FeaturePython)
  n = 2
  ref = K_element
FEATURE [App::DocumentObjectGroupPython] O_element085  label="O_element : 046"  # scripted group (container) (typed FeaturePython)
  n = 1
  ref = O_element
FEATURE [App::DocumentObjectGroupPython] G4_POTASSIUM_OXIDE  # scripted group (container) (typed FeaturePython)
  Dunit = g/cm3
  Dvalue = 2.32
  Group = -> [K_element009,O_element085]
  conduct = 2
  density = 1
  expand = 3
  formula = G4_POTASSIUM_OXIDE
  name = G4_POTASSIUM_OXIDE
  specific = 4
FEATURE [App::DocumentObjectGroupPython] C_element096  label="C_element : 054"  # scripted group (container) (typed FeaturePython)
  n = 3
  ref = C_element
FEATURE [App::DocumentObjectGroupPython] H_element088  label="H_element : 049"  # scripted group (container) (typed FeaturePython)
  n = 8
  ref = H_element
FEATURE [App::DocumentObjectGroupPython] G4_PROPANE  # scripted group (container) (typed FeaturePython)
  Dunit = g/cm3
  Dvalue = 0.00187939
  Group = -> [C_element096,H_element088]
  conduct = 2
  density = 1
  expand = 3
  formula = G4_PROPANE
  name = G4_PROPANE
  specific = 4
FEATURE [App::DocumentObjectGroupPython] C_element097  label="C_element : 055"  # scripted group (container) (typed FeaturePython)
  n = 3
  ref = C_element
FEATURE [App::DocumentObjectGroupPython] H_element089  label="H_element : 050"  # scripted group (container) (typed FeaturePython)
  n = 8
  ref = H_element
FEATURE [App::DocumentObjectGroupPython] G4_lPROPANE  # scripted group (container) (typed FeaturePython)
  Dunit = g/cm3
  Dvalue = 0.43
  Group = -> [C_element097,H_element089]
  conduct = 2
  density = 1
  expand = 3
  formula = G4_lPROPANE
  name = G4_lPROPANE
  specific = 4
FEATURE [App::DocumentObjectGroupPython] C_element098  label="C_element : 056"  # scripted group (container) (typed FeaturePython)
  n = 3
  ref = C_element
FEATURE [App::DocumentObjectGroupPython] H_element090  label="H_element : 051"  # scripted group (container) (typed FeaturePython)
  n = 8
  ref = H_element
FEATURE [App::DocumentObjectGroupPython] O_element086  label="O_element : 047"  # scripted group (container) (typed FeaturePython)
  n = 1
  ref = O_element
FEATURE [App::DocumentObjectGroupPython] G4_N_PROPYL_ALCOHOL  label="G4_N-PROPYL_ALCOHOL"  # scripted group (container) (typed FeaturePython)
  Dunit = g/cm3
  Dvalue = 0.8035
  Group = -> [C_element098,H_element090,O_element086]
  conduct = 2
  density = 1
  expand = 3
  formula = G4_N-PROPYL_ALCOHOL
  name = G4_N-PROPYL_ALCOHOL
  specific = 4
FEATURE [App::DocumentObjectGroupPython] C_element099  label="C_element : 057"  # scripted group (container) (typed FeaturePython)
  n = 5
  ref = C_element
FEATURE [App::DocumentObjectGroupPython] H_element091  label="H_element : 052"  # scripted group (container) (typed FeaturePython)
  n = 5
  ref = H_element
FEATURE [App::DocumentObjectGroupPython] N_element038  label="N_element : 017"  # scripted group (container) (typed FeaturePython)
  n = 1
  ref = N_element
FEATURE [App::DocumentObjectGroupPython] G4_PYRIDINE  # scripted group (container) (typed FeaturePython)
  Dunit = g/cm3
  Dvalue = 0.9819
  Group = -> [C_element099,H_element091,N_element038]
  conduct = 2
  density = 1
  expand = 3
  formula = G4_PYRIDINE
  name = G4_PYRIDINE
  specific = 4
FEATURE [App::DocumentObjectGroupPython] H_element092  label="H_element : 0.144"  # scripted group (container) (typed FeaturePython)
  n = 0.143711
FEATURE [App::DocumentObjectGroupPython] C_element100  label="C_element : 0.856"  # scripted group (container) (typed FeaturePython)
  n = 0.856289
FEATURE [App::DocumentObjectGroupPython] G4_RUBBER_BUTYL  # scripted group (container) (typed FeaturePython)
  Dunit = g/cm3
  Dvalue = 0.92
  Group = -> [H_element092,C_element100]
  conduct = 2
  density = 1
  expand = 3
  formula = G4_RUBBER_BUTYL
  name = G4_RUBBER_BUTYL
  specific = 4
FEATURE [App::DocumentObjectGroupPython] H_element093  label="H_element : 0.118"  # scripted group (container) (typed FeaturePython)
  n = 0.118371
FEATURE [App::DocumentObjectGroupPython] C_element101  label="C_element : 0.882"  # scripted group (container) (typed FeaturePython)
  n = 0.881629
FEATURE [App::DocumentObjectGroupPython] G4_RUBBER_NATURAL  # scripted group (container) (typed FeaturePython)
  Dunit = g/cm3
  Dvalue = 0.92
  Group = -> [H_element093,C_element101]
  conduct = 2
  density = 1
  expand = 3
  formula = G4_RUBBER_NATURAL
  name = G4_RUBBER_NATURAL
  specific = 4
FEATURE [App::DocumentObjectGroupPython] H_element094  label="H_element : 0.145"  # scripted group (container) (typed FeaturePython)
  n = 0.05692
FEATURE [App::DocumentObjectGroupPython] C_element102  label="C_element : 0.543"  # scripted group (container) (typed FeaturePython)
  n = 0.542646
FEATURE [App::DocumentObjectGroupPython] Cl_element021  label="Cl_element : 0.400"  # scripted group (container) (typed FeaturePython)
  n = 0.400434
FEATURE [App::DocumentObjectGroupPython] G4_RUBBER_NEOPRENE  # scripted group (container) (typed FeaturePython)
  Dunit = g/cm3
  Dvalue = 1.23
  Group = -> [H_element094,C_element102,Cl_element021]
  conduct = 2
  density = 1
  expand = 3
  formula = G4_RUBBER_NEOPRENE
  name = G4_RUBBER_NEOPRENE
  specific = 4
FEATURE [App::DocumentObjectGroupPython] Si_element006  label="Si_element : 1"  # scripted group (container) (typed FeaturePython)
  n = 1
  ref = Si_element
FEATURE [App::DocumentObjectGroupPython] O_element087  label="O_element : 048"  # scripted group (container) (typed FeaturePython)
  n = 2
  ref = O_element
FEATURE [App::DocumentObjectGroupPython] G4_SILICON_DIOXIDE  # scripted group (container) (typed FeaturePython)
  Dunit = g/cm3
  Dvalue = 2.32
  Group = -> [Si_element006,O_element087]
  conduct = 2
  density = 1
  expand = 3
  formula = G4_SILICON_DIOXIDE
  name = G4_SILICON_DIOXIDE
  specific = 4
FEATURE [App::DocumentObjectGroupPython] Ag_element002  label="Ag_element : 1"  # scripted group (container) (typed FeaturePython)
  n = 1
  ref = Ag_element
FEATURE [App::DocumentObjectGroupPython] Br_element005  label="Br_element : 003"  # scripted group (container) (typed FeaturePython)
  n = 1
  ref = Br_element
FEATURE [App::DocumentObjectGroupPython] G4_SILVER_BROMIDE  # scripted group (container) (typed FeaturePython)
  Dunit = g/cm3
  Dvalue = 6.473
  Group = -> [Ag_element002,Br_element005]
  conduct = 2
  density = 1
  expand = 3
  formula = G4_SILVER_BROMIDE
  name = G4_SILVER_BROMIDE
  specific = 4
FEATURE [App::DocumentObjectGroupPython] Ag_element003  label="Ag_element : 002"  # scripted group (container) (typed FeaturePython)
  n = 1
  ref = Ag_element
FEATURE [App::DocumentObjectGroupPython] Cl_element022  label="Cl_element : 011"  # scripted group (container) (typed FeaturePython)
  n = 1
  ref = Cl_element
FEATURE [App::DocumentObjectGroupPython] G4_SILVER_CHLORIDE  # scripted group (container) (typed FeaturePython)
  Dunit = g/cm3
  Dvalue = 5.56
  Group = -> [Ag_element003,Cl_element022]
  conduct = 2
  density = 1
  expand = 3
  formula = G4_SILVER_CHLORIDE
  name = G4_SILVER_CHLORIDE
  specific = 4
FEATURE [App::DocumentObjectGroupPython] Br_element006  label="Br_element : 0.423"  # scripted group (container) (typed FeaturePython)
  n = 0.422895
FEATURE [App::DocumentObjectGroupPython] Ag_element004  label="Ag_element : 0.574"  # scripted group (container) (typed FeaturePython)
  n = 0.573748
FEATURE [App::DocumentObjectGroupPython] I_element007  label="I_element : 0.649"  # scripted group (container) (typed FeaturePython)
  n = 0.003357
FEATURE [App::DocumentObjectGroupPython] G4_SILVER_HALIDES  # scripted group (container) (typed FeaturePython)
  Dunit = g/cm3
  Dvalue = 6.47
  Group = -> [Br_element006,Ag_element004,I_element007]
  conduct = 2
  density = 1
  expand = 3
  formula = G4_SILVER_HALIDES
  name = G4_SILVER_HALIDES
  specific = 4
FEATURE [App::DocumentObjectGroupPython] Ag_element005  label="Ag_element : 003"  # scripted group (container) (typed FeaturePython)
  n = 1
  ref = Ag_element
FEATURE [App::DocumentObjectGroupPython] I_element008  label="I_element : 004"  # scripted group (container) (typed FeaturePython)
  n = 1
  ref = I_element
FEATURE [App::DocumentObjectGroupPython] G4_SILVER_IODIDE  # scripted group (container) (typed FeaturePython)
  Dunit = g/cm3
  Dvalue = 6.01
  Group = -> [Ag_element005,I_element008]
  conduct = 2
  density = 1
  expand = 3
  formula = G4_SILVER_IODIDE
  name = G4_SILVER_IODIDE
  specific = 4
FEATURE [App::DocumentObjectGroupPython] H_element095  label="H_element : 0.100"  # scripted group (container) (typed FeaturePython)
  n = 0.1
FEATURE [App::DocumentObjectGroupPython] C_element103  label="C_element : 0.204"  # scripted group (container) (typed FeaturePython)
  n = 0.204
FEATURE [App::DocumentObjectGroupPython] N_element039  label="N_element : 0.759"  # scripted group (container) (typed FeaturePython)
  n = 0.042
FEATURE [App::DocumentObjectGroupPython] O_element088  label="O_element : 0.645"  # scripted group (container) (typed FeaturePython)
  n = 0.645
FEATURE [App::DocumentObjectGroupPython] Na_element013  label="Na_element : 0.100"  # scripted group (container) (typed FeaturePython)
  n = 0.002
FEATURE [App::DocumentObjectGroupPython] P_element009  label="P_element : 0.107"  # scripted group (container) (typed FeaturePython)
  n = 0.001
FEATURE [App::DocumentObjectGroupPython] S_element020  label="S_element : 0.021"  # scripted group (container) (typed FeaturePython)
  n = 0.002
FEATURE [App::DocumentObjectGroupPython] Cl_element023  label="Cl_element : 0.590"  # scripted group (container) (typed FeaturePython)
  n = 0.003
FEATURE [App::DocumentObjectGroupPython] K_element010  label="K_element : 0.001"  # scripted group (container) (typed FeaturePython)
  n = 0.001
FEATURE [App::DocumentObjectGroupPython] G4_SKIN_ICRP  # scripted group (container) (typed FeaturePython)
  Dunit = g/cm3
  Dvalue = 1.09
  Group = -> [H_element095,C_element103,N_element039,O_element088,Na_element013,P_element009,S_element020,Cl_element023,K_element010]
  conduct = 2
  density = 1
  expand = 3
  formula = G4_SKIN_ICRP
  name = G4_SKIN_ICRP
  specific = 4
FEATURE [App::DocumentObjectGroupPython] Na_element014  label="Na_element : 2"  # scripted group (container) (typed FeaturePython)
  n = 2
  ref = Na_element
FEATURE [App::DocumentObjectGroupPython] C_element104  label="C_element : 058"  # scripted group (container) (typed FeaturePython)
  n = 1
  ref = C_element
FEATURE [App::DocumentObjectGroupPython] O_element089  label="O_element : 049"  # scripted group (container) (typed FeaturePython)
  n = 3
  ref = O_element
FEATURE [App::DocumentObjectGroupPython] G4_SODIUM_CARBONATE  # scripted group (container) (typed FeaturePython)
  Dunit = g/cm3
  Dvalue = 2.532
  Group = -> [Na_element014,C_element104,O_element089]
  conduct = 2
  density = 1
  expand = 3
  formula = G4_SODIUM_CARBONATE
  name = G4_SODIUM_CARBONATE
  specific = 4
FEATURE [App::DocumentObjectGroupPython] Na_element015  label="Na_element : 1"  # scripted group (container) (typed FeaturePython)
  n = 1
  ref = Na_element
FEATURE [App::DocumentObjectGroupPython] I_element009  label="I_element : 005"  # scripted group (container) (typed FeaturePython)
  n = 1
  ref = I_element
FEATURE [App::DocumentObjectGroupPython] G4_SODIUM_IODIDE  # scripted group (container) (typed FeaturePython)
  Dunit = g/cm3
  Dvalue = 3.667
  Group = -> [Na_element015,I_element009]
  conduct = 2
  density = 1
  expand = 3
  formula = G4_SODIUM_IODIDE
  name = G4_SODIUM_IODIDE
  specific = 4
FEATURE [App::DocumentObjectGroupPython] Na_element016  label="Na_element : 003"  # scripted group (container) (typed FeaturePython)
  n = 2
  ref = Na_element
FEATURE [App::DocumentObjectGroupPython] O_element090  label="O_element : 050"  # scripted group (container) (typed FeaturePython)
  n = 1
  ref = O_element
FEATURE [App::DocumentObjectGroupPython] G4_SODIUM_MONOXIDE  # scripted group (container) (typed FeaturePython)
  Dunit = g/cm3
  Dvalue = 2.27
  Group = -> [Na_element016,O_element090]
  conduct = 2
  density = 1
  expand = 3
  formula = G4_SODIUM_MONOXIDE
  name = G4_SODIUM_MONOXIDE
  specific = 4
FEATURE [App::DocumentObjectGroupPython] Na_element017  label="Na_element : 004"  # scripted group (container) (typed FeaturePython)
  n = 1
  ref = Na_element
FEATURE [App::DocumentObjectGroupPython] N_element040  label="N_element : 018"  # scripted group (container) (typed FeaturePython)
  n = 1
  ref = N_element
FEATURE [App::DocumentObjectGroupPython] O_element091  label="O_element : 051"  # scripted group (container) (typed FeaturePython)
  n = 3
  ref = O_element
FEATURE [App::DocumentObjectGroupPython] G4_SODIUM_NITRATE  # scripted group (container) (typed FeaturePython)
  Dunit = g/cm3
  Dvalue = 2.261
  Group = -> [Na_element017,N_element040,O_element091]
  conduct = 2
  density = 1
  expand = 3
  formula = G4_SODIUM_NITRATE
  name = G4_SODIUM_NITRATE
  specific = 4
FEATURE [App::DocumentObjectGroupPython] C_element105  label="C_element : 059"  # scripted group (container) (typed FeaturePython)
  n = 14
  ref = C_element
FEATURE [App::DocumentObjectGroupPython] H_element096  label="H_element : 053"  # scripted group (container) (typed FeaturePython)
  n = 12
  ref = H_element
FEATURE [App::DocumentObjectGroupPython] G4_STILBENE  # scripted group (container) (typed FeaturePython)
  Dunit = g/cm3
  Dvalue = 0.9707
  Group = -> [C_element105,H_element096]
  conduct = 2
  density = 1
  expand = 3
  formula = G4_STILBENE
  name = G4_STILBENE
  specific = 4
FEATURE [App::DocumentObjectGroupPython] C_element106  label="C_element : 12"  # scripted group (container) (typed FeaturePython)
  n = 12
  ref = C_element
FEATURE [App::DocumentObjectGroupPython] H_element097  label="H_element : 22"  # scripted group (container) (typed FeaturePython)
  n = 22
  ref = H_element
FEATURE [App::DocumentObjectGroupPython] O_element092  label="O_element : 11"  # scripted group (container) (typed FeaturePython)
  n = 11
  ref = O_element
FEATURE [App::DocumentObjectGroupPython] G4_SUCROSE  # scripted group (container) (typed FeaturePython)
  Dunit = g/cm3
  Dvalue = 1.5805
  Group = -> [C_element106,H_element097,O_element092]
  conduct = 2
  density = 1
  expand = 3
  formula = G4_SUCROSE
  name = G4_SUCROSE
  specific = 4
FEATURE [App::DocumentObjectGroupPython] C_element107  label="C_element : 18"  # scripted group (container) (typed FeaturePython)
  n = 18
  ref = C_element
FEATURE [App::DocumentObjectGroupPython] H_element098  label="H_element : 054"  # scripted group (container) (typed FeaturePython)
  n = 14
  ref = H_element
FEATURE [App::DocumentObjectGroupPython] G4_TERPHENYL  # scripted group (container) (typed FeaturePython)
  Dunit = g/cm3
  Dvalue = 1.24
  Group = -> [C_element107,H_element098]
  conduct = 2
  density = 1
  expand = 3
  formula = G4_TERPHENYL
  name = G4_TERPHENYL
  specific = 4
FEATURE [App::DocumentObjectGroupPython] H_element099  label="H_element : 0.146"  # scripted group (container) (typed FeaturePython)
  n = 0.106
FEATURE [App::DocumentObjectGroupPython] C_element108  label="C_element : 0.883"  # scripted group (container) (typed FeaturePython)
  n = 0.099
FEATURE [App::DocumentObjectGroupPython] N_element041  label="N_element : 0.020"  # scripted group (container) (typed FeaturePython)
  n = 0.02
FEATURE [App::DocumentObjectGroupPython] O_element093  label="O_element : 0.766"  # scripted group (container) (typed FeaturePython)
  n = 0.766
FEATURE [App::DocumentObjectGroupPython] Na_element018  label="Na_element : 0.101"  # scripted group (container) (typed FeaturePython)
  n = 0.002
FEATURE [App::DocumentObjectGroupPython] P_element010  label="P_element : 0.108"  # scripted group (container) (typed FeaturePython)
  n = 0.001
FEATURE [App::DocumentObjectGroupPython] S_element021  label="S_element : 0.022"  # scripted group (container) (typed FeaturePython)
  n = 0.002
FEATURE [App::DocumentObjectGroupPython] Cl_element024  label="Cl_element : 0.002"  # scripted group (container) (typed FeaturePython)
  n = 0.002
FEATURE [App::DocumentObjectGroupPython] K_element011  label="K_element : 0.017"  # scripted group (container) (typed FeaturePython)
  n = 0.002
FEATURE [App::DocumentObjectGroupPython] G4_TESTIS_ICRP  # scripted group (container) (typed FeaturePython)
  Dunit = g/cm3
  Dvalue = 1.04
  Group = -> [H_element099,C_element108,N_element041,O_element093,Na_element018,P_element010,S_element021,Cl_element024,K_element011]
  conduct = 2
  density = 1
  expand = 3
  formula = G4_TESTIS_ICRP
  name = G4_TESTIS_ICRP
  specific = 4
FEATURE [App::DocumentObjectGroupPython] C_element109  label="C_element : 060"  # scripted group (container) (typed FeaturePython)
  n = 2
  ref = C_element
FEATURE [App::DocumentObjectGroupPython] Cl_element025  label="Cl_element : 012"  # scripted group (container) (typed FeaturePython)
  n = 4
  ref = Cl_element
FEATURE [App::DocumentObjectGroupPython] G4_TETRACHLOROETHYLENE  # scripted group (container) (typed FeaturePython)
  Dunit = g/cm3
  Dvalue = 1.625
  Group = -> [C_element109,Cl_element025]
  conduct = 2
  density = 1
  expand = 3
  formula = G4_TETRACHLOROETHYLENE
  name = G4_TETRACHLOROETHYLENE
  specific = 4
FEATURE [App::DocumentObjectGroupPython] Tl_element001  label="Tl_element : 1"  # scripted group (container) (typed FeaturePython)
  n = 1
  ref = Tl_element
FEATURE [App::DocumentObjectGroupPython] Cl_element026  label="Cl_element : 013"  # scripted group (container) (typed FeaturePython)
  n = 1
  ref = Cl_element
FEATURE [App::DocumentObjectGroupPython] G4_THALLIUM_CHLORIDE  # scripted group (container) (typed FeaturePython)
  Dunit = g/cm3
  Dvalue = 7.004
  Group = -> [Tl_element001,Cl_element026]
  conduct = 2
  density = 1
  expand = 3
  formula = G4_THALLIUM_CHLORIDE
  name = G4_THALLIUM_CHLORIDE
  specific = 4
FEATURE [App::DocumentObjectGroupPython] H_element100  label="H_element : 0.147"  # scripted group (container) (typed FeaturePython)
  n = 0.105
FEATURE [App::DocumentObjectGroupPython] C_element110  label="C_element : 0.256"  # scripted group (container) (typed FeaturePython)
  n = 0.256
FEATURE [App::DocumentObjectGroupPython] N_element042  label="N_element : 0.760"  # scripted group (container) (typed FeaturePython)
  n = 0.027
FEATURE [App::DocumentObjectGroupPython] O_element094  label="O_element : 0.602"  # scripted group (container) (typed FeaturePython)
  n = 0.602
FEATURE [App::DocumentObjectGroupPython] Na_element019  label="Na_element : 0.102"  # scripted group (container) (typed FeaturePython)
  n = 0.001
FEATURE [App::DocumentObjectGroupPython] P_element011  label="P_element : 0.109"  # scripted group (container) (typed FeaturePython)
  n = 0.002
FEATURE [App::DocumentObjectGroupPython] S_element022  label="S_element : 0.023"  # scripted group (container) (typed FeaturePython)
  n = 0.003
FEATURE [App::DocumentObjectGroupPython] Cl_element027  label="Cl_element : 0.591"  # scripted group (container) (typed FeaturePython)
  n = 0.002
FEATURE [App::DocumentObjectGroupPython] K_element012  label="K_element : 0.018"  # scripted group (container) (typed FeaturePython)
  n = 0.002
FEATURE [App::DocumentObjectGroupPython] G4_TISSUE_SOFT_ICRP  # scripted group (container) (typed FeaturePython)
  Dunit = g/cm3
  Dvalue = 1.03
  Group = -> [H_element100,C_element110,N_element042,O_element094,Na_element019,P_element011,S_element022,Cl_element027,K_element012]
  conduct = 2
  density = 1
  expand = 3
  formula = G4_TISSUE_SOFT_ICRP
  name = G4_TISSUE_SOFT_ICRP
  specific = 4
FEATURE [App::DocumentObjectGroupPython] H_element101  label="H_element : 0.148"  # scripted group (container) (typed FeaturePython)
  n = 0.101
FEATURE [App::DocumentObjectGroupPython] C_element111  label="C_element : 0.111"  # scripted group (container) (typed FeaturePython)
  n = 0.111
FEATURE [App::DocumentObjectGroupPython] N_element043  label="N_element : 0.026"  # scripted group (container) (typed FeaturePython)
  n = 0.026
FEATURE [App::DocumentObjectGroupPython] O_element095  label="O_element : 0.762"  # scripted group (container) (typed FeaturePython)
  n = 0.762
FEATURE [App::DocumentObjectGroupPython] G4_TISSUE_SOFT_ICRU_4  label="G4_TISSUE_SOFT_ICRU-4"  # scripted group (container) (typed FeaturePython)
  Dunit = g/cm3
  Dvalue = 1
  Group = -> [H_element101,C_element111,N_element043,O_element095]
  conduct = 2
  density = 1
  expand = 3
  formula = G4_TISSUE_SOFT_ICRU-4
  name = G4_TISSUE_SOFT_ICRU-4
  specific = 4
FEATURE [App::DocumentObjectGroupPython] H_element102  label="H_element : 0.149"  # scripted group (container) (typed FeaturePython)
  n = 0.101869
FEATURE [App::DocumentObjectGroupPython] C_element112  label="C_element : 0.456"  # scripted group (container) (typed FeaturePython)
  n = 0.456179
FEATURE [App::DocumentObjectGroupPython] N_element044  label="N_element : 0.761"  # scripted group (container) (typed FeaturePython)
  n = 0.035172
FEATURE [App::DocumentObjectGroupPython] O_element096  label="O_element : 0.407"  # scripted group (container) (typed FeaturePython)
  n = 0.40678
FEATURE [App::DocumentObjectGroupPython] G4_TISSUE_METHANE  label="G4_TISSUE-METHANE"  # scripted group (container) (typed FeaturePython)
  Dunit = g/cm3
  Dvalue = 0.00106409
  Group = -> [H_element102,C_element112,N_element044,O_element096]
  conduct = 2
  density = 1
  expand = 3
  formula = G4_TISSUE-METHANE
  name = G4_TISSUE-METHANE
  specific = 4
FEATURE [App::DocumentObjectGroupPython] H_element103  label="H_element : 0.103"  # scripted group (container) (typed FeaturePython)
  n = 0.102672
FEATURE [App::DocumentObjectGroupPython] C_element113  label="C_element : 0.569"  # scripted group (container) (typed FeaturePython)
  n = 0.56894
FEATURE [App::DocumentObjectGroupPython] N_element045  label="N_element : 0.762"  # scripted group (container) (typed FeaturePython)
  n = 0.035022
FEATURE [App::DocumentObjectGroupPython] O_element097  label="O_element : 0.293"  # scripted group (container) (typed FeaturePython)
  n = 0.293366
FEATURE [App::DocumentObjectGroupPython] G4_TISSUE_PROPANE  label="G4_TISSUE-PROPANE"  # scripted group (container) (typed FeaturePython)
  Dunit = g/cm3
  Dvalue = 0.00182628
  Group = -> [H_element103,C_element113,N_element045,O_element097]
  conduct = 2
  density = 1
  expand = 3
  formula = G4_TISSUE-PROPANE
  name = G4_TISSUE-PROPANE
  specific = 4
FEATURE [App::DocumentObjectGroupPython] Ti_element003  label="Ti_element : 1"  # scripted group (container) (typed FeaturePython)
  n = 1
  ref = Ti_element
FEATURE [App::DocumentObjectGroupPython] O_element098  label="O_element : 052"  # scripted group (container) (typed FeaturePython)
  n = 2
  ref = O_element
FEATURE [App::DocumentObjectGroupPython] G4_TITANIUM_DIOXIDE  # scripted group (container) (typed FeaturePython)
  Dunit = g/cm3
  Dvalue = 4.26
  Group = -> [Ti_element003,O_element098]
  conduct = 2
  density = 1
  expand = 3
  formula = G4_TITANIUM_DIOXIDE
  name = G4_TITANIUM_DIOXIDE
  specific = 4
FEATURE [App::DocumentObjectGroupPython] C_element114  label="C_element : 061"  # scripted group (container) (typed FeaturePython)
  n = 7
  ref = C_element
FEATURE [App::DocumentObjectGroupPython] H_element104  label="H_element : 055"  # scripted group (container) (typed FeaturePython)
  n = 8
  ref = H_element
FEATURE [App::DocumentObjectGroupPython] G4_TOLUENE  # scripted group (container) (typed FeaturePython)
  Dunit = g/cm3
  Dvalue = 0.8669
  Group = -> [C_element114,H_element104]
  conduct = 2
  density = 1
  expand = 3
  formula = G4_TOLUENE
  name = G4_TOLUENE
  specific = 4
FEATURE [App::DocumentObjectGroupPython] C_element115  label="C_element : 062"  # scripted group (container) (typed FeaturePython)
  n = 2
  ref = C_element
FEATURE [App::DocumentObjectGroupPython] H_element105  label="H_element : 056"  # scripted group (container) (typed FeaturePython)
  n = 1
  ref = H_element
FEATURE [App::DocumentObjectGroupPython] Cl_element028  label="Cl_element : 014"  # scripted group (container) (typed FeaturePython)
  n = 3
  ref = Cl_element
FEATURE [App::DocumentObjectGroupPython] G4_TRICHLOROETHYLENE  # scripted group (container) (typed FeaturePython)
  Dunit = g/cm3
  Dvalue = 1.46
  Group = -> [C_element115,H_element105,Cl_element028]
  conduct = 2
  density = 1
  expand = 3
  formula = G4_TRICHLOROETHYLENE
  name = G4_TRICHLOROETHYLENE
  specific = 4
FEATURE [App::DocumentObjectGroupPython] C_element116  label="C_element : 063"  # scripted group (container) (typed FeaturePython)
  n = 6
  ref = C_element
FEATURE [App::DocumentObjectGroupPython] H_element106  label="H_element : 15"  # scripted group (container) (typed FeaturePython)
  n = 15
  ref = H_element
FEATURE [App::DocumentObjectGroupPython] O_element099  label="O_element : 053"  # scripted group (container) (typed FeaturePython)
  n = 4
  ref = O_element
FEATURE [App::DocumentObjectGroupPython] P_element012  label="P_element : 1"  # scripted group (container) (typed FeaturePython)
  n = 1
  ref = P_element
FEATURE [App::DocumentObjectGroupPython] G4_TRIETHYL_PHOSPHATE  # scripted group (container) (typed FeaturePython)
  Dunit = g/cm3
  Dvalue = 1.07
  Group = -> [C_element116,H_element106,O_element099,P_element012]
  conduct = 2
  density = 1
  expand = 3
  formula = G4_TRIETHYL_PHOSPHATE
  name = G4_TRIETHYL_PHOSPHATE
  specific = 4
FEATURE [App::DocumentObjectGroupPython] W_element003  label="W_element : 003"  # scripted group (container) (typed FeaturePython)
  n = 1
  ref = W_element
FEATURE [App::DocumentObjectGroupPython] F_element017  label="F_element : 6"  # scripted group (container) (typed FeaturePython)
  n = 6
  ref = F_element
FEATURE [App::DocumentObjectGroupPython] G4_TUNGSTEN_HEXAFLUORIDE  # scripted group (container) (typed FeaturePython)
  Dunit = g/cm3
  Dvalue = 2.4
  Group = -> [W_element003,F_element017]
  conduct = 2
  density = 1
  expand = 3
  formula = G4_TUNGSTEN_HEXAFLUORIDE
  name = G4_TUNGSTEN_HEXAFLUORIDE
  specific = 4
FEATURE [App::DocumentObjectGroupPython] U_element001  label="U_element : 1"  # scripted group (container) (typed FeaturePython)
  n = 1
  ref = U_element
FEATURE [App::DocumentObjectGroupPython] C_element117  label="C_element : 064"  # scripted group (container) (typed FeaturePython)
  n = 2
  ref = C_element
FEATURE [App::DocumentObjectGroupPython] G4_URANIUM_DICARBIDE  # scripted group (container) (typed FeaturePython)
  Dunit = g/cm3
  Dvalue = 11.28
  Group = -> [U_element001,C_element117]
  conduct = 2
  density = 1
  expand = 3
  formula = G4_URANIUM_DICARBIDE
  name = G4_URANIUM_DICARBIDE
  specific = 4
FEATURE [App::DocumentObjectGroupPython] U_element002  label="U_element : 002"  # scripted group (container) (typed FeaturePython)
  n = 1
  ref = U_element
FEATURE [App::DocumentObjectGroupPython] C_element118  label="C_element : 065"  # scripted group (container) (typed FeaturePython)
  n = 1
  ref = C_element
FEATURE [App::DocumentObjectGroupPython] G4_URANIUM_MONOCARBIDE  # scripted group (container) (typed FeaturePython)
  Dunit = g/cm3
  Dvalue = 13.63
  Group = -> [U_element002,C_element118]
  conduct = 2
  density = 1
  expand = 3
  formula = G4_URANIUM_MONOCARBIDE
  name = G4_URANIUM_MONOCARBIDE
  specific = 4
FEATURE [App::DocumentObjectGroupPython] U_element003  label="U_element : 003"  # scripted group (container) (typed FeaturePython)
  n = 1
  ref = U_element
FEATURE [App::DocumentObjectGroupPython] O_element100  label="O_element : 054"  # scripted group (container) (typed FeaturePython)
  n = 2
  ref = O_element
FEATURE [App::DocumentObjectGroupPython] G4_URANIUM_OXIDE  # scripted group (container) (typed FeaturePython)
  Dunit = g/cm3
  Dvalue = 10.96
  Group = -> [U_element003,O_element100]
  conduct = 2
  density = 1
  expand = 3
  formula = G4_URANIUM_OXIDE
  name = G4_URANIUM_OXIDE
  specific = 4
FEATURE [App::DocumentObjectGroupPython] C_element119  label="C_element : 066"  # scripted group (container) (typed FeaturePython)
  n = 1
  ref = C_element
FEATURE [App::DocumentObjectGroupPython] H_element107  label="H_element : 057"  # scripted group (container) (typed FeaturePython)
  n = 4
  ref = H_element
FEATURE [App::DocumentObjectGroupPython] N_element046  label="N_element : 019"  # scripted group (container) (typed FeaturePython)
  n = 2
  ref = N_element
FEATURE [App::DocumentObjectGroupPython] O_element101  label="O_element : 055"  # scripted group (container) (typed FeaturePython)
  n = 1
  ref = O_element
FEATURE [App::DocumentObjectGroupPython] G4_UREA  # scripted group (container) (typed FeaturePython)
  Dunit = g/cm3
  Dvalue = 1.323
  Group = -> [C_element119,H_element107,N_element046,O_element101]
  conduct = 2
  density = 1
  expand = 3
  formula = G4_UREA
  name = G4_UREA
  specific = 4
FEATURE [App::DocumentObjectGroupPython] C_element120  label="C_element : 067"  # scripted group (container) (typed FeaturePython)
  n = 5
  ref = C_element
FEATURE [App::DocumentObjectGroupPython] H_element108  label="H_element : 058"  # scripted group (container) (typed FeaturePython)
  n = 11
  ref = H_element
FEATURE [App::DocumentObjectGroupPython] N_element047  label="N_element : 020"  # scripted group (container) (typed FeaturePython)
  n = 1
  ref = N_element
FEATURE [App::DocumentObjectGroupPython] O_element102  label="O_element : 056"  # scripted group (container) (typed FeaturePython)
  n = 2
  ref = O_element
FEATURE [App::DocumentObjectGroupPython] G4_VALINE  # scripted group (container) (typed FeaturePython)
  Dunit = g/cm3
  Dvalue = 1.23
  Group = -> [C_element120,H_element108,N_element047,O_element102]
  conduct = 2
  density = 1
  expand = 3
  formula = G4_VALINE
  name = G4_VALINE
  specific = 4
FEATURE [App::DocumentObjectGroupPython] H_element109  label="H_element : 0.009"  # scripted group (container) (typed FeaturePython)
  n = 0.009417
FEATURE [App::DocumentObjectGroupPython] C_element121  label="C_element : 0.281"  # scripted group (container) (typed FeaturePython)
  n = 0.280555
FEATURE [App::DocumentObjectGroupPython] F_element018  label="F_element : 0.710"  # scripted group (container) (typed FeaturePython)
  n = 0.710028
FEATURE [App::DocumentObjectGroupPython] G4_VITON  # scripted group (container) (typed FeaturePython)
  Dunit = g/cm3
  Dvalue = 1.8
  Group = -> [H_element109,C_element121,F_element018]
  conduct = 2
  density = 1
  expand = 3
  formula = G4_VITON
  name = G4_VITON
  specific = 4
FEATURE [App::DocumentObjectGroupPython] H_element110  label="H_element : 059"  # scripted group (container) (typed FeaturePython)
  n = 2
  ref = H_element
FEATURE [App::DocumentObjectGroupPython] O_element103  label="O_element : 057"  # scripted group (container) (typed FeaturePython)
  n = 1
  ref = O_element
FEATURE [App::DocumentObjectGroupPython] G4_WATER  # scripted group (container) (typed FeaturePython)
  Dunit = g/cm3
  Dvalue = 1
  Group = -> [H_element110,O_element103]
  conduct = 2
  density = 1
  expand = 3
  formula = G4_WATER
  name = G4_WATER
  specific = 4
FEATURE [App::DocumentObjectGroupPython] H_element111  label="H_element : 060"  # scripted group (container) (typed FeaturePython)
  n = 2
  ref = H_element
FEATURE [App::DocumentObjectGroupPython] O_element104  label="O_element : 058"  # scripted group (container) (typed FeaturePython)
  n = 1
  ref = O_element
FEATURE [App::DocumentObjectGroupPython] G4_WATER_VAPOR  # scripted group (container) (typed FeaturePython)
  Dunit = g/cm3
  Dvalue = 0.000756182
  Group = -> [H_element111,O_element104]
  conduct = 2
  density = 1
  expand = 3
  formula = G4_WATER_VAPOR
  name = G4_WATER_VAPOR
  specific = 4
FEATURE [App::DocumentObjectGroupPython] C_element122  label="C_element : 068"  # scripted group (container) (typed FeaturePython)
  n = 8
  ref = C_element
FEATURE [App::DocumentObjectGroupPython] H_element112  label="H_element : 061"  # scripted group (container) (typed FeaturePython)
  n = 10
  ref = H_element
FEATURE [App::DocumentObjectGroupPython] G4_XYLENE  # scripted group (container) (typed FeaturePython)
  Dunit = g/cm3
  Dvalue = 0.87
  Group = -> [C_element122,H_element112]
  conduct = 2
  density = 1
  expand = 3
  formula = G4_XYLENE
  name = G4_XYLENE
  specific = 4
FEATURE [App::DocumentObjectGroupPython] C_element123  label="C_element : 069"  # scripted group (container) (typed FeaturePython)
  n = 1
  ref = C_element
FEATURE [App::DocumentObjectGroupPython] G4_GRAPHITE  # scripted group (container) (typed FeaturePython)
  Dunit = g/cm3
  Dvalue = 2.21
  Group = -> [C_element123]
  conduct = 2
  density = 1
  expand = 3
  formula = G4_GRAPHITE
  name = G4_GRAPHITE
  specific = 4
FEATURE [App::DocumentObjectGroupPython] NIST  # scripted group (container) (typed FeaturePython)
  Group = -> [G4_A_150_TISSUE,G4_ACETONE,G4_ACETYLENE,G4_ADENINE,G4_ADIPOSE_TISSUE_ICRP,G4_AIR,G4_ALANINE,G4_ALUMINUM_OXIDE,G4_AMBER,G4_AMMONIA,G4_ANILINE,G4_ANTHRACENE,G4_B_100_BONE,G4_BAKELITE,G4_BARIUM_FLUORIDE,G4_BARIUM_SULFATE,G4_BENZENE,G4_BERYLLIUM_OXIDE,G4_BGO,G4_BLOOD_ICRP,G4_BONE_COMPACT_ICRU,G4_BONE_CORTICAL_ICRP,G4_BORON_CARBIDE,G4_BORON_OXIDE,G4_BRAIN_ICRP,G4_BUTANE,G4_N_BUTYL_ALCOHOL,G4_C_552,+152 more]
FEATURE [App::DocumentObjectGroupPython] H_element113  label="H_element : 062"  # scripted group (container) (typed FeaturePython)
  n = 1
  ref = H_element
FEATURE [App::DocumentObjectGroupPython] G4_H  # scripted group (container) (typed FeaturePython)
  Dunit = g/cm3
  Dvalue = 8.3748e-05
  Group = -> [H_element113]
  conduct = 2
  density = 1
  expand = 3
  formula = H
  name = G4_H
  specific = 4
FEATURE [App::DocumentObjectGroupPython] He_element001  label="He_element : 1"  # scripted group (container) (typed FeaturePython)
  n = 1
  ref = He_element
FEATURE [App::DocumentObjectGroupPython] G4_He  # scripted group (container) (typed FeaturePython)
  Dunit = g/cm3
  Dvalue = 0.000166322
  Group = -> [He_element001]
  conduct = 2
  density = 1
  expand = 3
  formula = He
  name = G4_He
  specific = 4
FEATURE [App::DocumentObjectGroupPython] Li_element008  label="Li_element : 008"  # scripted group (container) (typed FeaturePython)
  n = 1
  ref = Li_element
FEATURE [App::DocumentObjectGroupPython] G4_Li  # scripted group (container) (typed FeaturePython)
  Dunit = g/cm3
  Dvalue = 0.534
  Group = -> [Li_element008]
  conduct = 2
  density = 1
  expand = 3
  formula = Li
  name = G4_Li
  specific = 4
FEATURE [App::DocumentObjectGroupPython] Be_element002  label="Be_element : 002"  # scripted group (container) (typed FeaturePython)
  n = 1
  ref = Be_element
FEATURE [App::DocumentObjectGroupPython] G4_Be  # scripted group (container) (typed FeaturePython)
  Dunit = g/cm3
  Dvalue = 1.848
  Group = -> [Be_element002]
  conduct = 2
  density = 1
  expand = 3
  formula = Be
  name = G4_Be
  specific = 4
FEATURE [App::DocumentObjectGroupPython] B_element007  label="B_element : 007"  # scripted group (container) (typed FeaturePython)
  n = 1
  ref = B_element
FEATURE [App::DocumentObjectGroupPython] G4_B  # scripted group (container) (typed FeaturePython)
  Dunit = g/cm3
  Dvalue = 2.37
  Group = -> [B_element007]
  conduct = 2
  density = 1
  expand = 3
  formula = B
  name = G4_B
  specific = 4
FEATURE [App::DocumentObjectGroupPython] C_element124  label="C_element : 070"  # scripted group (container) (typed FeaturePython)
  n = 1
  ref = C_element
FEATURE [App::DocumentObjectGroupPython] G4_C  # scripted group (container) (typed FeaturePython)
  Dunit = g/cm3
  Dvalue = 2
  Group = -> [C_element124]
  conduct = 2
  density = 1
  expand = 3
  formula = C
  name = G4_C
  specific = 4
FEATURE [App::DocumentObjectGroupPython] N_element048  label="N_element : 021"  # scripted group (container) (typed FeaturePython)
  n = 1
  ref = N_element
FEATURE [App::DocumentObjectGroupPython] G4_N  # scripted group (container) (typed FeaturePython)
  Dunit = g/cm3
  Dvalue = 0.0011652
  Group = -> [N_element048]
  conduct = 2
  density = 1
  expand = 3
  formula = N
  name = G4_N
  specific = 4
FEATURE [App::DocumentObjectGroupPython] O_element105  label="O_element : 059"  # scripted group (container) (typed FeaturePython)
  n = 1
  ref = O_element
FEATURE [App::DocumentObjectGroupPython] G4_O  # scripted group (container) (typed FeaturePython)
  Dunit = g/cm3
  Dvalue = 0.00133151
  Group = -> [O_element105]
  conduct = 2
  density = 1
  expand = 3
  formula = O
  name = G4_O
  specific = 4
FEATURE [App::DocumentObjectGroupPython] F_element019  label="F_element : 008"  # scripted group (container) (typed FeaturePython)
  n = 1
  ref = F_element
FEATURE [App::DocumentObjectGroupPython] G4_F  # scripted group (container) (typed FeaturePython)
  Dunit = g/cm3
  Dvalue = 0.00158029
  Group = -> [F_element019]
  conduct = 2
  density = 1
  expand = 3
  formula = F
  name = G4_F
  specific = 4
FEATURE [App::DocumentObjectGroupPython] Ne_element001  label="Ne_element : 1"  # scripted group (container) (typed FeaturePython)
  n = 1
  ref = Ne_element
FEATURE [App::DocumentObjectGroupPython] G4_Ne  # scripted group (container) (typed FeaturePython)
  Dunit = g/cm3
  Dvalue = 0.000838505
  Group = -> [Ne_element001]
  conduct = 2
  density = 1
  expand = 3
  formula = Ne
  name = G4_Ne
  specific = 4
FEATURE [App::DocumentObjectGroupPython] Na_element020  label="Na_element : 005"  # scripted group (container) (typed FeaturePython)
  n = 1
  ref = Na_element
FEATURE [App::DocumentObjectGroupPython] G4_Na  # scripted group (container) (typed FeaturePython)
  Dunit = g/cm3
  Dvalue = 0.971
  Group = -> [Na_element020]
  conduct = 2
  density = 1
  expand = 3
  formula = Na
  name = G4_Na
  specific = 4
FEATURE [App::DocumentObjectGroupPython] Mg_element011  label="Mg_element : 005"  # scripted group (container) (typed FeaturePython)
  n = 1
  ref = Mg_element
FEATURE [App::DocumentObjectGroupPython] G4_Mg  # scripted group (container) (typed FeaturePython)
  Dunit = g/cm3
  Dvalue = 1.74
  Group = -> [Mg_element011]
  conduct = 2
  density = 1
  expand = 3
  formula = Mg
  name = G4_Mg
  specific = 4
FEATURE [App::DocumentObjectGroupPython] Al_element004  label="Al_element : 1"  # scripted group (container) (typed FeaturePython)
  n = 1
  ref = Al_element
FEATURE [App::DocumentObjectGroupPython] G4_Al  # scripted group (container) (typed FeaturePython)
  Dunit = g/cm3
  Dvalue = 2.699
  Group = -> [Al_element004]
  conduct = 2
  density = 1
  expand = 3
  formula = Al
  name = G4_Al
  specific = 4
FEATURE [App::DocumentObjectGroupPython] Si_element007  label="Si_element : 002"  # scripted group (container) (typed FeaturePython)
  n = 1
  ref = Si_element
FEATURE [App::DocumentObjectGroupPython] G4_Si  # scripted group (container) (typed FeaturePython)
  Dunit = g/cm3
  Dvalue = 2.33
  Group = -> [Si_element007]
  conduct = 2
  density = 1
  expand = 3
  formula = Si
  name = G4_Si
  specific = 4
FEATURE [App::DocumentObjectGroupPython] P_element013  label="P_element : 002"  # scripted group (container) (typed FeaturePython)
  n = 1
  ref = P_element
FEATURE [App::DocumentObjectGroupPython] G4_P  # scripted group (container) (typed FeaturePython)
  Dunit = g/cm3
  Dvalue = 2.2
  Group = -> [P_element013]
  conduct = 2
  density = 1
  expand = 3
  formula = P
  name = G4_P
  specific = 4
FEATURE [App::DocumentObjectGroupPython] S_element023  label="S_element : 007"  # scripted group (container) (typed FeaturePython)
  n = 1
  ref = S_element
FEATURE [App::DocumentObjectGroupPython] G4_S  # scripted group (container) (typed FeaturePython)
  Dunit = g/cm3
  Dvalue = 2
  Group = -> [S_element023]
  conduct = 2
  density = 1
  expand = 3
  formula = S
  name = G4_S
  specific = 4
FEATURE [App::DocumentObjectGroupPython] Cl_element029  label="Cl_element : 015"  # scripted group (container) (typed FeaturePython)
  n = 1
  ref = Cl_element
FEATURE [App::DocumentObjectGroupPython] G4_Cl  # scripted group (container) (typed FeaturePython)
  Dunit = g/cm3
  Dvalue = 0.00299473
  Group = -> [Cl_element029]
  conduct = 2
  density = 1
  expand = 3
  formula = Cl
  name = G4_Cl
  specific = 4
FEATURE [App::DocumentObjectGroupPython] Ar_element002  label="Ar_element : 1"  # scripted group (container) (typed FeaturePython)
  n = 1
  ref = Ar_element
FEATURE [App::DocumentObjectGroupPython] G4_Ar  # scripted group (container) (typed FeaturePython)
  Dunit = g/cm3
  Dvalue = 0.00166201
  Group = -> [Ar_element002]
  conduct = 2
  density = 1
  expand = 3
  formula = Ar
  name = G4_Ar
  specific = 4
FEATURE [App::DocumentObjectGroupPython] K_element013  label="K_element : 003"  # scripted group (container) (typed FeaturePython)
  n = 1
  ref = K_element
FEATURE [App::DocumentObjectGroupPython] G4_K  # scripted group (container) (typed FeaturePython)
  Dunit = g/cm3
  Dvalue = 0.862
  Group = -> [K_element013]
  conduct = 2
  density = 1
  expand = 3
  formula = K
  name = G4_K
  specific = 4
FEATURE [App::DocumentObjectGroupPython] Ca_element014  label="Ca_element : 007"  # scripted group (container) (typed FeaturePython)
  n = 1
  ref = Ca_element
FEATURE [App::DocumentObjectGroupPython] G4_Ca  # scripted group (container) (typed FeaturePython)
  Dunit = g/cm3
  Dvalue = 1.55
  Group = -> [Ca_element014]
  conduct = 2
  density = 1
  expand = 3
  formula = Ca
  name = G4_Ca
  specific = 4
FEATURE [App::DocumentObjectGroupPython] Sc_element001  label="Sc_element : 1"  # scripted group (container) (typed FeaturePython)
  n = 1
  ref = Sc_element
FEATURE [App::DocumentObjectGroupPython] G4_Sc  # scripted group (container) (typed FeaturePython)
  Dunit = g/cm3
  Dvalue = 2.989
  Group = -> [Sc_element001]
  conduct = 2
  density = 1
  expand = 3
  formula = Sc
  name = G4_Sc
  specific = 4
FEATURE [App::DocumentObjectGroupPython] Ti_element004  label="Ti_element : 002"  # scripted group (container) (typed FeaturePython)
  n = 1
  ref = Ti_element
FEATURE [App::DocumentObjectGroupPython] G4_Ti  # scripted group (container) (typed FeaturePython)
  Dunit = g/cm3
  Dvalue = 4.54
  Group = -> [Ti_element004]
  conduct = 2
  density = 1
  expand = 3
  formula = Ti
  name = G4_Ti
  specific = 4
FEATURE [App::DocumentObjectGroupPython] V_element001  label="V_element : 1"  # scripted group (container) (typed FeaturePython)
  n = 1
  ref = V_element
FEATURE [App::DocumentObjectGroupPython] G4_V  # scripted group (container) (typed FeaturePython)
  Dunit = g/cm3
  Dvalue = 6.11
  Group = -> [V_element001]
  conduct = 2
  density = 1
  expand = 3
  formula = V
  name = G4_V
  specific = 4
FEATURE [App::DocumentObjectGroupPython] Cr_element001  label="Cr_element : 1"  # scripted group (container) (typed FeaturePython)
  n = 1
  ref = Cr_element
FEATURE [App::DocumentObjectGroupPython] G4_Cr  # scripted group (container) (typed FeaturePython)
  Dunit = g/cm3
  Dvalue = 7.18
  Group = -> [Cr_element001]
  conduct = 2
  density = 1
  expand = 3
  formula = Cr
  name = G4_Cr
  specific = 4
FEATURE [App::DocumentObjectGroupPython] Mn_element001  label="Mn_element : 1"  # scripted group (container) (typed FeaturePython)
  n = 1
  ref = Mn_element
FEATURE [App::DocumentObjectGroupPython] G4_Mn  # scripted group (container) (typed FeaturePython)
  Dunit = g/cm3
  Dvalue = 7.44
  Group = -> [Mn_element001]
  conduct = 2
  density = 1
  expand = 3
  formula = Mn
  name = G4_Mn
  specific = 4
FEATURE [App::DocumentObjectGroupPython] Fe_element007  label="Fe_element : 004"  # scripted group (container) (typed FeaturePython)
  n = 1
  ref = Fe_element
FEATURE [App::DocumentObjectGroupPython] G4_Fe  # scripted group (container) (typed FeaturePython)
  Dunit = g/cm3
  Dvalue = 7.874
  Group = -> [Fe_element007]
  conduct = 2
  density = 1
  expand = 3
  formula = Fe
  name = G4_Fe
  specific = 4
FEATURE [App::DocumentObjectGroupPython] Co_element001  label="Co_element : 1"  # scripted group (container) (typed FeaturePython)
  n = 1
  ref = Co_element
FEATURE [App::DocumentObjectGroupPython] G4_Co  # scripted group (container) (typed FeaturePython)
  Dunit = g/cm3
  Dvalue = 8.9
  Group = -> [Co_element001]
  conduct = 2
  density = 1
  expand = 3
  formula = Co
  name = G4_Co
  specific = 4
FEATURE [App::DocumentObjectGroupPython] Ni_element001  label="Ni_element : 1"  # scripted group (container) (typed FeaturePython)
  n = 1
  ref = Ni_element
FEATURE [App::DocumentObjectGroupPython] G4_Ni  # scripted group (container) (typed FeaturePython)
  Dunit = g/cm3
  Dvalue = 8.902
  Group = -> [Ni_element001]
  conduct = 2
  density = 1
  expand = 3
  formula = Ni
  name = G4_Ni
  specific = 4
FEATURE [App::DocumentObjectGroupPython] Cu_element001  label="Cu_element : 1"  # scripted group (container) (typed FeaturePython)
  n = 1
  ref = Cu_element
FEATURE [App::DocumentObjectGroupPython] G4_Cu  # scripted group (container) (typed FeaturePython)
  Dunit = g/cm3
  Dvalue = 8.96
  Group = -> [Cu_element001]
  conduct = 2
  density = 1
  expand = 3
  formula = Cu
  name = G4_Cu
  specific = 4
FEATURE [App::DocumentObjectGroupPython] Zn_element001  label="Zn_element : 1"  # scripted group (container) (typed FeaturePython)
  n = 1
  ref = Zn_element
FEATURE [App::DocumentObjectGroupPython] G4_Zn  # scripted group (container) (typed FeaturePython)
  Dunit = g/cm3
  Dvalue = 7.133
  Group = -> [Zn_element001]
  conduct = 2
  density = 1
  expand = 3
  formula = Zn
  name = G4_Zn
  specific = 4
FEATURE [App::DocumentObjectGroupPython] Ga_element002  label="Ga_element : 002"  # scripted group (container) (typed FeaturePython)
  n = 1
  ref = Ga_element
FEATURE [App::DocumentObjectGroupPython] G4_Ga  # scripted group (container) (typed FeaturePython)
  Dunit = g/cm3
  Dvalue = 5.904
  Group = -> [Ga_element002]
  conduct = 2
  density = 1
  expand = 3
  formula = Ga
  name = G4_Ga
  specific = 4
FEATURE [App::DocumentObjectGroupPython] Ge_element002  label="Ge_element : 1"  # scripted group (container) (typed FeaturePython)
  n = 1
  ref = Ge_element
FEATURE [App::DocumentObjectGroupPython] G4_Ge  # scripted group (container) (typed FeaturePython)
  Dunit = g/cm3
  Dvalue = 5.323
  Group = -> [Ge_element002]
  conduct = 2
  density = 1
  expand = 3
  formula = Ge
  name = G4_Ge
  specific = 4
FEATURE [App::DocumentObjectGroupPython] As_element003  label="As_element : 002"  # scripted group (container) (typed FeaturePython)
  n = 1
  ref = As_element
FEATURE [App::DocumentObjectGroupPython] G4_As  # scripted group (container) (typed FeaturePython)
  Dunit = g/cm3
  Dvalue = 5.73
  Group = -> [As_element003]
  conduct = 2
  density = 1
  expand = 3
  formula = As
  name = G4_As
  specific = 4
FEATURE [App::DocumentObjectGroupPython] Se_element001  label="Se_element : 1"  # scripted group (container) (typed FeaturePython)
  n = 1
  ref = Se_element
FEATURE [App::DocumentObjectGroupPython] G4_Se  # scripted group (container) (typed FeaturePython)
  Dunit = g/cm3
  Dvalue = 4.5
  Group = -> [Se_element001]
  conduct = 2
  density = 1
  expand = 3
  formula = Se
  name = G4_Se
  specific = 4
FEATURE [App::DocumentObjectGroupPython] Br_element007  label="Br_element : 004"  # scripted group (container) (typed FeaturePython)
  n = 1
  ref = Br_element
FEATURE [App::DocumentObjectGroupPython] G4_Br  # scripted group (container) (typed FeaturePython)
  Dunit = g/cm3
  Dvalue = 0.0070721
  Group = -> [Br_element007]
  conduct = 2
  density = 1
  expand = 3
  formula = Br
  name = G4_Br
  specific = 4
FEATURE [App::DocumentObjectGroupPython] Kr_element001  label="Kr_element : 1"  # scripted group (container) (typed FeaturePython)
  n = 1
  ref = Kr_element
FEATURE [App::DocumentObjectGroupPython] G4_Kr  # scripted group (container) (typed FeaturePython)
  Dunit = g/cm3
  Dvalue = 0.00347832
  Group = -> [Kr_element001]
  conduct = 2
  density = 1
  expand = 3
  formula = Kr
  name = G4_Kr
  specific = 4
FEATURE [App::DocumentObjectGroupPython] Rb_element001  label="Rb_element : 1"  # scripted group (container) (typed FeaturePython)
  n = 1
  ref = Rb_element
FEATURE [App::DocumentObjectGroupPython] G4_Rb  # scripted group (container) (typed FeaturePython)
  Dunit = g/cm3
  Dvalue = 1.532
  Group = -> [Rb_element001]
  conduct = 2
  density = 1
  expand = 3
  formula = Rb
  name = G4_Rb
  specific = 4
FEATURE [App::DocumentObjectGroupPython] Sr_element001  label="Sr_element : 1"  # scripted group (container) (typed FeaturePython)
  n = 1
  ref = Sr_element
FEATURE [App::DocumentObjectGroupPython] G4_Sr  # scripted group (container) (typed FeaturePython)
  Dunit = g/cm3
  Dvalue = 2.54
  Group = -> [Sr_element001]
  conduct = 2
  density = 1
  expand = 3
  formula = Sr
  name = G4_Sr
  specific = 4
FEATURE [App::DocumentObjectGroupPython] Y_element001  label="Y_element : 1"  # scripted group (container) (typed FeaturePython)
  n = 1
  ref = Y_element
FEATURE [App::DocumentObjectGroupPython] G4_Y  # scripted group (container) (typed FeaturePython)
  Dunit = g/cm3
  Dvalue = 4.469
  Group = -> [Y_element001]
  conduct = 2
  density = 1
  expand = 3
  formula = Y
  name = G4_Y
  specific = 4
FEATURE [App::DocumentObjectGroupPython] Zr_element001  label="Zr_element : 1"  # scripted group (container) (typed FeaturePython)
  n = 1
  ref = Zr_element
FEATURE [App::DocumentObjectGroupPython] G4_Zr  # scripted group (container) (typed FeaturePython)
  Dunit = g/cm3
  Dvalue = 6.506
  Group = -> [Zr_element001]
  conduct = 2
  density = 1
  expand = 3
  formula = Zr
  name = G4_Zr
  specific = 4
FEATURE [App::DocumentObjectGroupPython] Nb_element001  label="Nb_element : 1"  # scripted group (container) (typed FeaturePython)
  n = 1
  ref = Nb_element
FEATURE [App::DocumentObjectGroupPython] G4_Nb  # scripted group (container) (typed FeaturePython)
  Dunit = g/cm3
  Dvalue = 8.57
  Group = -> [Nb_element001]
  conduct = 2
  density = 1
  expand = 3
  formula = Nb
  name = G4_Nb
  specific = 4
FEATURE [App::DocumentObjectGroupPython] Mo_element001  label="Mo_element : 1"  # scripted group (container) (typed FeaturePython)
  n = 1
  ref = Mo_element
FEATURE [App::DocumentObjectGroupPython] G4_Mo  # scripted group (container) (typed FeaturePython)
  Dunit = g/cm3
  Dvalue = 10.22
  Group = -> [Mo_element001]
  conduct = 2
  density = 1
  expand = 3
  formula = Mo
  name = G4_Mo
  specific = 4
FEATURE [App::DocumentObjectGroupPython] Tc_element001  label="Tc_element : 1"  # scripted group (container) (typed FeaturePython)
  n = 1
  ref = Tc_element
FEATURE [App::DocumentObjectGroupPython] G4_Tc  # scripted group (container) (typed FeaturePython)
  Dunit = g/cm3
  Dvalue = 11.5
  Group = -> [Tc_element001]
  conduct = 2
  density = 1
  expand = 3
  formula = Tc
  name = G4_Tc
  specific = 4
FEATURE [App::DocumentObjectGroupPython] Ru_element001  label="Ru_element : 1"  # scripted group (container) (typed FeaturePython)
  n = 1
  ref = Ru_element
FEATURE [App::DocumentObjectGroupPython] G4_Ru  # scripted group (container) (typed FeaturePython)
  Dunit = g/cm3
  Dvalue = 12.41
  Group = -> [Ru_element001]
  conduct = 2
  density = 1
  expand = 3
  formula = Ru
  name = G4_Ru
  specific = 4
FEATURE [App::DocumentObjectGroupPython] Rh_element001  label="Rh_element : 1"  # scripted group (container) (typed FeaturePython)
  n = 1
  ref = Rh_element
FEATURE [App::DocumentObjectGroupPython] G4_Rh  # scripted group (container) (typed FeaturePython)
  Dunit = g/cm3
  Dvalue = 12.41
  Group = -> [Rh_element001]
  conduct = 2
  density = 1
  expand = 3
  formula = Rh
  name = G4_Rh
  specific = 4
FEATURE [App::DocumentObjectGroupPython] Pd_element001  label="Pd_element : 1"  # scripted group (container) (typed FeaturePython)
  n = 1
  ref = Pd_element
FEATURE [App::DocumentObjectGroupPython] G4_Pd  # scripted group (container) (typed FeaturePython)
  Dunit = g/cm3
  Dvalue = 12.02
  Group = -> [Pd_element001]
  conduct = 2
  density = 1
  expand = 3
  formula = Pd
  name = G4_Pd
  specific = 4
FEATURE [App::DocumentObjectGroupPython] Ag_element006  label="Ag_element : 004"  # scripted group (container) (typed FeaturePython)
  n = 1
  ref = Ag_element
FEATURE [App::DocumentObjectGroupPython] G4_Ag  # scripted group (container) (typed FeaturePython)
  Dunit = g/cm3
  Dvalue = 10.5
  Group = -> [Ag_element006]
  conduct = 2
  density = 1
  expand = 3
  formula = Ag
  name = G4_Ag
  specific = 4
FEATURE [App::DocumentObjectGroupPython] Cd_element003  label="Cd_element : 003"  # scripted group (container) (typed FeaturePython)
  n = 1
  ref = Cd_element
FEATURE [App::DocumentObjectGroupPython] G4_Cd  # scripted group (container) (typed FeaturePython)
  Dunit = g/cm3
  Dvalue = 8.65
  Group = -> [Cd_element003]
  conduct = 2
  density = 1
  expand = 3
  formula = Cd
  name = G4_Cd
  specific = 4
FEATURE [App::DocumentObjectGroupPython] In_element001  label="In_element : 1"  # scripted group (container) (typed FeaturePython)
  n = 1
  ref = In_element
FEATURE [App::DocumentObjectGroupPython] G4_In  # scripted group (container) (typed FeaturePython)
  Dunit = g/cm3
  Dvalue = 7.31
  Group = -> [In_element001]
  conduct = 2
  density = 1
  expand = 3
  formula = In
  name = G4_In
  specific = 4
FEATURE [App::DocumentObjectGroupPython] Sn_element001  label="Sn_element : 1"  # scripted group (container) (typed FeaturePython)
  n = 1
  ref = Sn_element
FEATURE [App::DocumentObjectGroupPython] G4_Sn  # scripted group (container) (typed FeaturePython)
  Dunit = g/cm3
  Dvalue = 7.31
  Group = -> [Sn_element001]
  conduct = 2
  density = 1
  expand = 3
  formula = Sn
  name = G4_Sn
  specific = 4
FEATURE [App::DocumentObjectGroupPython] Sb_element001  label="Sb_element : 1"  # scripted group (container) (typed FeaturePython)
  n = 1
  ref = Sb_element
FEATURE [App::DocumentObjectGroupPython] G4_Sb  # scripted group (container) (typed FeaturePython)
  Dunit = g/cm3
  Dvalue = 6.691
  Group = -> [Sb_element001]
  conduct = 2
  density = 1
  expand = 3
  formula = Sb
  name = G4_Sb
  specific = 4
FEATURE [App::DocumentObjectGroupPython] Te_element002  label="Te_element : 002"  # scripted group (container) (typed FeaturePython)
  n = 1
  ref = Te_element
FEATURE [App::DocumentObjectGroupPython] G4_Te  # scripted group (container) (typed FeaturePython)
  Dunit = g/cm3
  Dvalue = 6.24
  Group = -> [Te_element002]
  conduct = 2
  density = 1
  expand = 3
  formula = Te
  name = G4_Te
  specific = 4
FEATURE [App::DocumentObjectGroupPython] I_element010  label="I_element : 006"  # scripted group (container) (typed FeaturePython)
  n = 1
  ref = I_element
FEATURE [App::DocumentObjectGroupPython] G4_I  # scripted group (container) (typed FeaturePython)
  Dunit = g/cm3
  Dvalue = 4.93
  Group = -> [I_element010]
  conduct = 2
  density = 1
  expand = 3
  formula = I
  name = G4_I
  specific = 4
FEATURE [App::DocumentObjectGroupPython] Xe_element001  label="Xe_element : 1"  # scripted group (container) (typed FeaturePython)
  n = 1
  ref = Xe_element
FEATURE [App::DocumentObjectGroupPython] G4_Xe  # scripted group (container) (typed FeaturePython)
  Dunit = g/cm3
  Dvalue = 0.00548536
  Group = -> [Xe_element001]
  conduct = 2
  density = 1
  expand = 3
  formula = Xe
  name = G4_Xe
  specific = 4
FEATURE [App::DocumentObjectGroupPython] Cs_element003  label="Cs_element : 003"  # scripted group (container) (typed FeaturePython)
  n = 1
  ref = Cs_element
FEATURE [App::DocumentObjectGroupPython] G4_Cs  # scripted group (container) (typed FeaturePython)
  Dunit = g/cm3
  Dvalue = 1.873
  Group = -> [Cs_element003]
  conduct = 2
  density = 1
  expand = 3
  formula = Cs
  name = G4_Cs
  specific = 4
FEATURE [App::DocumentObjectGroupPython] Ba_element003  label="Ba_element : 003"  # scripted group (container) (typed FeaturePython)
  n = 1
  ref = Ba_element
FEATURE [App::DocumentObjectGroupPython] G4_Ba  # scripted group (container) (typed FeaturePython)
  Dunit = g/cm3
  Dvalue = 3.5
  Group = -> [Ba_element003]
  conduct = 2
  density = 1
  expand = 3
  formula = Ba
  name = G4_Ba
  specific = 4
FEATURE [App::DocumentObjectGroupPython] La_element003  label="La_element : 003"  # scripted group (container) (typed FeaturePython)
  n = 1
  ref = La_element
FEATURE [App::DocumentObjectGroupPython] G4_La  # scripted group (container) (typed FeaturePython)
  Dunit = g/cm3
  Dvalue = 6.154
  Group = -> [La_element003]
  conduct = 2
  density = 1
  expand = 3
  formula = La
  name = G4_La
  specific = 4
FEATURE [App::DocumentObjectGroupPython] Ce_element002  label="Ce_element : 1"  # scripted group (container) (typed FeaturePython)
  n = 1
  ref = Ce_element
FEATURE [App::DocumentObjectGroupPython] G4_Ce  # scripted group (container) (typed FeaturePython)
  Dunit = g/cm3
  Dvalue = 6.657
  Group = -> [Ce_element002]
  conduct = 2
  density = 1
  expand = 3
  formula = Ce
  name = G4_Ce
  specific = 4
FEATURE [App::DocumentObjectGroupPython] Pr_element001  label="Pr_element : 1"  # scripted group (container) (typed FeaturePython)
  n = 1
  ref = Pr_element
FEATURE [App::DocumentObjectGroupPython] G4_Pr  # scripted group (container) (typed FeaturePython)
  Dunit = g/cm3
  Dvalue = 6.71
  Group = -> [Pr_element001]
  conduct = 2
  density = 1
  expand = 3
  formula = Pr
  name = G4_Pr
  specific = 4
FEATURE [App::DocumentObjectGroupPython] Nd_element001  label="Nd_element : 1"  # scripted group (container) (typed FeaturePython)
  n = 1
  ref = Nd_element
FEATURE [App::DocumentObjectGroupPython] G4_Nd  # scripted group (container) (typed FeaturePython)
  Dunit = g/cm3
  Dvalue = 6.9
  Group = -> [Nd_element001]
  conduct = 2
  density = 1
  expand = 3
  formula = Nd
  name = G4_Nd
  specific = 4
FEATURE [App::DocumentObjectGroupPython] Pm_element001  label="Pm_element : 1"  # scripted group (container) (typed FeaturePython)
  n = 1
  ref = Pm_element
FEATURE [App::DocumentObjectGroupPython] G4_Pm  # scripted group (container) (typed FeaturePython)
  Dunit = g/cm3
  Dvalue = 7.22
  Group = -> [Pm_element001]
  conduct = 2
  density = 1
  expand = 3
  formula = Pm
  name = G4_Pm
  specific = 4
FEATURE [App::DocumentObjectGroupPython] Sm_element001  label="Sm_element : 1"  # scripted group (container) (typed FeaturePython)
  n = 1
  ref = Sm_element
FEATURE [App::DocumentObjectGroupPython] G4_Sm  # scripted group (container) (typed FeaturePython)
  Dunit = g/cm3
  Dvalue = 7.46
  Group = -> [Sm_element001]
  conduct = 2
  density = 1
  expand = 3
  formula = Sm
  name = G4_Sm
  specific = 4
FEATURE [App::DocumentObjectGroupPython] Eu_element001  label="Eu_element : 1"  # scripted group (container) (typed FeaturePython)
  n = 1
  ref = Eu_element
FEATURE [App::DocumentObjectGroupPython] G4_Eu  # scripted group (container) (typed FeaturePython)
  Dunit = g/cm3
  Dvalue = 5.243
  Group = -> [Eu_element001]
  conduct = 2
  density = 1
  expand = 3
  formula = Eu
  name = G4_Eu
  specific = 4
FEATURE [App::DocumentObjectGroupPython] Gd_element002  label="Gd_element : 1"  # scripted group (container) (typed FeaturePython)
  n = 1
  ref = Gd_element
FEATURE [App::DocumentObjectGroupPython] G4_Gd  # scripted group (container) (typed FeaturePython)
  Dunit = g/cm3
  Dvalue = 7.9004
  Group = -> [Gd_element002]
  conduct = 2
  density = 1
  expand = 3
  formula = Gd
  name = G4_Gd
  specific = 4
FEATURE [App::DocumentObjectGroupPython] Tb_element001  label="Tb_element : 1"  # scripted group (container) (typed FeaturePython)
  n = 1
  ref = Tb_element
FEATURE [App::DocumentObjectGroupPython] G4_Tb  # scripted group (container) (typed FeaturePython)
  Dunit = g/cm3
  Dvalue = 8.229
  Group = -> [Tb_element001]
  conduct = 2
  density = 1
  expand = 3
  formula = Tb
  name = G4_Tb
  specific = 4
FEATURE [App::DocumentObjectGroupPython] Dy_element001  label="Dy_element : 1"  # scripted group (container) (typed FeaturePython)
  n = 1
  ref = Dy_element
FEATURE [App::DocumentObjectGroupPython] G4_Dy  # scripted group (container) (typed FeaturePython)
  Dunit = g/cm3
  Dvalue = 8.55
  Group = -> [Dy_element001]
  conduct = 2
  density = 1
  expand = 3
  formula = Dy
  name = G4_Dy
  specific = 4
FEATURE [App::DocumentObjectGroupPython] Ho_element001  label="Ho_element : 1"  # scripted group (container) (typed FeaturePython)
  n = 1
  ref = Ho_element
FEATURE [App::DocumentObjectGroupPython] G4_Ho  # scripted group (container) (typed FeaturePython)
  Dunit = g/cm3
  Dvalue = 8.795
  Group = -> [Ho_element001]
  conduct = 2
  density = 1
  expand = 3
  formula = Ho
  name = G4_Ho
  specific = 4
FEATURE [App::DocumentObjectGroupPython] Er_element001  label="Er_element : 1"  # scripted group (container) (typed FeaturePython)
  n = 1
  ref = Er_element
FEATURE [App::DocumentObjectGroupPython] G4_Er  # scripted group (container) (typed FeaturePython)
  Dunit = g/cm3
  Dvalue = 9.066
  Group = -> [Er_element001]
  conduct = 2
  density = 1
  expand = 3
  formula = Er
  name = G4_Er
  specific = 4
FEATURE [App::DocumentObjectGroupPython] Tm_element001  label="Tm_element : 1"  # scripted group (container) (typed FeaturePython)
  n = 1
  ref = Tm_element
FEATURE [App::DocumentObjectGroupPython] G4_Tm  # scripted group (container) (typed FeaturePython)
  Dunit = g/cm3
  Dvalue = 9.321
  Group = -> [Tm_element001]
  conduct = 2
  density = 1
  expand = 3
  formula = Tm
  name = G4_Tm
  specific = 4
FEATURE [App::DocumentObjectGroupPython] Yb_element001  label="Yb_element : 1"  # scripted group (container) (typed FeaturePython)
  n = 1
  ref = Yb_element
FEATURE [App::DocumentObjectGroupPython] G4_Yb  # scripted group (container) (typed FeaturePython)
  Dunit = g/cm3
  Dvalue = 6.73
  Group = -> [Yb_element001]
  conduct = 2
  density = 1
  expand = 3
  formula = Yb
  name = G4_Yb
  specific = 4
FEATURE [App::DocumentObjectGroupPython] Lu_element001  label="Lu_element : 1"  # scripted group (container) (typed FeaturePython)
  n = 1
  ref = Lu_element
FEATURE [App::DocumentObjectGroupPython] G4_Lu  # scripted group (container) (typed FeaturePython)
  Dunit = g/cm3
  Dvalue = 9.84
  Group = -> [Lu_element001]
  conduct = 2
  density = 1
  expand = 3
  formula = Lu
  name = G4_Lu
  specific = 4
FEATURE [App::DocumentObjectGroupPython] Hf_element001  label="Hf_element : 1"  # scripted group (container) (typed FeaturePython)
  n = 1
  ref = Hf_element
FEATURE [App::DocumentObjectGroupPython] G4_Hf  # scripted group (container) (typed FeaturePython)
  Dunit = g/cm3
  Dvalue = 13.31
  Group = -> [Hf_element001]
  conduct = 2
  density = 1
  expand = 3
  formula = Hf
  name = G4_Hf
  specific = 4
FEATURE [App::DocumentObjectGroupPython] Ta_element001  label="Ta_element : 1"  # scripted group (container) (typed FeaturePython)
  n = 1
  ref = Ta_element
FEATURE [App::DocumentObjectGroupPython] G4_Ta  # scripted group (container) (typed FeaturePython)
  Dunit = g/cm3
  Dvalue = 16.654
  Group = -> [Ta_element001]
  conduct = 2
  density = 1
  expand = 3
  formula = Ta
  name = G4_Ta
  specific = 4
FEATURE [App::DocumentObjectGroupPython] W_element004  label="W_element : 004"  # scripted group (container) (typed FeaturePython)
  n = 1
  ref = W_element
FEATURE [App::DocumentObjectGroupPython] G4_W  # scripted group (container) (typed FeaturePython)
  Dunit = g/cm3
  Dvalue = 19.3
  Group = -> [W_element004]
  conduct = 2
  density = 1
  expand = 3
  formula = W
  name = G4_W
  specific = 4
FEATURE [App::DocumentObjectGroupPython] Re_element001  label="Re_element : 1"  # scripted group (container) (typed FeaturePython)
  n = 1
  ref = Re_element
FEATURE [App::DocumentObjectGroupPython] G4_Re  # scripted group (container) (typed FeaturePython)
  Dunit = g/cm3
  Dvalue = 21.02
  Group = -> [Re_element001]
  conduct = 2
  density = 1
  expand = 3
  formula = Re
  name = G4_Re
  specific = 4
FEATURE [App::DocumentObjectGroupPython] Os_element001  label="Os_element : 1"  # scripted group (container) (typed FeaturePython)
  n = 1
  ref = Os_element
FEATURE [App::DocumentObjectGroupPython] G4_Os  # scripted group (container) (typed FeaturePython)
  Dunit = g/cm3
  Dvalue = 22.57
  Group = -> [Os_element001]
  conduct = 2
  density = 1
  expand = 3
  formula = Os
  name = G4_Os
  specific = 4
FEATURE [App::DocumentObjectGroupPython] Ir_element001  label="Ir_element : 1"  # scripted group (container) (typed FeaturePython)
  n = 1
  ref = Ir_element
FEATURE [App::DocumentObjectGroupPython] G4_Ir  # scripted group (container) (typed FeaturePython)
  Dunit = g/cm3
  Dvalue = 22.42
  Group = -> [Ir_element001]
  conduct = 2
  density = 1
  expand = 3
  formula = Ir
  name = G4_Ir
  specific = 4
FEATURE [App::DocumentObjectGroupPython] Pt_element001  label="Pt_element : 1"  # scripted group (container) (typed FeaturePython)
  n = 1
  ref = Pt_element
FEATURE [App::DocumentObjectGroupPython] G4_Pt  # scripted group (container) (typed FeaturePython)
  Dunit = g/cm3
  Dvalue = 21.45
  Group = -> [Pt_element001]
  conduct = 2
  density = 1
  expand = 3
  formula = Pt
  name = G4_Pt
  specific = 4
FEATURE [App::DocumentObjectGroupPython] Au_element001  label="Au_element : 1"  # scripted group (container) (typed FeaturePython)
  n = 1
  ref = Au_element
FEATURE [App::DocumentObjectGroupPython] G4_Au  # scripted group (container) (typed FeaturePython)
  Dunit = g/cm3
  Dvalue = 19.32
  Group = -> [Au_element001]
  conduct = 2
  density = 1
  expand = 3
  formula = Au
  name = G4_Au
  specific = 4
FEATURE [App::DocumentObjectGroupPython] Hg_element002  label="Hg_element : 002"  # scripted group (container) (typed FeaturePython)
  n = 1
  ref = Hg_element
FEATURE [App::DocumentObjectGroupPython] G4_Hg  # scripted group (container) (typed FeaturePython)
  Dunit = g/cm3
  Dvalue = 13.546
  Group = -> [Hg_element002]
  conduct = 2
  density = 1
  expand = 3
  formula = Hg
  name = G4_Hg
  specific = 4
FEATURE [App::DocumentObjectGroupPython] Tl_element002  label="Tl_element : 002"  # scripted group (container) (typed FeaturePython)
  n = 1
  ref = Tl_element
FEATURE [App::DocumentObjectGroupPython] G4_Tl  # scripted group (container) (typed FeaturePython)
  Dunit = g/cm3
  Dvalue = 11.72
  Group = -> [Tl_element002]
  conduct = 2
  density = 1
  expand = 3
  formula = Tl
  name = G4_Tl
  specific = 4
FEATURE [App::DocumentObjectGroupPython] Pb_element003  label="Pb_element : 1"  # scripted group (container) (typed FeaturePython)
  n = 1
  ref = Pb_element
FEATURE [App::DocumentObjectGroupPython] G4_Pb  # scripted group (container) (typed FeaturePython)
  Dunit = g/cm3
  Dvalue = 11.35
  Group = -> [Pb_element003]
  conduct = 2
  density = 1
  expand = 3
  formula = Pb
  name = G4_Pb
  specific = 4
FEATURE [App::DocumentObjectGroupPython] Bi_element002  label="Bi_element : 1"  # scripted group (container) (typed FeaturePython)
  n = 1
  ref = Bi_element
FEATURE [App::DocumentObjectGroupPython] G4_Bi  # scripted group (container) (typed FeaturePython)
  Dunit = g/cm3
  Dvalue = 9.747
  Group = -> [Bi_element002]
  conduct = 2
  density = 1
  expand = 3
  formula = Bi
  name = G4_Bi
  specific = 4
FEATURE [App::DocumentObjectGroupPython] Po_element001  label="Po_element : 1"  # scripted group (container) (typed FeaturePython)
  n = 1
  ref = Po_element
FEATURE [App::DocumentObjectGroupPython] G4_Po  # scripted group (container) (typed FeaturePython)
  Dunit = g/cm3
  Dvalue = 9.32
  Group = -> [Po_element001]
  conduct = 2
  density = 1
  expand = 3
  formula = Po
  name = G4_Po
  specific = 4
FEATURE [App::DocumentObjectGroupPython] At_element001  label="At_element : 1"  # scripted group (container) (typed FeaturePython)
  n = 1
  ref = At_element
FEATURE [App::DocumentObjectGroupPython] G4_At  # scripted group (container) (typed FeaturePython)
  Dunit = g/cm3
  Dvalue = 9.32
  Group = -> [At_element001]
  conduct = 2
  density = 1
  expand = 3
  formula = At
  name = G4_At
  specific = 4
FEATURE [App::DocumentObjectGroupPython] Rn_element001  label="Rn_element : 1"  # scripted group (container) (typed FeaturePython)
  n = 1
  ref = Rn_element
FEATURE [App::DocumentObjectGroupPython] G4_Rn  # scripted group (container) (typed FeaturePython)
  Dunit = g/cm3
  Dvalue = 0.00900662
  Group = -> [Rn_element001]
  conduct = 2
  density = 1
  expand = 3
  formula = Rn
  name = G4_Rn
  specific = 4
FEATURE [App::DocumentObjectGroupPython] Fr_element001  label="Fr_element : 1"  # scripted group (container) (typed FeaturePython)
  n = 1
  ref = Fr_element
FEATURE [App::DocumentObjectGroupPython] G4_Fr  # scripted group (container) (typed FeaturePython)
  Dunit = g/cm3
  Dvalue = 1
  Group = -> [Fr_element001]
  conduct = 2
  density = 1
  expand = 3
  formula = Fr
  name = G4_Fr
  specific = 4
FEATURE [App::DocumentObjectGroupPython] Ra_element001  label="Ra_element : 1"  # scripted group (container) (typed FeaturePython)
  n = 1
  ref = Ra_element
FEATURE [App::DocumentObjectGroupPython] G4_Ra  # scripted group (container) (typed FeaturePython)
  Dunit = g/cm3
  Dvalue = 5
  Group = -> [Ra_element001]
  conduct = 2
  density = 1
  expand = 3
  formula = Ra
  name = G4_Ra
  specific = 4
FEATURE [App::DocumentObjectGroupPython] Ac_element001  label="Ac_element : 1"  # scripted group (container) (typed FeaturePython)
  n = 1
  ref = Ac_element
FEATURE [App::DocumentObjectGroupPython] G4_Ac  # scripted group (container) (typed FeaturePython)
  Dunit = g/cm3
  Dvalue = 10.07
  Group = -> [Ac_element001]
  conduct = 2
  density = 1
  expand = 3
  formula = Ac
  name = G4_Ac
  specific = 4
FEATURE [App::DocumentObjectGroupPython] Th_element001  label="Th_element : 1"  # scripted group (container) (typed FeaturePython)
  n = 1
  ref = Th_element
FEATURE [App::DocumentObjectGroupPython] G4_Th  # scripted group (container) (typed FeaturePython)
  Dunit = g/cm3
  Dvalue = 11.72
  Group = -> [Th_element001]
  conduct = 2
  density = 1
  expand = 3
  formula = Th
  name = G4_Th
  specific = 4
FEATURE [App::DocumentObjectGroupPython] Pa_element001  label="Pa_element : 1"  # scripted group (container) (typed FeaturePython)
  n = 1
  ref = Pa_element
FEATURE [App::DocumentObjectGroupPython] G4_Pa  # scripted group (container) (typed FeaturePython)
  Dunit = g/cm3
  Dvalue = 15.37
  Group = -> [Pa_element001]
  conduct = 2
  density = 1
  expand = 3
  formula = Pa
  name = G4_Pa
  specific = 4
FEATURE [App::DocumentObjectGroupPython] U_element004  label="U_element : 004"  # scripted group (container) (typed FeaturePython)
  n = 1
  ref = U_element
FEATURE [App::DocumentObjectGroupPython] G4_U  # scripted group (container) (typed FeaturePython)
  Dunit = g/cm3
  Dvalue = 18.95
  Group = -> [U_element004]
  conduct = 2
  density = 1
  expand = 3
  formula = U
  name = G4_U
  specific = 4
FEATURE [App::DocumentObjectGroupPython] Np_element001  label="Np_element : 1"  # scripted group (container) (typed FeaturePython)
  n = 1
  ref = Np_element
FEATURE [App::DocumentObjectGroupPython] G4_Np  # scripted group (container) (typed FeaturePython)
  Dunit = g/cm3
  Dvalue = 20.25
  Group = -> [Np_element001]
  conduct = 2
  density = 1
  expand = 3
  formula = Np
  name = G4_Np
  specific = 4
FEATURE [App::DocumentObjectGroupPython] Pu_element002  label="Pu_element : 002"  # scripted group (container) (typed FeaturePython)
  n = 1
  ref = Pu_element
FEATURE [App::DocumentObjectGroupPython] G4_Pu  # scripted group (container) (typed FeaturePython)
  Dunit = g/cm3
  Dvalue = 19.84
  Group = -> [Pu_element002]
  conduct = 2
  density = 1
  expand = 3
  formula = Pu
  name = G4_Pu
  specific = 4
FEATURE [App::DocumentObjectGroupPython] Am_element001  label="Am_element : 1"  # scripted group (container) (typed FeaturePython)
  n = 1
  ref = Am_element
FEATURE [App::DocumentObjectGroupPython] G4_Am  # scripted group (container) (typed FeaturePython)
  Dunit = g/cm3
  Dvalue = 13.67
  Group = -> [Am_element001]
  conduct = 2
  density = 1
  expand = 3
  formula = Am
  name = G4_Am
  specific = 4
FEATURE [App::DocumentObjectGroupPython] Cm_element001  label="Cm_element : 1"  # scripted group (container) (typed FeaturePython)
  n = 1
  ref = Cm_element
FEATURE [App::DocumentObjectGroupPython] G4_Cm  # scripted group (container) (typed FeaturePython)
  Dunit = g/cm3
  Dvalue = 13.51
  Group = -> [Cm_element001]
  conduct = 2
  density = 1
  expand = 3
  formula = Cm
  name = G4_Cm
  specific = 4
FEATURE [App::DocumentObjectGroupPython] Bk_element001  label="Bk_element : 1"  # scripted group (container) (typed FeaturePython)
  n = 1
  ref = Bk_element
FEATURE [App::DocumentObjectGroupPython] G4_Bk  # scripted group (container) (typed FeaturePython)
  Dunit = g/cm3
  Dvalue = 14
  Group = -> [Bk_element001]
  conduct = 2
  density = 1
  expand = 3
  formula = Bk
  name = G4_Bk
  specific = 4
FEATURE [App::DocumentObjectGroupPython] Cf_element001  label="Cf_element : 1"  # scripted group (container) (typed FeaturePython)
  n = 1
  ref = Cf_element
FEATURE [App::DocumentObjectGroupPython] G4_Cf  # scripted group (container) (typed FeaturePython)
  Dunit = g/cm3
  Dvalue = 10
  Group = -> [Cf_element001]
  conduct = 2
  density = 1
  expand = 3
  formula = Cf
  name = G4_Cf
  specific = 4
FEATURE [App::DocumentObjectGroupPython] Element  # scripted group (container) (typed FeaturePython)
  Group = -> [G4_H,G4_He,G4_Li,G4_Be,G4_B,G4_C,G4_N,G4_O,G4_F,G4_Ne,G4_Na,G4_Mg,G4_Al,G4_Si,G4_P,G4_S,G4_Cl,G4_Ar,G4_K,G4_Ca,G4_Sc,G4_Ti,G4_V,G4_Cr,G4_Mn,G4_Fe,G4_Co,G4_Ni,G4_Cu,G4_Zn,G4_Ga,G4_Ge,G4_As,G4_Se,G4_Br,G4_Kr,G4_Rb,G4_Sr,G4_Y,G4_Zr,G4_Nb,G4_Mo,G4_Tc,G4_Ru,G4_Rh,G4_Pd,G4_Ag,G4_Cd,G4_In,G4_Sn,G4_Sb,G4_Te,G4_I,G4_Xe,G4_Cs,G4_Ba,G4_La,G4_Ce,G4_Pr,G4_Nd,G4_Pm,G4_Sm,G4_Eu,G4_Gd,G4_Tb,G4_Dy,G4_Ho,G4_Er,+30 more]
FEATURE [App::DocumentObjectGroupPython] H_element114  label="H_element : 063"  # scripted group (container) (typed FeaturePython)
  n = 2
  ref = H_element
FEATURE [App::DocumentObjectGroupPython] G4_lH2  # scripted group (container) (typed FeaturePython)
  Dunit = g/cm3
  Dvalue = 0.0708
  Group = -> [H_element114]
  conduct = 2
  density = 1
  expand = 3
  formula = G4_lH2
  name = G4_lH2
  specific = 4
FEATURE [App::DocumentObjectGroupPython] N_element049  label="N_element : 022"  # scripted group (container) (typed FeaturePython)
  n = 2
  ref = N_element
FEATURE [App::DocumentObjectGroupPython] G4_lN2  # scripted group (container) (typed FeaturePython)
  Dunit = g/cm3
  Dvalue = 0.807
  Group = -> [N_element049]
  conduct = 2
  density = 1
  expand = 3
  formula = G4_lN2
  name = G4_lN2
  specific = 4
FEATURE [App::DocumentObjectGroupPython] O_element106  label="O_element : 060"  # scripted group (container) (typed FeaturePython)
  n = 2
  ref = O_element
FEATURE [App::DocumentObjectGroupPython] G4_lO2  # scripted group (container) (typed FeaturePython)
  Dunit = g/cm3
  Dvalue = 1.141
  Group = -> [O_element106]
  conduct = 2
  density = 1
  expand = 3
  formula = G4_lO2
  name = G4_lO2
  specific = 4
FEATURE [App::DocumentObjectGroupPython] Ar_element003  label="Ar_element : 002"  # scripted group (container) (typed FeaturePython)
  n = 1
  ref = Ar_element
FEATURE [App::DocumentObjectGroupPython] G4_lAr  # scripted group (container) (typed FeaturePython)
  Dunit = g/cm3
  Dvalue = 1.396
  Group = -> [Ar_element003]
  conduct = 2
  density = 1
  expand = 3
  formula = G4_lAr
  name = G4_lAr
  specific = 4
FEATURE [App::DocumentObjectGroupPython] Br_element008  label="Br_element : 005"  # scripted group (container) (typed FeaturePython)
  n = 1
  ref = Br_element
FEATURE [App::DocumentObjectGroupPython] G4_lBr  # scripted group (container) (typed FeaturePython)
  Dunit = g/cm3
  Dvalue = 3.1028
  Group = -> [Br_element008]
  conduct = 2
  density = 1
  expand = 3
  formula = G4_lBr
  name = G4_lBr
  specific = 4
FEATURE [App::DocumentObjectGroupPython] Kr_element002  label="Kr_element : 002"  # scripted group (container) (typed FeaturePython)
  n = 1
  ref = Kr_element
FEATURE [App::DocumentObjectGroupPython] G4_lKr  # scripted group (container) (typed FeaturePython)
  Dunit = g/cm3
  Dvalue = 2.418
  Group = -> [Kr_element002]
  conduct = 2
  density = 1
  expand = 3
  formula = G4_lKr
  name = G4_lKr
  specific = 4
FEATURE [App::DocumentObjectGroupPython] Xe_element002  label="Xe_element : 002"  # scripted group (container) (typed FeaturePython)
  n = 1
  ref = Xe_element
FEATURE [App::DocumentObjectGroupPython] G4_lXe  # scripted group (container) (typed FeaturePython)
  Dunit = g/cm3
  Dvalue = 2.953
  Group = -> [Xe_element002]
  conduct = 2
  density = 1
  expand = 3
  formula = G4_lXe
  name = G4_lXe
  specific = 4
FEATURE [App::DocumentObjectGroupPython] O_element107  label="O_element : 061"  # scripted group (container) (typed FeaturePython)
  n = 4
  ref = O_element
FEATURE [App::DocumentObjectGroupPython] Pb_element004  label="Pb_element : 002"  # scripted group (container) (typed FeaturePython)
  n = 1
  ref = Pb_element
FEATURE [App::DocumentObjectGroupPython] W_element005  label="W_element : 005"  # scripted group (container) (typed FeaturePython)
  n = 1
  ref = W_element
FEATURE [App::DocumentObjectGroupPython] G4_PbWO4  # scripted group (container) (typed FeaturePython)
  Dunit = g/cm3
  Dvalue = 8.28
  Group = -> [O_element107,Pb_element004,W_element005]
  conduct = 2
  density = 1
  expand = 3
  formula = G4_PbWO4
  name = G4_PbWO4
  specific = 4
FEATURE [App::DocumentObjectGroupPython] H_element115  label="H_element : 064"  # scripted group (container) (typed FeaturePython)
  n = 1
  ref = H_element
FEATURE [App::DocumentObjectGroupPython] G4_Galactic  # scripted group (container) (typed FeaturePython)
  Dunit = g/cm3
  Dvalue = 0
  Group = -> [H_element115]
  conduct = 2
  density = 1
  expand = 3
  formula = G4_Galactic
  name = G4_Galactic
  specific = 4
FEATURE [App::DocumentObjectGroupPython] C_element125  label="C_element : 071"  # scripted group (container) (typed FeaturePython)
  n = 1
  ref = C_element
FEATURE [App::DocumentObjectGroupPython] G4_GRAPHITE_POROUS  # scripted group (container) (typed FeaturePython)
  Dunit = g/cm3
  Dvalue = 1.7
  Group = -> [C_element125]
  conduct = 2
  density = 1
  expand = 3
  formula = G4_GRAPHITE_POROUS
  name = G4_GRAPHITE_POROUS
  specific = 4
FEATURE [App::DocumentObjectGroupPython] H_element116  label="H_element : 0.150"  # scripted group (container) (typed FeaturePython)
  n = 0.080538
FEATURE [App::DocumentObjectGroupPython] C_element126  label="C_element : 0.600"  # scripted group (container) (typed FeaturePython)
  n = 0.599848
FEATURE [App::DocumentObjectGroupPython] O_element108  label="O_element : 0.320"  # scripted group (container) (typed FeaturePython)
  n = 0.319614
FEATURE [App::DocumentObjectGroupPython] G4_LUCITE  # scripted group (container) (typed FeaturePython)
  Dunit = g/cm3
  Dvalue = 1.19
  Group = -> [H_element116,C_element126,O_element108]
  conduct = 2
  density = 1
  expand = 3
  formula = G4_LUCITE
  name = G4_LUCITE
  specific = 4
FEATURE [App::DocumentObjectGroupPython] Cu_element002  label="Cu_element : 62"  # scripted group (container) (typed FeaturePython)
  n = 62
  ref = Cu_element
FEATURE [App::DocumentObjectGroupPython] Zn_element002  label="Zn_element : 35"  # scripted group (container) (typed FeaturePython)
  n = 35
  ref = Zn_element
FEATURE [App::DocumentObjectGroupPython] Pb_element005  label="Pb_element : 3"  # scripted group (container) (typed FeaturePython)
  n = 3
  ref = Pb_element
FEATURE [App::DocumentObjectGroupPython] G4_BRASS  # scripted group (container) (typed FeaturePython)
  Dunit = g/cm3
  Dvalue = 8.52
  Group = -> [Cu_element002,Zn_element002,Pb_element005]
  conduct = 2
  density = 1
  expand = 3
  formula = G4_BRASS
  name = G4_BRASS
  specific = 4
FEATURE [App::DocumentObjectGroupPython] Cu_element003  label="Cu_element : 89"  # scripted group (container) (typed FeaturePython)
  n = 89
  ref = Cu_element
FEATURE [App::DocumentObjectGroupPython] Zn_element003  label="Zn_element : 9"  # scripted group (container) (typed FeaturePython)
  n = 9
  ref = Zn_element
FEATURE [App::DocumentObjectGroupPython] Pb_element006  label="Pb_element : 2"  # scripted group (container) (typed FeaturePython)
  n = 2
  ref = Pb_element
FEATURE [App::DocumentObjectGroupPython] G4_BRONZE  # scripted group (container) (typed FeaturePython)
  Dunit = g/cm3
  Dvalue = 8.82
  Group = -> [Cu_element003,Zn_element003,Pb_element006]
  conduct = 2
  density = 1
  expand = 3
  formula = G4_BRONZE
  name = G4_BRONZE
  specific = 4
FEATURE [App::DocumentObjectGroupPython] Fe_element008  label="Fe_element : 74"  # scripted group (container) (typed FeaturePython)
  n = 74
  ref = Fe_element
FEATURE [App::DocumentObjectGroupPython] Cr_element002  label="Cr_element : 18"  # scripted group (container) (typed FeaturePython)
  n = 18
  ref = Cr_element
FEATURE [App::DocumentObjectGroupPython] Ni_element002  label="Ni_element : 8"  # scripted group (container) (typed FeaturePython)
  n = 8
  ref = Ni_element
FEATURE [App::DocumentObjectGroupPython] G4_STAINLESS_STEEL  label="G4_STAINLESS-STEEL"  # scripted group (container) (typed FeaturePython)
  Dunit = g/cm3
  Dvalue = 8
  Group = -> [Fe_element008,Cr_element002,Ni_element002]
  conduct = 2
  density = 1
  expand = 3
  formula = G4_STAINLESS-STEEL
  name = G4_STAINLESS-STEEL
  specific = 4
FEATURE [App::DocumentObjectGroupPython] H_element117  label="H_element : 065"  # scripted group (container) (typed FeaturePython)
  n = 18
  ref = H_element
FEATURE [App::DocumentObjectGroupPython] C_element127  label="C_element : 072"  # scripted group (container) (typed FeaturePython)
  n = 12
  ref = C_element
FEATURE [App::DocumentObjectGroupPython] O_element109  label="O_element : 062"  # scripted group (container) (typed FeaturePython)
  n = 7
  ref = O_element
FEATURE [App::DocumentObjectGroupPython] G4_CR39  # scripted group (container) (typed FeaturePython)
  Dunit = g/cm3
  Dvalue = 1.32
  Group = -> [H_element117,C_element127,O_element109]
  conduct = 2
  density = 1
  expand = 3
  formula = G4_CR39
  name = G4_CR39
  specific = 4
FEATURE [App::DocumentObjectGroupPython] H_element118  label="H_element : 38"  # scripted group (container) (typed FeaturePython)
  n = 38
  ref = H_element
FEATURE [App::DocumentObjectGroupPython] C_element128  label="C_element : 073"  # scripted group (container) (typed FeaturePython)
  n = 18
  ref = C_element
FEATURE [App::DocumentObjectGroupPython] O_element110  label="O_element : 063"  # scripted group (container) (typed FeaturePython)
  n = 1
  ref = O_element
FEATURE [App::DocumentObjectGroupPython] G4_OCTADECANOL  # scripted group (container) (typed FeaturePython)
  Dunit = g/cm3
  Dvalue = 0.812
  Group = -> [H_element118,C_element128,O_element110]
  conduct = 2
  density = 1
  expand = 3
  formula = G4_OCTADECANOL
  name = G4_OCTADECANOL
  specific = 4
FEATURE [App::DocumentObjectGroupPython] HEP  # scripted group (container) (typed FeaturePython)
  Group = -> [G4_lH2,G4_lN2,G4_lO2,G4_lAr,G4_lBr,G4_lKr,G4_lXe,G4_PbWO4,G4_Galactic,G4_GRAPHITE_POROUS,G4_LUCITE,G4_BRASS,G4_BRONZE,G4_STAINLESS_STEEL,G4_CR39,G4_OCTADECANOL]
FEATURE [App::DocumentObjectGroupPython] C_element129  label="C_element : 074"  # scripted group (container) (typed FeaturePython)
  n = 14
  ref = C_element
FEATURE [App::DocumentObjectGroupPython] H_element119  label="H_element : 066"  # scripted group (container) (typed FeaturePython)
  n = 10
  ref = H_element
FEATURE [App::DocumentObjectGroupPython] O_element111  label="O_element : 064"  # scripted group (container) (typed FeaturePython)
  n = 2
  ref = O_element
FEATURE [App::DocumentObjectGroupPython] N_element050  label="N_element : 023"  # scripted group (container) (typed FeaturePython)
  n = 2
  ref = N_element
FEATURE [App::DocumentObjectGroupPython] G4_KEVLAR  # scripted group (container) (typed FeaturePython)
  Dunit = g/cm3
  Dvalue = 1.44
  Group = -> [C_element129,H_element119,O_element111,N_element050]
  conduct = 2
  density = 1
  expand = 3
  formula = G4_KEVLAR
  name = G4_KEVLAR
  specific = 4
FEATURE [App::DocumentObjectGroupPython] C_element130  label="C_element : 075"  # scripted group (container) (typed FeaturePython)
  n = 10
  ref = C_element
FEATURE [App::DocumentObjectGroupPython] H_element120  label="H_element : 067"  # scripted group (container) (typed FeaturePython)
  n = 8
  ref = H_element
FEATURE [App::DocumentObjectGroupPython] O_element112  label="O_element : 065"  # scripted group (container) (typed FeaturePython)
  n = 4
  ref = O_element
FEATURE [App::DocumentObjectGroupPython] G4_DACRON  # scripted group (container) (typed FeaturePython)
  Dunit = g/cm3
  Dvalue = 1.4
  Group = -> [C_element130,H_element120,O_element112]
  conduct = 2
  density = 1
  expand = 3
  formula = G4_DACRON
  name = G4_DACRON
  specific = 4
FEATURE [App::DocumentObjectGroupPython] C_element131  label="C_element : 076"  # scripted group (container) (typed FeaturePython)
  n = 4
  ref = C_element
FEATURE [App::DocumentObjectGroupPython] H_element121  label="H_element : 068"  # scripted group (container) (typed FeaturePython)
  n = 5
  ref = H_element
FEATURE [App::DocumentObjectGroupPython] Cl_element030  label="Cl_element : 016"  # scripted group (container) (typed FeaturePython)
  n = 1
  ref = Cl_element
FEATURE [App::DocumentObjectGroupPython] G4_NEOPRENE  # scripted group (container) (typed FeaturePython)
  Dunit = g/cm3
  Dvalue = 1.23
  Group = -> [C_element131,H_element121,Cl_element030]
  conduct = 2
  density = 1
  expand = 3
  formula = G4_NEOPRENE
  name = G4_NEOPRENE
  specific = 4
FEATURE [App::DocumentObjectGroupPython] Space  # scripted group (container) (typed FeaturePython)
  Group = -> [G4_KEVLAR,G4_DACRON,G4_NEOPRENE]
FEATURE [App::DocumentObjectGroupPython] H_element122  label="H_element : 069"  # scripted group (container) (typed FeaturePython)
  n = 5
  ref = H_element
FEATURE [App::DocumentObjectGroupPython] C_element132  label="C_element : 077"  # scripted group (container) (typed FeaturePython)
  n = 4
  ref = C_element
FEATURE [App::DocumentObjectGroupPython] N_element051  label="N_element : 3"  # scripted group (container) (typed FeaturePython)
  n = 3
  ref = N_element
FEATURE [App::DocumentObjectGroupPython] O_element113  label="O_element : 066"  # scripted group (container) (typed FeaturePython)
  n = 1
  ref = O_element
FEATURE [App::DocumentObjectGroupPython] G4_CYTOSINE  # scripted group (container) (typed FeaturePython)
  Dunit = g/cm3
  Dvalue = 1.55
  Group = -> [H_element122,C_element132,N_element051,O_element113]
  conduct = 2
  density = 1
  expand = 3
  formula = G4_CYTOSINE
  name = G4_CYTOSINE
  specific = 4
FEATURE [App::DocumentObjectGroupPython] H_element123  label="H_element : 070"  # scripted group (container) (typed FeaturePython)
  n = 6
  ref = H_element
FEATURE [App::DocumentObjectGroupPython] C_element133  label="C_element : 078"  # scripted group (container) (typed FeaturePython)
  n = 5
  ref = C_element
FEATURE [App::DocumentObjectGroupPython] N_element052  label="N_element : 024"  # scripted group (container) (typed FeaturePython)
  n = 2
  ref = N_element
FEATURE [App::DocumentObjectGroupPython] O_element114  label="O_element : 067"  # scripted group (container) (typed FeaturePython)
  n = 2
  ref = O_element
FEATURE [App::DocumentObjectGroupPython] G4_THYMINE  # scripted group (container) (typed FeaturePython)
  Dunit = g/cm3
  Dvalue = 1.23
  Group = -> [H_element123,C_element133,N_element052,O_element114]
  conduct = 2
  density = 1
  expand = 3
  formula = G4_THYMINE
  name = G4_THYMINE
  specific = 4
FEATURE [App::DocumentObjectGroupPython] H_element124  label="H_element : 071"  # scripted group (container) (typed FeaturePython)
  n = 4
  ref = H_element
FEATURE [App::DocumentObjectGroupPython] C_element134  label="C_element : 079"  # scripted group (container) (typed FeaturePython)
  n = 4
  ref = C_element
FEATURE [App::DocumentObjectGroupPython] N_element053  label="N_element : 025"  # scripted group (container) (typed FeaturePython)
  n = 2
  ref = N_element
FEATURE [App::DocumentObjectGroupPython] O_element115  label="O_element : 068"  # scripted group (container) (typed FeaturePython)
  n = 2
  ref = O_element
FEATURE [App::DocumentObjectGroupPython] G4_URACIL  # scripted group (container) (typed FeaturePython)
  Dunit = g/cm3
  Dvalue = 1.32
  Group = -> [H_element124,C_element134,N_element053,O_element115]
  conduct = 2
  density = 1
  expand = 3
  formula = G4_URACIL
  name = G4_URACIL
  specific = 4
FEATURE [App::DocumentObjectGroupPython] H_element125  label="H_element : 072"  # scripted group (container) (typed FeaturePython)
  n = 4
  ref = H_element
FEATURE [App::DocumentObjectGroupPython] C_element135  label="C_element : 080"  # scripted group (container) (typed FeaturePython)
  n = 5
  ref = C_element
FEATURE [App::DocumentObjectGroupPython] N_element054  label="N_element : 026"  # scripted group (container) (typed FeaturePython)
  n = 5
  ref = N_element
FEATURE [App::DocumentObjectGroupPython] G4_DNA_ADENINE  # scripted group (container) (typed FeaturePython)
  Dunit = g/cm3
  Dvalue = 1
  Group = -> [H_element125,C_element135,N_element054]
  conduct = 2
  density = 1
  expand = 3
  formula = G4_DNA_ADENINE
  name = G4_DNA_ADENINE
  specific = 4
FEATURE [App::DocumentObjectGroupPython] H_element126  label="H_element : 073"  # scripted group (container) (typed FeaturePython)
  n = 4
  ref = H_element
FEATURE [App::DocumentObjectGroupPython] C_element136  label="C_element : 081"  # scripted group (container) (typed FeaturePython)
  n = 5
  ref = C_element
FEATURE [App::DocumentObjectGroupPython] N_element055  label="N_element : 027"  # scripted group (container) (typed FeaturePython)
  n = 5
  ref = N_element
FEATURE [App::DocumentObjectGroupPython] O_element116  label="O_element : 069"  # scripted group (container) (typed FeaturePython)
  n = 1
  ref = O_element
FEATURE [App::DocumentObjectGroupPython] G4_DNA_GUANINE  # scripted group (container) (typed FeaturePython)
  Dunit = g/cm3
  Dvalue = 1
  Group = -> [H_element126,C_element136,N_element055,O_element116]
  conduct = 2
  density = 1
  expand = 3
  formula = G4_DNA_GUANINE
  name = G4_DNA_GUANINE
  specific = 4
FEATURE [App::DocumentObjectGroupPython] H_element127  label="H_element : 074"  # scripted group (container) (typed FeaturePython)
  n = 4
  ref = H_element
FEATURE [App::DocumentObjectGroupPython] C_element137  label="C_element : 082"  # scripted group (container) (typed FeaturePython)
  n = 4
  ref = C_element
FEATURE [App::DocumentObjectGroupPython] N_element056  label="N_element : 028"  # scripted group (container) (typed FeaturePython)
  n = 3
  ref = N_element
FEATURE [App::DocumentObjectGroupPython] O_element117  label="O_element : 070"  # scripted group (container) (typed FeaturePython)
  n = 1
  ref = O_element
FEATURE [App::DocumentObjectGroupPython] G4_DNA_CYTOSINE  # scripted group (container) (typed FeaturePython)
  Dunit = g/cm3
  Dvalue = 1
  Group = -> [H_element127,C_element137,N_element056,O_element117]
  conduct = 2
  density = 1
  expand = 3
  formula = G4_DNA_CYTOSINE
  name = G4_DNA_CYTOSINE
  specific = 4
FEATURE [App::DocumentObjectGroupPython] H_element128  label="H_element : 075"  # scripted group (container) (typed FeaturePython)
  n = 5
  ref = H_element
FEATURE [App::DocumentObjectGroupPython] C_element138  label="C_element : 083"  # scripted group (container) (typed FeaturePython)
  n = 5
  ref = C_element
FEATURE [App::DocumentObjectGroupPython] N_element057  label="N_element : 029"  # scripted group (container) (typed FeaturePython)
  n = 2
  ref = N_element
FEATURE [App::DocumentObjectGroupPython] O_element118  label="O_element : 071"  # scripted group (container) (typed FeaturePython)
  n = 2
  ref = O_element
FEATURE [App::DocumentObjectGroupPython] G4_DNA_THYMINE  # scripted group (container) (typed FeaturePython)
  Dunit = g/cm3
  Dvalue = 1
  Group = -> [H_element128,C_element138,N_element057,O_element118]
  conduct = 2
  density = 1
  expand = 3
  formula = G4_DNA_THYMINE
  name = G4_DNA_THYMINE
  specific = 4
FEATURE [App::DocumentObjectGroupPython] H_element129  label="H_element : 076"  # scripted group (container) (typed FeaturePython)
  n = 3
  ref = H_element
FEATURE [App::DocumentObjectGroupPython] C_element139  label="C_element : 084"  # scripted group (container) (typed FeaturePython)
  n = 4
  ref = C_element
FEATURE [App::DocumentObjectGroupPython] N_element058  label="N_element : 030"  # scripted group (container) (typed FeaturePython)
  n = 2
  ref = N_element
FEATURE [App::DocumentObjectGroupPython] O_element119  label="O_element : 072"  # scripted group (container) (typed FeaturePython)
  n = 2
  ref = O_element
FEATURE [App::DocumentObjectGroupPython] G4_DNA_URACIL  # scripted group (container) (typed FeaturePython)
  Dunit = g/cm3
  Dvalue = 1
  Group = -> [H_element129,C_element139,N_element058,O_element119]
  conduct = 2
  density = 1
  expand = 3
  formula = G4_DNA_URACIL
  name = G4_DNA_URACIL
  specific = 4
FEATURE [App::DocumentObjectGroupPython] H_element130  label="H_element : 077"  # scripted group (container) (typed FeaturePython)
  n = 10
  ref = H_element
FEATURE [App::DocumentObjectGroupPython] C_element140  label="C_element : 085"  # scripted group (container) (typed FeaturePython)
  n = 10
  ref = C_element
FEATURE [App::DocumentObjectGroupPython] N_element059  label="N_element : 031"  # scripted group (container) (typed FeaturePython)
  n = 5
  ref = N_element
FEATURE [App::DocumentObjectGroupPython] O_element120  label="O_element : 073"  # scripted group (container) (typed FeaturePython)
  n = 4
  ref = O_element
FEATURE [App::DocumentObjectGroupPython] G4_DNA_ADENOSINE  # scripted group (container) (typed FeaturePython)
  Dunit = g/cm3
  Dvalue = 1
  Group = -> [H_element130,C_element140,N_element059,O_element120]
  conduct = 2
  density = 1
  expand = 3
  formula = G4_DNA_ADENOSINE
  name = G4_DNA_ADENOSINE
  specific = 4
FEATURE [App::DocumentObjectGroupPython] H_element131  label="H_element : 078"  # scripted group (container) (typed FeaturePython)
  n = 10
  ref = H_element
FEATURE [App::DocumentObjectGroupPython] C_element141  label="C_element : 086"  # scripted group (container) (typed FeaturePython)
  n = 10
  ref = C_element
FEATURE [App::DocumentObjectGroupPython] N_element060  label="N_element : 032"  # scripted group (container) (typed FeaturePython)
  n = 5
  ref = N_element
FEATURE [App::DocumentObjectGroupPython] O_element121  label="O_element : 074"  # scripted group (container) (typed FeaturePython)
  n = 5
  ref = O_element
FEATURE [App::DocumentObjectGroupPython] G4_DNA_GUANOSINE  # scripted group (container) (typed FeaturePython)
  Dunit = g/cm3
  Dvalue = 1
  Group = -> [H_element131,C_element141,N_element060,O_element121]
  conduct = 2
  density = 1
  expand = 3
  formula = G4_DNA_GUANOSINE
  name = G4_DNA_GUANOSINE
  specific = 4
FEATURE [App::DocumentObjectGroupPython] H_element132  label="H_element : 079"  # scripted group (container) (typed FeaturePython)
  n = 10
  ref = H_element
FEATURE [App::DocumentObjectGroupPython] C_element142  label="C_element : 087"  # scripted group (container) (typed FeaturePython)
  n = 9
  ref = C_element
FEATURE [App::DocumentObjectGroupPython] N_element061  label="N_element : 033"  # scripted group (container) (typed FeaturePython)
  n = 3
  ref = N_element
FEATURE [App::DocumentObjectGroupPython] O_element122  label="O_element : 075"  # scripted group (container) (typed FeaturePython)
  n = 5
  ref = O_element
FEATURE [App::DocumentObjectGroupPython] G4_DNA_CYTIDINE  # scripted group (container) (typed FeaturePython)
  Dunit = g/cm3
  Dvalue = 1
  Group = -> [H_element132,C_element142,N_element061,O_element122]
  conduct = 2
  density = 1
  expand = 3
  formula = G4_DNA_CYTIDINE
  name = G4_DNA_CYTIDINE
  specific = 4
FEATURE [App::DocumentObjectGroupPython] H_element133  label="H_element : 080"  # scripted group (container) (typed FeaturePython)
  n = 9
  ref = H_element
FEATURE [App::DocumentObjectGroupPython] C_element143  label="C_element : 088"  # scripted group (container) (typed FeaturePython)
  n = 9
  ref = C_element
FEATURE [App::DocumentObjectGroupPython] N_element062  label="N_element : 034"  # scripted group (container) (typed FeaturePython)
  n = 2
  ref = N_element
FEATURE [App::DocumentObjectGroupPython] O_element123  label="O_element : 076"  # scripted group (container) (typed FeaturePython)
  n = 6
  ref = O_element
FEATURE [App::DocumentObjectGroupPython] G4_DNA_URIDINE  # scripted group (container) (typed FeaturePython)
  Dunit = g/cm3
  Dvalue = 1
  Group = -> [H_element133,C_element143,N_element062,O_element123]
  conduct = 2
  density = 1
  expand = 3
  formula = G4_DNA_URIDINE
  name = G4_DNA_URIDINE
  specific = 4
FEATURE [App::DocumentObjectGroupPython] H_element134  label="H_element : 081"  # scripted group (container) (typed FeaturePython)
  n = 11
  ref = H_element
FEATURE [App::DocumentObjectGroupPython] C_element144  label="C_element : 089"  # scripted group (container) (typed FeaturePython)
  n = 10
  ref = C_element
FEATURE [App::DocumentObjectGroupPython] N_element063  label="N_element : 035"  # scripted group (container) (typed FeaturePython)
  n = 2
  ref = N_element
FEATURE [App::DocumentObjectGroupPython] O_element124  label="O_element : 077"  # scripted group (container) (typed FeaturePython)
  n = 6
  ref = O_element
FEATURE [App::DocumentObjectGroupPython] G4_DNA_METHYLURIDINE  # scripted group (container) (typed FeaturePython)
  Dunit = g/cm3
  Dvalue = 1
  Group = -> [H_element134,C_element144,N_element063,O_element124]
  conduct = 2
  density = 1
  expand = 3
  formula = G4_DNA_METHYLURIDINE
  name = G4_DNA_METHYLURIDINE
  specific = 4
FEATURE [App::DocumentObjectGroupPython] P_element014  label="P_element : 003"  # scripted group (container) (typed FeaturePython)
  n = 1
  ref = P_element
FEATURE [App::DocumentObjectGroupPython] O_element125  label="O_element : 078"  # scripted group (container) (typed FeaturePython)
  n = 3
  ref = O_element
FEATURE [App::DocumentObjectGroupPython] G4_DNA_MONOPHOSPHATE  # scripted group (container) (typed FeaturePython)
  Dunit = g/cm3
  Dvalue = 1
  Group = -> [P_element014,O_element125]
  conduct = 2
  density = 1
  expand = 3
  formula = G4_DNA_MONOPHOSPHATE
  name = G4_DNA_MONOPHOSPHATE
  specific = 4
FEATURE [App::DocumentObjectGroupPython] H_element135  label="H_element : 082"  # scripted group (container) (typed FeaturePython)
  n = 10
  ref = H_element
FEATURE [App::DocumentObjectGroupPython] C_element145  label="C_element : 090"  # scripted group (container) (typed FeaturePython)
  n = 10
  ref = C_element
FEATURE [App::DocumentObjectGroupPython] N_element064  label="N_element : 036"  # scripted group (container) (typed FeaturePython)
  n = 5
  ref = N_element
FEATURE [App::DocumentObjectGroupPython] O_element126  label="O_element : 079"  # scripted group (container) (typed FeaturePython)
  n = 7
  ref = O_element
FEATURE [App::DocumentObjectGroupPython] P_element015  label="P_element : 004"  # scripted group (container) (typed FeaturePython)
  n = 1
  ref = P_element
FEATURE [App::DocumentObjectGroupPython] G4_DNA_A  # scripted group (container) (typed FeaturePython)
  Dunit = g/cm3
  Dvalue = 1
  Group = -> [H_element135,C_element145,N_element064,O_element126,P_element015]
  conduct = 2
  density = 1
  expand = 3
  formula = G4_DNA_A
  name = G4_DNA_A
  specific = 4
FEATURE [App::DocumentObjectGroupPython] H_element136  label="H_element : 083"  # scripted group (container) (typed FeaturePython)
  n = 10
  ref = H_element
FEATURE [App::DocumentObjectGroupPython] C_element146  label="C_element : 091"  # scripted group (container) (typed FeaturePython)
  n = 10
  ref = C_element
FEATURE [App::DocumentObjectGroupPython] N_element065  label="N_element : 037"  # scripted group (container) (typed FeaturePython)
  n = 5
  ref = N_element
FEATURE [App::DocumentObjectGroupPython] O_element127  label="O_element : 8"  # scripted group (container) (typed FeaturePython)
  n = 8
  ref = O_element
FEATURE [App::DocumentObjectGroupPython] P_element016  label="P_element : 005"  # scripted group (container) (typed FeaturePython)
  n = 1
  ref = P_element
FEATURE [App::DocumentObjectGroupPython] G4_DNA_G  # scripted group (container) (typed FeaturePython)
  Dunit = g/cm3
  Dvalue = 1
  Group = -> [H_element136,C_element146,N_element065,O_element127,P_element016]
  conduct = 2
  density = 1
  expand = 3
  formula = G4_DNA_G
  name = G4_DNA_G
  specific = 4
FEATURE [App::DocumentObjectGroupPython] H_element137  label="H_element : 084"  # scripted group (container) (typed FeaturePython)
  n = 10
  ref = H_element
FEATURE [App::DocumentObjectGroupPython] C_element147  label="C_element : 092"  # scripted group (container) (typed FeaturePython)
  n = 9
  ref = C_element
FEATURE [App::DocumentObjectGroupPython] N_element066  label="N_element : 038"  # scripted group (container) (typed FeaturePython)
  n = 3
  ref = N_element
FEATURE [App::DocumentObjectGroupPython] O_element128  label="O_element : 080"  # scripted group (container) (typed FeaturePython)
  n = 8
  ref = O_element
FEATURE [App::DocumentObjectGroupPython] P_element017  label="P_element : 006"  # scripted group (container) (typed FeaturePython)
  n = 1
  ref = P_element
FEATURE [App::DocumentObjectGroupPython] G4_DNA_C  # scripted group (container) (typed FeaturePython)
  Dunit = g/cm3
  Dvalue = 1
  Group = -> [H_element137,C_element147,N_element066,O_element128,P_element017]
  conduct = 2
  density = 1
  expand = 3
  formula = G4_DNA_C
  name = G4_DNA_C
  specific = 4
FEATURE [App::DocumentObjectGroupPython] H_element138  label="H_element : 085"  # scripted group (container) (typed FeaturePython)
  n = 9
  ref = H_element
FEATURE [App::DocumentObjectGroupPython] C_element148  label="C_element : 093"  # scripted group (container) (typed FeaturePython)
  n = 9
  ref = C_element
FEATURE [App::DocumentObjectGroupPython] N_element067  label="N_element : 039"  # scripted group (container) (typed FeaturePython)
  n = 2
  ref = N_element
FEATURE [App::DocumentObjectGroupPython] O_element129  label="O_element : 9"  # scripted group (container) (typed FeaturePython)
  n = 9
  ref = O_element
FEATURE [App::DocumentObjectGroupPython] P_element018  label="P_element : 007"  # scripted group (container) (typed FeaturePython)
  n = 1
  ref = P_element
FEATURE [App::DocumentObjectGroupPython] G4_DNA_U  # scripted group (container) (typed FeaturePython)
  Dunit = g/cm3
  Dvalue = 1
  Group = -> [H_element138,C_element148,N_element067,O_element129,P_element018]
  conduct = 2
  density = 1
  expand = 3
  formula = G4_DNA_U
  name = G4_DNA_U
  specific = 4
FEATURE [App::DocumentObjectGroupPython] H_element139  label="H_element : 086"  # scripted group (container) (typed FeaturePython)
  n = 11
  ref = H_element
FEATURE [App::DocumentObjectGroupPython] C_element149  label="C_element : 094"  # scripted group (container) (typed FeaturePython)
  n = 10
  ref = C_element
FEATURE [App::DocumentObjectGroupPython] N_element068  label="N_element : 040"  # scripted group (container) (typed FeaturePython)
  n = 2
  ref = N_element
FEATURE [App::DocumentObjectGroupPython] O_element130  label="O_element : 081"  # scripted group (container) (typed FeaturePython)
  n = 9
  ref = O_element
FEATURE [App::DocumentObjectGroupPython] P_element019  label="P_element : 008"  # scripted group (container) (typed FeaturePython)
  n = 1
  ref = P_element
FEATURE [App::DocumentObjectGroupPython] G4_DNA_MU  # scripted group (container) (typed FeaturePython)
  Dunit = g/cm3
  Dvalue = 1
  Group = -> [H_element139,C_element149,N_element068,O_element130,P_element019]
  conduct = 2
  density = 1
  expand = 3
  formula = G4_DNA_MU
  name = G4_DNA_MU
  specific = 4
FEATURE [App::DocumentObjectGroupPython] BioChemical  # scripted group (container) (typed FeaturePython)
  Group = -> [G4_CYTOSINE,G4_THYMINE,G4_URACIL,G4_DNA_ADENINE,G4_DNA_GUANINE,G4_DNA_CYTOSINE,G4_DNA_THYMINE,G4_DNA_URACIL,G4_DNA_ADENOSINE,G4_DNA_GUANOSINE,G4_DNA_CYTIDINE,G4_DNA_URIDINE,G4_DNA_METHYLURIDINE,G4_DNA_MONOPHOSPHATE,G4_DNA_A,G4_DNA_G,G4_DNA_C,G4_DNA_U,G4_DNA_MU]
FEATURE [App::DocumentObjectGroupPython] G4Materials  # scripted group (container) (typed FeaturePython)
  Group = -> [NIST,Element,HEP,Space,BioChemical]
  version = 1
FEATURE [App::DocumentObjectGroupPython] Geant4  # scripted group (container) (typed FeaturePython)
  Group = -> [G4Isotopes,G4Elements,G4Materials]
FEATURE [App::DocumentObjectGroupPython] Materials  # scripted group (container) (typed FeaturePython)
  Group = -> [Geant4]
FEATURE [Part::FeaturePython] GDMLBox_WorldBox  # WARN: FeaturePython — macro-defined, semantics opaque (R4)
  lunit = 2
  material = 5
  x = 100
  y = 100
  z = 100
FEATURE [Part::FeaturePython] GDMLBox_Box  # WARN: FeaturePython — macro-defined, semantics opaque (R4)
  Placement = pos=(30,0,0) rot=(0,0,1;0rad)
  lunit = 2
  material = 0
  x = 10
  y = 10
  z = 10
FEATURE [Part::FeaturePython] GDMLTorus  # WARN: FeaturePython — macro-defined, semantics opaque (R4)
  Placement = pos=(30,0,0) rot=(0,1,0;1.5708rad)
  aunit = deg
  deltaphi = 360
  lunit = 2
  material = 0
  rmax = 2
  rmin = 0
  rtor = 8
  startphi = 0
FEATURE [Part::MultiFuse] Fusion
  Shapes = -> [GDMLBox_Box,GDMLTorus]
FEATURE [Part::FeaturePython] Array  # Draft array (typed FeaturePython)
  AlwaysSyncPlacement = false
  Angle = 180
  ArrayType = 1
  Axis = (0,0,1)
  Base = -> Fusion
  Center = (0,0,0)
  Count = 5
  ExpandArray = false
  Fuse = false
  IntervalAxis = (0,0,0)
  IntervalX = (50,0,0)
  IntervalY = (0,50,0)
  IntervalZ = (0,0,50)
  NumberCircles = 3
  NumberPolar = 5
  NumberX = 2
  NumberY = 2
  NumberZ = 1
  PlacementList = 5 placements: [(0,0,0),(0,0,0),(0,0,0),(0,0,0),(0,0,0)]
  RadialDistance = 50
  ScaleList = (5) [(1,1,1),(1,1,1),(1,1,1),(1,1,1),(1,1,1)]
  Symmetry = 1
  TangentialDistance = 25
FEATURE [Part::FeaturePython] Array001  # Draft array (typed FeaturePython)
  AlwaysSyncPlacement = false
  Angle = 360
  ArrayType = 0
  Axis = (0,0,1)
  Base = -> Array
  Center = (0,0,0)
  Count = 4
  ExpandArray = false
  Fuse = true
  IntervalAxis = (0,0,0)
  IntervalX = (120,0,0)
  IntervalY = (0,120,0)
  IntervalZ = (0,0,100)
  NumberCircles = 3
  NumberPolar = 5
  NumberX = 2
  NumberY = 2
  NumberZ = 1
  PlacementList = 4 placements: [(0,0,0),(0,120,0),(120,0,0),(120,120,0)]
  RadialDistance = 50
  ScaleList = (4) [(1,1,1),(1,1,1),(1,1,1),(1,1,1)]
  Symmetry = 1
  TangentialDistance = 25
FEATURE [App::Part] Part001
  Group = -> [Array,GDMLBox_Box,GDMLTorus,Fusion,Array001]
  Origin = -> Origin004
FEATURE [App::Part] worldVOL
  Group = -> [GDMLBox_WorldBox,Part001]
  Origin = -> Origin
